FCSTD DOCUMENT  (FreeCAD 0.16R)
Label: brakeDiscVs
License: All rights reserved
LicenseURL: http://en.wikipedia.org/wiki/All_rights_reserved
objects: Sketcher::SketchObject×421, Part::Feature×420, App::DocumentObjectGroup×1
note: 841 computed .brp shape members not serialized (recipe doc carries the construction recipe); baked Part::Feature solids carry a one-line shape summary decoded from their .brp

FEATURE [Sketcher::SketchObject] Sketch420
  sketch-geometry (420):
    g0: ArcOfCircle CenterX=0 CenterY=0 CenterZ=0 NormalX=0 NormalY=0 NormalZ=1 Radius=58.5 StartAngle=4.60412 EndAngle=4.62963
    g1: ArcOfCircle CenterX=-27.6007 CenterY=-44.6934 CenterZ=0 NormalX=0 NormalY=0 NormalZ=1 Radius=1 StartAngle=1.8326 EndAngle=4.19648
    g2: ArcOfCircle CenterX=27.6007 CenterY=44.6934 CenterZ=0 NormalX=0 NormalY=0 NormalZ=1 Radius=1 StartAngle=4.97419 EndAngle=7.33807
    g3: ArcOfCircle CenterX=0 CenterY=0 CenterZ=0 NormalX=0 NormalY=0 NormalZ=1 Radius=58.5 StartAngle=0.415326 EndAngle=0.440839
    g4: ArcOfCircle CenterX=0 CenterY=0 CenterZ=0 NormalX=0 NormalY=0 NormalZ=1 Radius=45.5 StartAngle=0.283024 EndAngle=0.327705
    g5: Circle CenterX=-19.0526 CenterY=11 CenterZ=0 NormalX=0 NormalY=0 NormalZ=1 Radius=2.75
    g6: ArcOfCircle CenterX=-46.4894 CenterY=0.993219 CenterZ=0 NormalX=0 NormalY=0 NormalZ=1 Radius=1 StartAngle=3.75246 EndAngle=6.26182
    g7: ArcOfCircle CenterX=-53.0571 CenterY=-15.0104 CenterZ=0 NormalX=0 NormalY=0 NormalZ=1 Radius=1 StartAngle=1.13446 EndAngle=3.0674
    g8: ArcOfCircle CenterX=-26.413 CenterY=-39.4792 CenterZ=0 NormalX=0 NormalY=0 NormalZ=1 Radius=2 StartAngle=0.981156 EndAngle=1.65806
    g9: ArcOfCircle CenterX=52.1283 CenterY=15.9789 CenterZ=0 NormalX=0 NormalY=0 NormalZ=1 Radius=2 StartAngle=6.20458 EndAngle=7.41765
    g10: ArcOfCircle CenterX=0 CenterY=0 CenterZ=0 NormalX=0 NormalY=0 NormalZ=1 Radius=60 StartAngle=2.45564 EndAngle=2.78035
    g11: ArcOfCircle CenterX=45.6102 CenterY=13.2649 CenterZ=0 NormalX=0 NormalY=0 NormalZ=1 Radius=2 StartAngle=3.42462 EndAngle=4.10152
    g12: LineSegment StartX=3.74917 StartY=-26.4937 StartZ=0 EndX=11.5388 EndY=-39.9857 EndZ=0
    g13: ArcOfCircle CenterX=9.05093 CenterY=45.6106 CenterZ=0 NormalX=0 NormalY=0 NormalZ=1 Radius=1 StartAngle=2.00713 EndAngle=4.51649
    g14: ArcOfCircle CenterX=15.4177 CenterY=-52.1835 CenterZ=0 NormalX=0 NormalY=0 NormalZ=1 Radius=1 StartAngle=2.70526 EndAngle=5.29894
    g15: ArcOfCircle CenterX=0 CenterY=-22 CenterZ=0 NormalX=0 NormalY=0 NormalZ=1 Radius=4.5 StartAngle=5.71572 EndAngle=9.99225
    g16: ArcOfCircle CenterX=0 CenterY=0 CenterZ=0 NormalX=0 NormalY=0 NormalZ=1 Radius=45.5 StartAngle=1.50475 EndAngle=1.54929
    g17: LineSegment StartX=-34.5926 StartY=-41.6858 StartZ=0 EndX=-24.0177 EndY=-40.7606 EndZ=0
    g18: ArcOfCircle CenterX=-6.21354 CenterY=-57.1633 CenterZ=0 NormalX=0 NormalY=0 NormalZ=1 Radius=1 StartAngle=2.35619 EndAngle=4.60412
    g19: ArcOfCircle CenterX=34.7669 CenterY=39.6934 CenterZ=0 NormalX=0 NormalY=0 NormalZ=1 Radius=2 StartAngle=1.09765 EndAngle=1.65806
    g20: LineSegment StartX=-45.7581 StartY=4.28185 StartZ=0 EndX=-52.082 EndY=13.3132 EndZ=0
    g21: LineSegment StartX=-40.398 StartY=-10 StartZ=0 EndX=-24.8188 EndY=-10 EndZ=0
    g22: ArcOfCircle CenterX=0 CenterY=0 CenterZ=0 NormalX=0 NormalY=0 NormalZ=1 Radius=45.5 StartAngle=4.82088 EndAngle=4.86556
    g23: LineSegment StartX=52.9735 StartY=17.7915 StartZ=0 EndX=41.1802 EndY=23.2909 EndZ=0
    g24: ArcOfCircle CenterX=19.0526 CenterY=11 CenterZ=0 NormalX=0 NormalY=0 NormalZ=1 Radius=4.5 StartAngle=1.52693 EndAngle=5.80346
    g25: ArcOfCircle CenterX=-14.1368 CenterY=38.4857 CenterZ=0 NormalX=0 NormalY=0 NormalZ=1 Radius=3 StartAngle=0.523599 EndAngle=1.92282
    g26: ArcOfCircle CenterX=-47.3965 CenterY=3.1347 CenterZ=0 NormalX=0 NormalY=0 NormalZ=1 Radius=2 StartAngle=6.21714 EndAngle=6.89405
    g27: ArcOfCircle CenterX=43.346 CenterY=-16.8336 CenterZ=0 NormalX=0 NormalY=0 NormalZ=1 Radius=1 StartAngle=0.261799 EndAngle=2.77117
    g28: ArcOfCircle CenterX=43.346 CenterY=-16.8336 CenterZ=0 NormalX=0 NormalY=0 NormalZ=1 Radius=1 StartAngle=0.261799 EndAngle=2.77117
    g29: ArcOfCircle CenterX=-19.0526 CenterY=11 CenterZ=0 NormalX=0 NormalY=0 NormalZ=1 Radius=4.5 StartAngle=3.62132 EndAngle=7.89785
    g30: ArcOfCircle CenterX=31.9233 CenterY=-27.2929 CenterZ=0 NormalX=0 NormalY=0 NormalZ=1 Radius=2 StartAngle=3.66519 EndAngle=5.57582
    g31: ArcOfCircle CenterX=127.5 CenterY=220.836 CenterZ=0 NormalX=0 NormalY=0 NormalZ=1 Radius=201.5 StartAngle=4.11019 EndAngle=4.1146
    g32: LineSegment StartX=-26.1327 StartY=37.8051 StartZ=0 EndX=-23.9393 EndY=45.9908 EndZ=0
    g33: ArcOfCircle CenterX=51.5908 CenterY=-25.3898 CenterZ=0 NormalX=0 NormalY=0 NormalZ=1 Radius=1 StartAngle=3.57793 EndAngle=5.82585
    g34: ArcOfCircle CenterX=38.3227 CenterY=28.0645 CenterZ=0 NormalX=0 NormalY=0 NormalZ=1 Radius=2 StartAngle=3.77368 EndAngle=4.45059
    g35: ArcOfCircle CenterX=-127.5 CenterY=-220.836 CenterZ=0 NormalX=0 NormalY=0 NormalZ=1 Radius=200 StartAngle=0.940966 EndAngle=1.15343
    g36: ArcOfCircle CenterX=-46.1321 CenterY=11.3174 CenterZ=0 NormalX=0 NormalY=0 NormalZ=1 Radius=2 StartAngle=6.04261 EndAngle=6.71952
    g37: ArcOfCircle CenterX=20.1364 CenterY=49.1411 CenterZ=0 NormalX=0 NormalY=0 NormalZ=1 Radius=1 StartAngle=5.14872 EndAngle=7.29516
    g38: ArcOfCircle CenterX=-47.7836 CenterY=-31.984 CenterZ=0 NormalX=0 NormalY=0 NormalZ=1 Radius=1 StartAngle=1.48353 EndAngle=3.73145
    g39: ArcOfCircle CenterX=-0.993219 CenterY=-46.4894 CenterZ=0 NormalX=0 NormalY=0 NormalZ=1 Radius=1 StartAngle=5.32325 EndAngle=7.83262
    g40: ArcOfCircle CenterX=33.1036 CenterY=-40.5546 CenterZ=0 NormalX=0 NormalY=0 NormalZ=1 Radius=2 StartAngle=5.19474 EndAngle=6.19592
    g41: LineSegment StartX=11.6266 StartY=-44.4631 StartZ=0 EndX=2.988 EndY=-56.8002 EndZ=0
    g42: ArcOfCircle CenterX=127.5 CenterY=220.836 CenterZ=0 NormalX=0 NormalY=0 NormalZ=1 Radius=200 StartAngle=4.08256 EndAngle=4.29502
    g43: ArcOfCircle CenterX=-255 CenterY=0 CenterZ=0 NormalX=0 NormalY=0 NormalZ=1 Radius=201.5 StartAngle=6.28252 EndAngle=6.29087
    g44: ArcOfCircle CenterX=-39.598 CenterY=-14 CenterZ=0 NormalX=0 NormalY=0 NormalZ=1 Radius=2 StartAngle=1.5708 EndAngle=3.48143
    g45: ArcOfCircle CenterX=-24.8188 CenterY=8 CenterZ=0 NormalX=0 NormalY=0 NormalZ=1 Radius=2 StartAngle=0.479729 EndAngle=1.5708
    g46: ArcOfCircle CenterX=46.4277 CenterY=-32.1982 CenterZ=0 NormalX=0 NormalY=0 NormalZ=1 Radius=2 StartAngle=5.67683 EndAngle=6.54498
    g47: ArcOfCircle CenterX=-127.5 CenterY=-220.836 CenterZ=0 NormalX=0 NormalY=0 NormalZ=1 Radius=201.5 StartAngle=1.09765 EndAngle=1.11015
    g48: ArcOfCircle CenterX=-24.1048 CenterY=-39.7644 CenterZ=0 NormalX=0 NormalY=0 NormalZ=1 Radius=1 StartAngle=4.79966 EndAngle=7.30902
    g49: LineSegment StartX=-53.3972 StartY=9.11519 StartZ=0 EndX=-47.3085 EndY=0.419643 EndZ=0
    g50: ArcOfCircle CenterX=0 CenterY=0 CenterZ=0 NormalX=0 NormalY=0 NormalZ=1 Radius=45.5 StartAngle=0.981156 EndAngle=1.02584
    g51: ArcOfCircle CenterX=32.8672 CenterY=34.2928 CenterZ=0 NormalX=0 NormalY=0 NormalZ=1 Radius=2 StartAngle=3.94822 EndAngle=4.62512
    g52: ArcOfCircle CenterX=0 CenterY=22 CenterZ=0 NormalX=0 NormalY=0 NormalZ=1 Radius=4.5 StartAngle=1.52693 EndAngle=1.61467
    g53: ArcOfCircle CenterX=-26.2612 CenterY=31.4857 CenterZ=0 NormalX=0 NormalY=0 NormalZ=1 Radius=3 StartAngle=2.26597 EndAngle=3.66519
    g54: ArcOfCircle CenterX=-32.8672 CenterY=-34.2928 CenterZ=0 NormalX=0 NormalY=0 NormalZ=1 Radius=2 StartAngle=0.806623 EndAngle=1.48353
    g55: LineSegment StartX=3.72902 StartY=-45.8065 StartZ=0 EndX=-6.92065 EndY=-56.4562 EndZ=0
    g56: ArcOfCircle CenterX=-44.0254 CenterY=-14.967 CenterZ=0 NormalX=0 NormalY=0 NormalZ=1 Radius=1 StartAngle=4.10152 EndAngle=6.61089
    g57: ArcOfCircle CenterX=0 CenterY=0 CenterZ=0 NormalX=0 NormalY=0 NormalZ=1 Radius=44 StartAngle=2.43423 EndAngle=2.80176
    g58: LineSegment StartX=-19.1709 StartY=41.7686 StartZ=0 EndX=-14.5114 EndY=51.7609 EndZ=0
    g59: LineSegment StartX=53.1261 StartY=-22.8017 StartZ=0 EndX=46.517 EndY=-8.62831 EndZ=0
    g60: ArcOfCircle CenterX=-13.2649 CenterY=45.6102 CenterZ=0 NormalX=0 NormalY=0 NormalZ=1 Radius=2 StartAngle=4.99541 EndAngle=5.67232
    g61: ArcOfCircle CenterX=39.9023 CenterY=-37.155 CenterZ=0 NormalX=0 NormalY=0 NormalZ=1 Radius=2 StartAngle=5.15739 EndAngle=6.37045
    g62: ArcOfCircle CenterX=-34.7669 CenterY=-39.6934 CenterZ=0 NormalX=0 NormalY=0 NormalZ=1 Radius=2 StartAngle=4.23924 EndAngle=4.79966
    g63: LineSegment StartX=32.3005 StartY=-32.6929 StartZ=0 EndX=31.493 EndY=-41.922 EndZ=0
    g64: LineSegment StartX=-32.3005 StartY=32.6929 StartZ=0 EndX=-31.493 EndY=41.922 EndZ=0
    g65: ArcOfCircle CenterX=127.5 CenterY=-220.836 CenterZ=0 NormalX=0 NormalY=0 NormalZ=1 Radius=201.5 StartAngle=2.14485 EndAngle=2.15735
    g66: ArcOfCircle CenterX=127.5 CenterY=-220.836 CenterZ=0 NormalX=0 NormalY=0 NormalZ=1 Radius=200 StartAngle=1.98816 EndAngle=2.20063
    g67: LineSegment StartX=-28.8593 StartY=-29.9857 StartZ=0 EndX=-21.0697 EndY=-16.4937 EndZ=0
    g68: ArcOfCircle CenterX=0 CenterY=0 CenterZ=0 NormalX=0 NormalY=0 NormalZ=1 Radius=45.5 StartAngle=4.99541 EndAngle=5.04009
    g69: ArcOfCircle CenterX=0 CenterY=0 CenterZ=0 NormalX=0 NormalY=0 NormalZ=1 Radius=60 StartAngle=3.50284 EndAngle=3.82755
    g70: ArcOfCircle CenterX=127.5 CenterY=220.836 CenterZ=0 NormalX=0 NormalY=0 NormalZ=1 Radius=201.5 StartAngle=4.14754 EndAngle=4.15356
    g71: ArcOfCircle CenterX=0 CenterY=22 CenterZ=0 NormalX=0 NormalY=0 NormalZ=1 Radius=4.5 StartAngle=2.57412 EndAngle=6.85065
    g72: ArcOfCircle CenterX=29.122 CenterY=-36.2514 CenterZ=0 NormalX=0 NormalY=0 NormalZ=1 Radius=1 StartAngle=6.02139 EndAngle=8.53075
    g73: ArcOfCircle CenterX=-51.3135 CenterY=23.6469 CenterZ=0 NormalX=0 NormalY=0 NormalZ=1 Radius=2 StartAngle=2.70977 EndAngle=3.57792
    g74: ArcOfCircle CenterX=36.2514 CenterY=29.122 CenterZ=0 NormalX=0 NormalY=0 NormalZ=1 Radius=1 StartAngle=1.309 EndAngle=3.81836
    g75: ArcOfCircle CenterX=-20.9835 CenterY=42.6139 CenterZ=0 NormalX=0 NormalY=0 NormalZ=1 Radius=2 StartAngle=5.16995 EndAngle=5.84685
    g76: LineSegment StartX=41.5341 StartY=-19.6738 StartZ=0 EndX=45.4322 EndY=-34.2216 EndZ=0
    g77: ArcOfCircle CenterX=0 CenterY=0 CenterZ=0 NormalX=0 NormalY=0 NormalZ=1 Radius=45.5 StartAngle=6.04261 EndAngle=6.08729
    g78: ArcOfCircle CenterX=-24.9053 CenterY=46.2496 CenterZ=0 NormalX=0 NormalY=0 NormalZ=1 Radius=1 StartAngle=6.02139 EndAngle=8.38527
    g79: ArcOfCircle CenterX=6.21354 CenterY=57.1633 CenterZ=0 NormalX=0 NormalY=0 NormalZ=1 Radius=1 StartAngle=5.49779 EndAngle=7.74571
    g80: ArcOfCircle CenterX=-255 CenterY=0 CenterZ=0 NormalX=0 NormalY=0 NormalZ=1 Radius=201.5 StartAngle=0.0504506 EndAngle=0.0629534
    g81: LineSegment StartX=-26.5873 StartY=-37.4868 StartZ=0 EndX=-37.5706 EndY=-38.4477 EndZ=0
    g82: ArcOfCircle CenterX=-34.2928 CenterY=32.8672 CenterZ=0 NormalX=0 NormalY=0 NormalZ=1 Radius=2 StartAngle=5.51901 EndAngle=6.19592
    g83: LineSegment StartX=41.5341 StartY=-19.6738 StartZ=0 EndX=45.4322 EndY=-34.2216 EndZ=0
    g84: ArcOfCircle CenterX=-16.992 CenterY=49.9557 CenterZ=0 NormalX=0 NormalY=0 NormalZ=1 Radius=2 StartAngle=2.14484 EndAngle=2.70526
    g85: ArcOfCircle CenterX=51.0983 CenterY=24.1085 CenterZ=0 NormalX=0 NormalY=0 NormalZ=1 Radius=2 StartAngle=0.440839 EndAngle=1.309
    g86: ArcOfCircle CenterX=-51.0983 CenterY=-24.1085 CenterZ=0 NormalX=0 NormalY=0 NormalZ=1 Radius=2 StartAngle=3.58243 EndAngle=4.45059
    g87: LineSegment StartX=19.6738 StartY=41.5341 StartZ=0 EndX=27.8595 EndY=43.7275 EndZ=0
    g88: ArcOfCircle CenterX=0 CenterY=0 CenterZ=0 NormalX=0 NormalY=0 NormalZ=1 Radius=45.5 StartAngle=0.63209 EndAngle=0.676771
    g89: ArcOfCircle CenterX=0 CenterY=0 CenterZ=0 NormalX=0 NormalY=0 NormalZ=1 Radius=44 StartAngle=5.06442 EndAngle=5.40756
    g90: LineSegment StartX=-3.25637 StartY=-57.7208 StartZ=0 EndX=7.80178 EndY=-46.6627 EndZ=0
    g91: LineSegment StartX=-11.0788 StartY=-54.7722 StartZ=0 EndX=-0.419643 EndY=-47.3085 EndZ=0
    g92: LineSegment StartX=45.7581 StartY=-4.28185 StartZ=0 EndX=52.082 EndY=-13.3132 EndZ=0
    g93: LineSegment StartX=37.4868 StartY=-26.5873 StartZ=0 EndX=38.5317 EndY=-38.5308 EndZ=0
    g94: ArcOfCircle CenterX=-7.67463 CenterY=41.2929 CenterZ=0 NormalX=0 NormalY=0 NormalZ=1 Radius=2 StartAngle=1.75456 EndAngle=3.66519
    g95: ArcOfCircle CenterX=20.9835 CenterY=-42.6139 CenterZ=0 NormalX=0 NormalY=0 NormalZ=1 Radius=2 StartAngle=2.02835 EndAngle=2.70526
    g96: ArcOfCircle CenterX=51.7589 CenterY=-10.2623 CenterZ=0 NormalX=0 NormalY=0 NormalZ=1 Radius=2 StartAngle=0.0504502 EndAngle=0.610865
    g97: ArcOfCircle CenterX=-3.1347 CenterY=-47.3965 CenterZ=0 NormalX=0 NormalY=0 NormalZ=1 Radius=2 StartAngle=1.50475 EndAngle=2.18166
    g98: LineSegment StartX=-2.01711 StartY=-27.4937 StartZ=0 EndX=-9.40668 EndY=-40.2929 EndZ=0
    g99: ArcOfCircle CenterX=-52.9011 CenterY=12.7396 CenterZ=0 NormalX=0 NormalY=0 NormalZ=1 Radius=1 StartAngle=0.610866 EndAngle=3.20455
    g100: LineSegment StartX=-46.3099 StartY=-34.6077 StartZ=0 EndX=-30.7308 EndY=-35.9707 EndZ=0
    g101: ArcOfCircle CenterX=19.0526 CenterY=-11 CenterZ=0 NormalX=0 NormalY=0 NormalZ=1 Radius=4.5 StartAngle=5.71572 EndAngle=5.80346
    g102: LineSegment StartX=26.5873 StartY=37.4868 StartZ=0 EndX=37.5706 EndY=38.4477 EndZ=0
    g103: ArcOfCircle CenterX=-12.226 CenterY=-53.1339 CenterZ=0 NormalX=0 NormalY=0 NormalZ=1 Radius=2 StartAngle=4.11019 EndAngle=5.32325
    g104: ArcOfCircle CenterX=0 CenterY=0 CenterZ=0 NormalX=0 NormalY=0 NormalZ=1 Radius=45.5 StartAngle=4.47181 EndAngle=4.51649
    g105: ArcOfCircle CenterX=12.226 CenterY=53.1339 CenterZ=0 NormalX=0 NormalY=0 NormalZ=1 Radius=2 StartAngle=0.968596 EndAngle=2.18166
    g106: LineSegment StartX=48.3595 StartY=-31.6805 StartZ=0 EndX=44.312 EndY=-16.5748 EndZ=0
    g107: LineSegment StartX=-18.8046 StartY=50.801 StartZ=0 EndX=-23.2909 EndY=41.1802 EndZ=0
    g108: ArcOfCircle CenterX=-19.3376 CenterY=-17.4937 CenterZ=0 NormalX=0 NormalY=0 NormalZ=1 Radius=2 StartAngle=1.52693 EndAngle=2.61799
    g109: ArcOfCircle CenterX=-5.17792 CenterY=56.2622 CenterZ=0 NormalX=0 NormalY=0 NormalZ=1 Radius=2 StartAngle=1.66257 EndAngle=2.53073
    g110: ArcOfCircle CenterX=-127.5 CenterY=220.836 CenterZ=0 NormalX=0 NormalY=0 NormalZ=1 Radius=201.5 StartAngle=5.19474 EndAngle=5.20076
    g111: LineSegment StartX=-32.6929 StartY=-32.3005 StartZ=0 EndX=-47.6965 EndY=-30.9878 EndZ=0
    g112: ArcOfCircle CenterX=-7.09467 CenterY=45.9556 CenterZ=0 NormalX=0 NormalY=0 NormalZ=1 Radius=1 StartAngle=2.35619 EndAngle=4.86556
    g113: ArcOfCircle CenterX=0 CenterY=0 CenterZ=0 NormalX=0 NormalY=0 NormalZ=1 Radius=45.5 StartAngle=5.16995 EndAngle=5.21463
    g114: ArcOfCircle CenterX=51.0983 CenterY=24.1085 CenterZ=0 NormalX=0 NormalY=0 NormalZ=1 Radius=2 StartAngle=0.440839 EndAngle=1.309
    g115: ArcOfCircle CenterX=5.48122 CenterY=25.4937 CenterZ=0 NormalX=0 NormalY=0 NormalZ=1 Radius=2 StartAngle=2.61799 EndAngle=3.70906
    g116: ArcOfCircle CenterX=19.1562 CenterY=43.466 CenterZ=0 NormalX=0 NormalY=0 NormalZ=1 Radius=2 StartAngle=4.29728 EndAngle=4.97419
    g117: LineSegment StartX=-53.1261 StartY=22.8017 StartZ=0 EndX=-46.517 EndY=8.62831 EndZ=0
    g118: ArcOfCircle CenterX=24.8188 CenterY=8 CenterZ=0 NormalX=0 NormalY=0 NormalZ=1 Radius=2 StartAngle=1.5708 EndAngle=2.66186
    g119: ArcOfCircle CenterX=26.2612 CenterY=-31.4857 CenterZ=0 NormalX=0 NormalY=0 NormalZ=1 Radius=3 StartAngle=5.40756 EndAngle=6.80678
    g120: LineSegment StartX=-51.6159 StartY=-26.0403 StartZ=0 EndX=-36.5102 EndY=-30.0879 EndZ=0
    g121: ArcOfCircle CenterX=-39.598 CenterY=14 CenterZ=0 NormalX=0 NormalY=0 NormalZ=1 Radius=2 StartAngle=2.80176 EndAngle=4.71239
    g122: ArcOfCircle CenterX=13.5292 CenterY=53.454 CenterZ=0 NormalX=0 NormalY=0 NormalZ=1 Radius=1 StartAngle=5.32325 EndAngle=7.25619
    g123: ArcOfCircle CenterX=-46.1356 CenterY=-32.6153 CenterZ=0 NormalX=0 NormalY=0 NormalZ=1 Radius=2 StartAngle=3.75696 EndAngle=4.62512
    g124: ArcOfCircle CenterX=-25.6322 CenterY=-44.6683 CenterZ=0 NormalX=0 NormalY=0 NormalZ=1 Radius=2 StartAngle=4.18812 EndAngle=4.97419
    g125: ArcOfCircle CenterX=39.4792 CenterY=-26.413 CenterZ=0 NormalX=0 NormalY=0 NormalZ=1 Radius=2 StartAngle=2.55195 EndAngle=3.22886
    g126: LineSegment StartX=41.7686 StartY=19.1709 StartZ=0 EndX=52.6345 EndY=14.1041 EndZ=0
    g127: ArcOfCircle CenterX=-0.285064 CenterY=28.4937 CenterZ=0 NormalX=0 NormalY=0 NormalZ=1 Radius=2 StartAngle=3.66519 EndAngle=4.75626
    g128: ArcOfCircle CenterX=16.8336 CenterY=43.346 CenterZ=0 NormalX=0 NormalY=0 NormalZ=1 Radius=1 StartAngle=1.8326 EndAngle=4.34196
    g129: ArcOfCircle CenterX=26.413 CenterY=39.4792 CenterZ=0 NormalX=0 NormalY=0 NormalZ=1 Radius=2 StartAngle=4.12275 EndAngle=4.79966
    g130: ArcOfCircle CenterX=51.3135 CenterY=-23.6469 CenterZ=0 NormalX=0 NormalY=0 NormalZ=1 Radius=2 StartAngle=5.85136 EndAngle=6.71952
    g131: ArcOfCircle CenterX=0 CenterY=0 CenterZ=0 NormalX=0 NormalY=0 NormalZ=1 Radius=58.5 StartAngle=0.589859 EndAngle=0.615372
    g132: ArcOfCircle CenterX=-19.0526 CenterY=-11 CenterZ=0 NormalX=0 NormalY=0 NormalZ=1 Radius=4.5 StartAngle=3.62132 EndAngle=3.70906
    g133: ArcOfCircle CenterX=127.5 CenterY=-220.836 CenterZ=0 NormalX=0 NormalY=0 NormalZ=1 Radius=201.5 StartAngle=2.09373 EndAngle=2.10208
    g134: ArcOfCircle CenterX=255 CenterY=0 CenterZ=0 NormalX=0 NormalY=0 NormalZ=1 Radius=201.5 StartAngle=3.06299 EndAngle=3.0674
    g135: ArcOfCircle CenterX=-40.7576 CenterY=-22.3845 CenterZ=0 NormalX=0 NormalY=0 NormalZ=1 Radius=1.00001 StartAngle=4.27606 EndAngle=6.79205
    g136: LineSegment StartX=-30.1913 StartY=-28.2929 StartZ=0 EndX=-22.8017 EndY=-15.4937 EndZ=0
    g137: LineSegment StartX=-48.3595 StartY=31.6805 StartZ=0 EndX=-44.312 EndY=16.5748 EndZ=0
    g138: ArcOfCircle CenterX=-38.3227 CenterY=-28.0645 CenterZ=0 NormalX=0 NormalY=0 NormalZ=1 Radius=2 StartAngle=0.63209 EndAngle=1.309
    g139: ArcOfCircle CenterX=127.5 CenterY=220.836 CenterZ=0 NormalX=0 NormalY=0 NormalZ=1 Radius=201.5 StartAngle=4.23924 EndAngle=4.25174
    g140: ArcOfCircle CenterX=3.80716 CenterY=-57.3738 CenterZ=0 NormalX=0 NormalY=0 NormalZ=1 Radius=1 StartAngle=2.53073 EndAngle=4.77865
    g141: ArcOfCircle CenterX=0 CenterY=0 CenterZ=0 NormalX=0 NormalY=0 NormalZ=1 Radius=45.5 StartAngle=4.12275 EndAngle=4.16743
    g142: LineSegment StartX=-28.8593 StartY=29.9857 StartZ=0 EndX=-21.0697 EndY=16.4937 EndZ=0
    g143: ArcOfCircle CenterX=0 CenterY=0 CenterZ=0 NormalX=0 NormalY=0 NormalZ=1 Radius=45.5 StartAngle=1.85382 EndAngle=1.8985
    g144: ArcOfCircle CenterX=-7.67463 CenterY=-41.2929 CenterZ=0 NormalX=0 NormalY=0 NormalZ=1 Radius=2 StartAngle=2.61799 EndAngle=4.52863
    g145: ArcOfCircle CenterX=0 CenterY=0 CenterZ=0 NormalX=0 NormalY=0 NormalZ=1 Radius=44 StartAngle=4.52863 EndAngle=4.89615
    g146: ArcOfCircle CenterX=-39.5279 CenterY=38.4436 CenterZ=0 NormalX=0 NormalY=0 NormalZ=1 Radius=1 StartAngle=0.0872665 EndAngle=2.0202
    g147: ArcOfCircle CenterX=0 CenterY=0 CenterZ=0 NormalX=0 NormalY=0 NormalZ=1 Radius=45.5 StartAngle=2.72649 EndAngle=2.77117
    g148: ArcOfCircle CenterX=-14.1368 CenterY=-38.4857 CenterZ=0 NormalX=0 NormalY=0 NormalZ=1 Radius=3 StartAngle=4.36036 EndAngle=5.75959
    g149: ArcOfCircle CenterX=0 CenterY=0 CenterZ=0 NormalX=0 NormalY=0 NormalZ=1 Radius=45.5 StartAngle=3.07555 EndAngle=3.12023
    g150: ArcOfCircle CenterX=39.5279 CenterY=-38.4436 CenterZ=0 NormalX=0 NormalY=0 NormalZ=1 Radius=1 StartAngle=3.22886 EndAngle=5.16179
    g151: ArcOfCircle CenterX=53.0571 CenterY=15.0104 CenterZ=0 NormalX=0 NormalY=0 NormalZ=1 Radius=1 StartAngle=4.27606 EndAngle=6.20899
    g152: ArcOfCircle CenterX=0 CenterY=0 CenterZ=0 NormalX=0 NormalY=0 NormalZ=1 Radius=45.5 StartAngle=6.21714 EndAngle=6.26182
    g153: ArcOfCircle CenterX=-43.346 CenterY=16.8336 CenterZ=0 NormalX=0 NormalY=0 NormalZ=1 Radius=1 StartAngle=3.40339 EndAngle=5.91276
    g154: ArcOfCircle CenterX=24.5338 CenterY=14.4937 CenterZ=0 NormalX=0 NormalY=0 NormalZ=1 Radius=2 StartAngle=2.61799 EndAngle=3.70906
    g155: LineSegment StartX=-41.7686 StartY=-19.1709 StartZ=0 EndX=-52.6345 EndY=-14.1041 EndZ=0
    g156: ArcOfCircle CenterX=255 CenterY=0 CenterZ=0 NormalX=0 NormalY=0 NormalZ=1 Radius=200 StartAngle=3.03536 EndAngle=3.24782
    g157: ArcOfCircle CenterX=0 CenterY=0 CenterZ=0 NormalX=0 NormalY=0 NormalZ=1 Radius=58.5 StartAngle=0.415326 EndAngle=0.440839
    g158: ArcOfCircle CenterX=-5.48122 CenterY=25.4937 CenterZ=0 NormalX=0 NormalY=0 NormalZ=1 Radius=2 StartAngle=5.71572 EndAngle=6.80678
    g159: ArcOfCircle CenterX=6.21354 CenterY=57.1633 CenterZ=0 NormalX=0 NormalY=0 NormalZ=1 Radius=1 StartAngle=5.49779 EndAngle=7.74571
    g160: ArcOfCircle CenterX=46.3981 CenterY=-33.9627 CenterZ=0 NormalX=0 NormalY=0 NormalZ=1 Radius=1 StartAngle=3.40339 EndAngle=5.65131
    g161: ArcOfCircle CenterX=0 CenterY=0 CenterZ=0 NormalX=0 NormalY=0 NormalZ=1 Radius=45.5 StartAngle=0.63209 EndAngle=0.676771
    g162: ArcOfCircle CenterX=0 CenterY=0 CenterZ=0 NormalX=0 NormalY=0 NormalZ=1 Radius=45.5 StartAngle=2.02835 EndAngle=2.07303
    g163: ArcOfCircle CenterX=14.967 CenterY=-44.0254 CenterZ=0 NormalX=0 NormalY=0 NormalZ=1 Radius=1 StartAngle=5.67232 EndAngle=8.18169
    g164: LineSegment StartX=-51.6159 StartY=-26.0403 StartZ=0 EndX=-36.5102 EndY=-30.0879 EndZ=0
    g165: LineSegment StartX=37.8051 StartY=26.1327 StartZ=0 EndX=52.3528 EndY=22.2346 EndZ=0
    g166: LineSegment StartX=3.74917 StartY=26.4937 StartZ=0 EndX=11.5388 EndY=39.9857 EndZ=0
    g167: ArcOfCircle CenterX=13.2649 CenterY=-45.6102 CenterZ=0 NormalX=0 NormalY=0 NormalZ=1 Radius=2 StartAngle=1.85382 EndAngle=2.53073
    g168: ArcOfCircle CenterX=-127.5 CenterY=-220.836 CenterZ=0 NormalX=0 NormalY=0 NormalZ=1 Radius=201.5 StartAngle=1.00595 EndAngle=1.01197
    g169: ArcOfCircle CenterX=39.598 CenterY=14 CenterZ=0 NormalX=0 NormalY=0 NormalZ=1 Radius=2 StartAngle=4.71239 EndAngle=6.62302
    g170: ArcOfCircle CenterX=-0.285064 CenterY=-28.4937 CenterZ=0 NormalX=0 NormalY=0 NormalZ=1 Radius=2 StartAngle=1.52693 EndAngle=2.61799
    g171: ArcOfCircle CenterX=-36.2514 CenterY=-29.122 CenterZ=0 NormalX=0 NormalY=0 NormalZ=1 Radius=1 StartAngle=4.45059 EndAngle=6.95996
    g172: ArcOfCircle CenterX=-19.0526 CenterY=11 CenterZ=0 NormalX=0 NormalY=0 NormalZ=1 Radius=4.5 StartAngle=2.57412 EndAngle=2.66186
    g173: ArcOfCircle CenterX=-31.9233 CenterY=-27.2929 CenterZ=0 NormalX=0 NormalY=0 NormalZ=1 Radius=2 StartAngle=3.84895 EndAngle=5.75959
    g174: ArcOfCircle CenterX=-127.5 CenterY=220.836 CenterZ=0 NormalX=0 NormalY=0 NormalZ=1 Radius=201.5 StartAngle=5.23532 EndAngle=5.24367
    g175: Circle CenterX=-19.0526 CenterY=-11 CenterZ=0 NormalX=0 NormalY=0 NormalZ=1 Radius=2.75
    g176: ArcOfCircle CenterX=18.5695 CenterY=48.9458 CenterZ=0 NormalX=0 NormalY=0 NormalZ=1 Radius=2 StartAngle=1.00595 EndAngle=2.00713
    g177: ArcOfCircle CenterX=52.6116 CenterY=23.2006 CenterZ=0 NormalX=0 NormalY=0 NormalZ=1 Radius=1 StartAngle=4.45059 EndAngle=6.69851
    g178: LineSegment StartX=-37.8051 StartY=-26.1327 StartZ=0 EndX=-52.3528 EndY=-22.2346 EndZ=0
    g179: ArcOfCircle CenterX=24.5338 CenterY=-14.4937 CenterZ=0 NormalX=0 NormalY=0 NormalZ=1 Radius=2 StartAngle=2.57412 EndAngle=3.66519
    g180: LineSegment StartX=-39.598 StartY=12 StartZ=0 EndX=-24.8188 EndY=12 EndZ=0
    g181: ArcOfCircle CenterX=0 CenterY=0 CenterZ=0 NormalX=0 NormalY=0 NormalZ=1 Radius=58.5 StartAngle=2.68425 EndAngle=2.70977
    g182: LineSegment StartX=-25.1146 StartY=-46.6002 StartZ=0 EndX=-16.5748 EndY=-44.312 EndZ=0
    g183: ArcOfCircle CenterX=-19.3376 CenterY=17.4937 CenterZ=0 NormalX=0 NormalY=0 NormalZ=1 Radius=2 StartAngle=3.66519 EndAngle=4.75626
    g184: LineSegment StartX=-3.74917 StartY=-26.4937 StartZ=0 EndX=-11.5388 EndY=-39.9857 EndZ=0
    g185: ArcOfCircle CenterX=0 CenterY=0 CenterZ=0 NormalX=0 NormalY=0 NormalZ=1 Radius=45.5 StartAngle=2.37742 EndAngle=2.4221
    g186: ArcOfCircle CenterX=0 CenterY=0 CenterZ=0 NormalX=0 NormalY=0 NormalZ=1 Radius=45.5 StartAngle=1.15569 EndAngle=1.20037
    g187: LineSegment StartX=-11.5388 StartY=39.9857 StartZ=0 EndX=-3.74917 EndY=26.4937 EndZ=0
    g188: ArcOfCircle CenterX=51.5 CenterY=0.135994 CenterZ=0 NormalX=0 NormalY=0 NormalZ=1 Radius=2 StartAngle=6.28252 EndAngle=7.06858
    g189: ArcOfCircle CenterX=-52.6256 CenterY=-7.13188 CenterZ=0 NormalX=0 NormalY=0 NormalZ=1 Radius=1 StartAngle=0.959931 EndAngle=3.10637
    g190: LineSegment StartX=-11.6266 StartY=44.4631 StartZ=0 EndX=-2.988 EndY=56.8002 EndZ=0
    g191: LineSegment StartX=-45.8065 StartY=-3.72902 StartZ=0 EndX=-51.7989 EndY=2.26334 EndZ=0
    g192: ArcOfCircle CenterX=7.09467 CenterY=-45.9556 CenterZ=0 NormalX=0 NormalY=0 NormalZ=1 Radius=1 StartAngle=5.49779 EndAngle=8.00715
    g193: ArcOfCircle CenterX=-127.5 CenterY=220.836 CenterZ=0 NormalX=0 NormalY=0 NormalZ=1 Radius=200 StartAngle=5.12976 EndAngle=5.34222
    g194: ArcOfCircle CenterX=255 CenterY=0 CenterZ=0 NormalX=0 NormalY=0 NormalZ=1 Radius=201.5 StartAngle=3.19204 EndAngle=3.20455
    g195: ArcOfCircle CenterX=-19.1562 CenterY=-43.466 CenterZ=0 NormalX=0 NormalY=0 NormalZ=1 Radius=2 StartAngle=1.15569 EndAngle=1.8326
    g196: ArcOfCircle CenterX=-5.48122 CenterY=-25.4937 CenterZ=0 NormalX=0 NormalY=0 NormalZ=1 Radius=2 StartAngle=5.75959 EndAngle=6.85065
    g197: ArcOfCircle CenterX=24.8188 CenterY=14 CenterZ=0 NormalX=0 NormalY=0 NormalZ=1 Radius=2 StartAngle=3.62132 EndAngle=4.71239
    g198: ArcOfCircle CenterX=-5.14323 CenterY=47.2207 CenterZ=0 NormalX=0 NormalY=0 NormalZ=1 Radius=2 StartAngle=4.82088 EndAngle=5.49779
    g199: LineSegment StartX=28.8593 StartY=29.9857 StartZ=0 EndX=21.0697 EndY=16.4937 EndZ=0
    g200: LineSegment StartX=3.25637 StartY=57.7208 StartZ=0 EndX=-7.80178 EndY=46.6627 EndZ=0
    g201: ArcOfCircle CenterX=0.285064 CenterY=-28.4937 CenterZ=0 NormalX=0 NormalY=0 NormalZ=1 Radius=2 StartAngle=0.523599 EndAngle=1.61467
    g202: LineSegment StartX=24.8188 StartY=12 StartZ=0 EndX=39.598 EndY=12 EndZ=0
    g203: ArcOfCircle CenterX=0 CenterY=0 CenterZ=0 NormalX=0 NormalY=0 NormalZ=1 Radius=45.5 StartAngle=2.20289 EndAngle=2.24757
    g204: ArcOfCircle CenterX=14.1368 CenterY=-38.4857 CenterZ=0 NormalX=0 NormalY=0 NormalZ=1 Radius=3 StartAngle=3.66519 EndAngle=5.06442
    g205: LineSegment StartX=6.81622 StartY=-57.4094 StartZ=0 EndX=15.7861 EndY=-44.599 EndZ=0
    g206: ArcOfCircle CenterX=39.598 CenterY=-14 CenterZ=0 NormalX=0 NormalY=0 NormalZ=1 Radius=2 StartAngle=5.94335 EndAngle=7.85398
    g207: ArcOfCircle CenterX=0.993219 CenterY=46.4894 CenterZ=0 NormalX=0 NormalY=0 NormalZ=1 Radius=1.00001 StartAngle=2.18166 EndAngle=4.69766
    g208: LineSegment StartX=-44.3194 StartY=12.1626 StartZ=0 EndX=-50.6845 EndY=25.8124 EndZ=0
    g209: ArcOfCircle CenterX=47.3965 CenterY=-3.1347 CenterZ=0 NormalX=0 NormalY=0 NormalZ=1 Radius=2 StartAngle=3.07555 EndAngle=3.75246
    g210: ArcOfCircle CenterX=47.2207 CenterY=5.14323 CenterZ=0 NormalX=0 NormalY=0 NormalZ=1 Radius=2 StartAngle=3.25008 EndAngle=3.92699
    g211: ArcOfCircle CenterX=255 CenterY=0 CenterZ=0 NormalX=0 NormalY=0 NormalZ=1 Radius=201.5 StartAngle=3.10035 EndAngle=3.10637
    g212: ArcOfCircle CenterX=0 CenterY=0 CenterZ=0 NormalX=0 NormalY=0 NormalZ=1 Radius=44 StartAngle=4.01722 EndAngle=4.36036
    g213: ArcOfCircle CenterX=24.9053 CenterY=-46.2496 CenterZ=0 NormalX=0 NormalY=0 NormalZ=1 Radius=1 StartAngle=2.87979 EndAngle=5.24367
    g214: ArcOfCircle CenterX=-24.5338 CenterY=-14.4937 CenterZ=0 NormalX=0 NormalY=0 NormalZ=1 Radius=2 StartAngle=5.75959 EndAngle=6.85065
    g215: LineSegment StartX=-27.7996 StartY=45.05 StartZ=0 EndX=-30.0879 EndY=36.5102 EndZ=0
    g216: ArcOfCircle CenterX=-43.466 CenterY=19.1562 CenterZ=0 NormalX=0 NormalY=0 NormalZ=1 Radius=2 StartAngle=5.86808 EndAngle=6.54498
    g217: LineSegment StartX=4.28185 StartY=45.7581 StartZ=0 EndX=14.1028 EndY=52.6348 EndZ=0
    g218: ArcOfCircle CenterX=-37.4834 CenterY=-39.4439 CenterZ=0 NormalX=0 NormalY=0 NormalZ=1 Radius=1 StartAngle=1.65806 EndAngle=4.25174
    g219: ArcOfCircle CenterX=-11.3174 CenterY=-46.1321 CenterZ=0 NormalX=0 NormalY=0 NormalZ=1 Radius=2 StartAngle=1.33022 EndAngle=2.00713
    g220: LineSegment StartX=-52.9735 StartY=-17.7915 StartZ=0 EndX=-41.1802 EndY=-23.2909 EndZ=0
    g221: ArcOfCircle CenterX=0 CenterY=0 CenterZ=0 NormalX=0 NormalY=0 NormalZ=1 Radius=45.5 StartAngle=3.94822 EndAngle=3.9929
    g222: LineSegment StartX=26.1327 StartY=-37.8051 StartZ=0 EndX=23.9393 EndY=-45.9908 EndZ=0
    g223: ArcOfCircle CenterX=0 CenterY=0 CenterZ=0 NormalX=0 NormalY=0 NormalZ=1 Radius=58.5 StartAngle=5.65131 EndAngle=5.67683
    g224: ArcOfCircle CenterX=-47.2207 CenterY=-5.14323 CenterZ=0 NormalX=0 NormalY=0 NormalZ=1 Radius=2 StartAngle=0.108491 EndAngle=0.785398
    g225: ArcOfCircle CenterX=0 CenterY=0 CenterZ=0 NormalX=0 NormalY=0 NormalZ=1 Radius=45.5 StartAngle=4.29728 EndAngle=4.34196
    g226: LineSegment StartX=24.8188 StartY=10 StartZ=0 EndX=40.398 EndY=10 EndZ=0
    g227: LineSegment StartX=21.0697 StartY=-16.4937 StartZ=0 EndX=28.8593 EndY=-29.9857 EndZ=0
    g228: LineSegment StartX=32.6929 StartY=32.3005 StartZ=0 EndX=47.6965 EndY=30.9878 EndZ=0
    g229: ArcOfCircle CenterX=0 CenterY=0 CenterZ=0 NormalX=0 NormalY=0 NormalZ=1 Radius=45.5 StartAngle=2.90102 EndAngle=2.9457
    g230: ArcOfCircle CenterX=-45.6102 CenterY=-13.2649 CenterZ=0 NormalX=0 NormalY=0 NormalZ=1 Radius=2 StartAngle=0.283024 EndAngle=0.959931
    g231: ArcOfCircle CenterX=0 CenterY=0 CenterZ=0 NormalX=0 NormalY=0 NormalZ=1 Radius=45.5 StartAngle=1.67929 EndAngle=1.72397
    g232: ArcOfCircle CenterX=0 CenterY=0 CenterZ=0 NormalX=0 NormalY=0 NormalZ=1 Radius=45.5 StartAngle=5.69354 EndAngle=5.73823
    g233: LineSegment StartX=27.7996 StartY=-45.05 StartZ=0 EndX=30.0879 EndY=-36.5102 EndZ=0
    g234: LineSegment StartX=-35.096 StartY=40.7289 StartZ=0 EndX=-35.9707 EndY=30.7308 EndZ=0
    g235: ArcOfCircle CenterX=7.67463 CenterY=41.2929 CenterZ=0 NormalX=0 NormalY=0 NormalZ=1 Radius=2 StartAngle=5.75959 EndAngle=7.67022
    g236: ArcOfCircle CenterX=0 CenterY=0 CenterZ=0 NormalX=0 NormalY=0 NormalZ=1 Radius=58.5 StartAngle=3.55692 EndAngle=3.58243
    g237: LineSegment StartX=-40.398 StartY=10 StartZ=0 EndX=-24.8188 EndY=10 EndZ=0
    g238: ArcOfCircle CenterX=5.14323 CenterY=-47.2207 CenterZ=0 NormalX=0 NormalY=0 NormalZ=1 Radius=2 StartAngle=1.67929 EndAngle=2.35619
    g239: ArcOfCircle CenterX=4.67058 CenterY=56.3066 CenterZ=0 NormalX=0 NormalY=0 NormalZ=1 Radius=2 StartAngle=1.48804 EndAngle=2.35619
    g240: ArcOfCircle CenterX=16.992 CenterY=-49.9557 CenterZ=0 NormalX=0 NormalY=0 NormalZ=1 Radius=2 StartAngle=5.28644 EndAngle=5.84685
    g241: ArcOfCircle CenterX=-40.398 CenterY=7 CenterZ=0 NormalX=0 NormalY=0 NormalZ=1 Radius=3 StartAngle=1.5708 EndAngle=2.97002
    g242: ArcOfCircle CenterX=32.4892 CenterY=-42.0092 CenterZ=0 NormalX=0 NormalY=0 NormalZ=1 Radius=1 StartAngle=3.05433 EndAngle=5.20076
    g243: ArcOfCircle CenterX=-34.9745 CenterY=30.6437 CenterZ=0 NormalX=0 NormalY=0 NormalZ=1 Radius=1 StartAngle=3.05433 EndAngle=5.56369
    g244: LineSegment StartX=2.01711 StartY=-27.4937 StartZ=0 EndX=9.40668 EndY=-40.2929 EndZ=0
    g245: LineSegment StartX=-4.28185 StartY=-45.7581 StartZ=0 EndX=-14.1028 EndY=-52.6348 EndZ=0
    g246: ArcOfCircle CenterX=0 CenterY=0 CenterZ=0 NormalX=0 NormalY=0 NormalZ=1 Radius=44 StartAngle=0.339837 EndAngle=0.707361
    g247: ArcOfCircle CenterX=19.3376 CenterY=17.4937 CenterZ=0 NormalX=0 NormalY=0 NormalZ=1 Radius=2 StartAngle=4.66852 EndAngle=5.75959
    g248: ArcOfCircle CenterX=-52.6116 CenterY=-23.2006 CenterZ=0 NormalX=0 NormalY=0 NormalZ=1 Radius=1 StartAngle=1.309 EndAngle=3.55692
    g249: ArcOfCircle CenterX=5.17792 CenterY=-56.2622 CenterZ=0 NormalX=0 NormalY=0 NormalZ=1 Radius=2 StartAngle=4.80416 EndAngle=5.67232
    g250: ArcOfCircle CenterX=-40.398 CenterY=-7 CenterZ=0 NormalX=0 NormalY=0 NormalZ=1 Radius=3 StartAngle=3.31316 EndAngle=4.71239
    g251: ArcOfCircle CenterX=-52.1283 CenterY=-15.9789 CenterZ=0 NormalX=0 NormalY=0 NormalZ=1 Radius=2 StartAngle=3.06299 EndAngle=4.27606
    g252: LineSegment StartX=37.8051 StartY=26.1327 StartZ=0 EndX=52.3528 EndY=22.2346 EndZ=0
    g253: ArcOfCircle CenterX=0 CenterY=0 CenterZ=0 NormalX=0 NormalY=0 NormalZ=1 Radius=58.5 StartAngle=1.63706 EndAngle=1.66257
    g254: LineSegment StartX=25.1146 StartY=46.6002 StartZ=0 EndX=16.5748 EndY=44.312 EndZ=0
    g255: ArcOfCircle CenterX=-39.4792 CenterY=26.413 CenterZ=0 NormalX=0 NormalY=0 NormalZ=1 Radius=2 StartAngle=5.69354 EndAngle=6.37045
    g256: ArcOfCircle CenterX=51.6731 CenterY=8.39128 CenterZ=0 NormalX=0 NormalY=0 NormalZ=1 Radius=2 StartAngle=6.24194 EndAngle=7.24312
    g257: ArcOfCircle CenterX=-42.6139 CenterY=-20.9835 CenterZ=0 NormalX=0 NormalY=0 NormalZ=1 Radius=2 StartAngle=0.457557 EndAngle=1.13446
    g258: ArcOfCircle CenterX=37.4834 CenterY=39.4439 CenterZ=0 NormalX=0 NormalY=0 NormalZ=1 Radius=1 StartAngle=4.79966 EndAngle=7.39334
    g259: LineSegment StartX=46.3099 StartY=34.6077 StartZ=0 EndX=30.7308 EndY=35.9707 EndZ=0
    g260: ArcOfCircle CenterX=39.7644 CenterY=-24.1048 CenterZ=0 NormalX=0 NormalY=0 NormalZ=1 Radius=1 StartAngle=0.087267 EndAngle=2.59664
    g261: ArcOfCircle CenterX=0 CenterY=0 CenterZ=0 NormalX=0 NormalY=0 NormalZ=1 Radius=45.5 StartAngle=3.25008 EndAngle=3.29476
    g262: ArcOfCircle CenterX=-127.5 CenterY=220.836 CenterZ=0 NormalX=0 NormalY=0 NormalZ=1 Radius=201.5 StartAngle=5.28644 EndAngle=5.29894
    g263: ArcOfCircle CenterX=19.0526 CenterY=-11 CenterZ=0 NormalX=0 NormalY=0 NormalZ=1 Radius=4.5 StartAngle=0.479729 EndAngle=4.75626
    g264: ArcOfCircle CenterX=-24.8188 CenterY=14 CenterZ=0 NormalX=0 NormalY=0 NormalZ=1 Radius=2 StartAngle=4.71239 EndAngle=5.80346
    g265: LineSegment StartX=30.1913 StartY=28.2929 StartZ=0 EndX=22.8017 EndY=15.4937 EndZ=0
    g266: ArcOfCircle CenterX=11.3174 CenterY=46.1321 CenterZ=0 NormalX=0 NormalY=0 NormalZ=1 Radius=2 StartAngle=4.47181 EndAngle=5.14872
    g267: ArcOfCircle CenterX=0 CenterY=0 CenterZ=0 NormalX=0 NormalY=0 NormalZ=1 Radius=45.5 StartAngle=5.34448 EndAngle=5.38916
    g268: ArcOfCircle CenterX=0 CenterY=0 CenterZ=0 NormalX=0 NormalY=0 NormalZ=1 Radius=60 StartAngle=4.55004 EndAngle=4.87474
    g269: ArcOfCircle CenterX=255 CenterY=0 CenterZ=0 NormalX=0 NormalY=0 NormalZ=1 Radius=201.5 StartAngle=3.14092 EndAngle=3.14928
    g270: ArcOfCircle CenterX=-25.8678 CenterY=44.5324 CenterZ=0 NormalX=0 NormalY=0 NormalZ=1 Radius=2 StartAngle=2.09373 EndAngle=2.87979
    g271: LineSegment StartX=35.096 StartY=-40.7289 StartZ=0 EndX=35.9707 EndY=-30.7308 EndZ=0
    g272: ArcOfCircle CenterX=0 CenterY=0 CenterZ=0 NormalX=0 NormalY=0 NormalZ=1 Radius=45.5 StartAngle=3.42462 EndAngle=3.4693
    g273: ArcOfCircle CenterX=-51.6731 CenterY=-8.39128 CenterZ=0 NormalX=0 NormalY=0 NormalZ=1 Radius=2 StartAngle=3.10035 EndAngle=4.10152
    g274: LineSegment StartX=17.7242 StartY=50.7585 StartZ=0 EndX=8.62831 EndY=46.517 EndZ=0
    g275: LineSegment StartX=11.0789 StartY=54.7722 StartZ=0 EndX=0.419636 EndY=47.3085 EndZ=0
    g276: LineSegment StartX=-37.4868 StartY=26.5873 StartZ=0 EndX=-38.5317 EndY=38.5308 EndZ=0
    g277: ArcOfCircle CenterX=0 CenterY=0 CenterZ=0 NormalX=0 NormalY=0 NormalZ=1 Radius=45.5 StartAngle=0.806623 EndAngle=0.851303
    g278: ArcOfCircle CenterX=3.1347 CenterY=47.3965 CenterZ=0 NormalX=0 NormalY=0 NormalZ=1 Radius=2 StartAngle=4.64635 EndAngle=5.32325
    g279: ArcOfCircle CenterX=0 CenterY=0 CenterZ=0 NormalX=0 NormalY=0 NormalZ=1 Radius=45.5 StartAngle=4.64635 EndAngle=4.69103
    g280: ArcOfCircle CenterX=-127.5 CenterY=-220.836 CenterZ=0 NormalX=0 NormalY=0 NormalZ=1 Radius=201.5 StartAngle=1.04653 EndAngle=1.05488
    g281: ArcOfCircle CenterX=0 CenterY=0 CenterZ=0 NormalX=0 NormalY=0 NormalZ=1 Radius=44 StartAngle=0.875625 EndAngle=1.21877
    g282: LineSegment StartX=-3.72902 StartY=45.8065 StartZ=0 EndX=6.92065 EndY=56.4562 EndZ=0
    g283: ArcOfCircle CenterX=44.0254 CenterY=14.967 CenterZ=0 NormalX=0 NormalY=0 NormalZ=1 Radius=1 StartAngle=0.959931 EndAngle=3.4693
    g284: LineSegment StartX=51.6159 StartY=26.0403 StartZ=0 EndX=36.5102 EndY=30.0879 EndZ=0
    g285: ArcOfCircle CenterX=-39.7644 CenterY=24.1048 CenterZ=0 NormalX=0 NormalY=0 NormalZ=1 Radius=1 StartAngle=3.22886 EndAngle=5.73823
    g286: ArcOfCircle CenterX=-29.122 CenterY=36.2514 CenterZ=0 NormalX=0 NormalY=0 NormalZ=1 Radius=1 StartAngle=2.87979 EndAngle=5.38916
    g287: ArcOfCircle CenterX=0 CenterY=0 CenterZ=0 NormalX=0 NormalY=0 NormalZ=1 Radius=58.5 StartAngle=3.73145 EndAngle=3.75696
    g288: ArcOfCircle CenterX=43.466 CenterY=-19.1562 CenterZ=0 NormalX=0 NormalY=0 NormalZ=1 Radius=2 StartAngle=2.72649 EndAngle=3.40339
    g289: Circle CenterX=19.0526 CenterY=-11 CenterZ=0 NormalX=0 NormalY=0 NormalZ=1 Radius=2.75
    g290: ArcOfCircle CenterX=0 CenterY=0 CenterZ=0 NormalX=0 NormalY=0 NormalZ=1 Radius=45.5 StartAngle=0.457557 EndAngle=0.502238
    g291: ArcOfCircle CenterX=-7.09467 CenterY=45.9556 CenterZ=0 NormalX=0 NormalY=0 NormalZ=1 Radius=1 StartAngle=2.35619 EndAngle=4.86556
    g292: ArcOfCircle CenterX=-52.506 CenterY=1.55623 CenterZ=0 NormalX=0 NormalY=0 NormalZ=1 Radius=1 StartAngle=0.785398 EndAngle=3.14928
    g293: LineSegment StartX=34.5926 StartY=41.6858 StartZ=0 EndX=24.0177 EndY=40.7606 EndZ=0
    g294: ArcOfCircle CenterX=36.2514 CenterY=29.122 CenterZ=0 NormalX=0 NormalY=0 NormalZ=1 Radius=1 StartAngle=1.309 EndAngle=3.81836
    g295: ArcOfCircle CenterX=-255 CenterY=0 CenterZ=0 NormalX=0 NormalY=0 NormalZ=1 Radius=200 StartAngle=6.17695 EndAngle=6.38942
    g296: ArcOfCircle CenterX=127.5 CenterY=-220.836 CenterZ=0 NormalX=0 NormalY=0 NormalZ=1 Radius=201.5 StartAngle=2.05315 EndAngle=2.05917
    g297: LineSegment StartX=-52.9143 StartY=-1.55021 StartZ=0 EndX=-46.6627 EndY=-7.80178 EndZ=0
    g298: ArcOfCircle CenterX=0 CenterY=0 CenterZ=0 NormalX=0 NormalY=0 NormalZ=1 Radius=45.5 StartAngle=3.59915 EndAngle=3.64368
    g299: ArcOfCircle CenterX=0 CenterY=0 CenterZ=0 NormalX=0 NormalY=0 NormalZ=1 Radius=45.5 StartAngle=5.51901 EndAngle=5.56369
    g300: ArcOfCircle CenterX=-22.3845 CenterY=40.7576 CenterZ=0 NormalX=0 NormalY=0 NormalZ=1 Radius=1 StartAngle=2.70526 EndAngle=5.21463
    g301: LineSegment StartX=24.8188 StartY=-10 StartZ=0 EndX=40.398 EndY=-10 EndZ=0
    g302: ArcOfCircle CenterX=31.9233 CenterY=27.2929 CenterZ=0 NormalX=0 NormalY=0 NormalZ=1 Radius=2 StartAngle=0.707361 EndAngle=2.61799
    g303: ArcOfCircle CenterX=0 CenterY=0 CenterZ=0 NormalX=0 NormalY=0 NormalZ=1 Radius=60 StartAngle=1.40844 EndAngle=1.73315
    g304: ArcOfCircle CenterX=-19.0526 CenterY=-11 CenterZ=0 NormalX=0 NormalY=0 NormalZ=1 Radius=4.5 StartAngle=4.66852 EndAngle=8.94505
    g305: LineSegment StartX=-39.598 StartY=-12 StartZ=0 EndX=-24.8188 EndY=-12 EndZ=0
    g306: ArcOfCircle CenterX=-39.9023 CenterY=37.155 CenterZ=0 NormalX=0 NormalY=0 NormalZ=1 Radius=2 StartAngle=2.01579 EndAngle=3.22886
    g307: LineSegment StartX=-12.1626 StartY=-44.3194 StartZ=0 EndX=-20.559 EndY=-48.2348 EndZ=0
    g308: ArcOfCircle CenterX=0.285064 CenterY=28.4937 CenterZ=0 NormalX=0 NormalY=0 NormalZ=1 Radius=2 StartAngle=4.66852 EndAngle=5.75959
    g309: ArcOfCircle CenterX=47.7836 CenterY=31.984 CenterZ=0 NormalX=0 NormalY=0 NormalZ=1 Radius=1 StartAngle=4.62512 EndAngle=6.87304
    g310: LineSegment StartX=-19.6738 StartY=-41.5341 StartZ=0 EndX=-27.8595 EndY=-43.7275 EndZ=0
    g311: ArcOfCircle CenterX=-14.967 CenterY=44.0254 CenterZ=0 NormalX=0 NormalY=0 NormalZ=1 Radius=1 StartAngle=2.53073 EndAngle=5.04009
    g312: LineSegment StartX=-52.8202 StartY=-10.0296 StartZ=0 EndX=-44.599 EndY=-15.7861 EndZ=0
    g313: ArcOfCircle CenterX=28.0645 CenterY=-38.3227 CenterZ=0 NormalX=0 NormalY=0 NormalZ=1 Radius=2 StartAngle=2.20289 EndAngle=2.87979
    g314: ArcOfCircle CenterX=-31.9233 CenterY=27.2929 CenterZ=0 NormalX=0 NormalY=0 NormalZ=1 Radius=2 StartAngle=0.523599 EndAngle=2.43423
    g315: ArcOfCircle CenterX=0 CenterY=0 CenterZ=0 NormalX=0 NormalY=0 NormalZ=1 Radius=58.5 StartAngle=3.55692 EndAngle=3.58243
    g316: ArcOfCircle CenterX=0 CenterY=0 CenterZ=0 NormalX=0 NormalY=0 NormalZ=1 Radius=45.5 StartAngle=1.33022 EndAngle=1.3749
    g317: ArcOfCircle CenterX=-18.5695 CenterY=-48.9458 CenterZ=0 NormalX=0 NormalY=0 NormalZ=1 Radius=2 StartAngle=4.14754 EndAngle=5.14872
    g318: ArcOfCircle CenterX=-4.67058 CenterY=-56.3066 CenterZ=0 NormalX=0 NormalY=0 NormalZ=1 Radius=2 StartAngle=4.62963 EndAngle=5.49779
    g319: ArcOfCircle CenterX=-51.5 CenterY=-0.135994 CenterZ=0 NormalX=0 NormalY=0 NormalZ=1 Radius=2 StartAngle=3.14092 EndAngle=3.92699
    g320: ArcOfCircle CenterX=-127.5 CenterY=-220.836 CenterZ=0 NormalX=0 NormalY=0 NormalZ=1 Radius=201.5 StartAngle=0.968596 EndAngle=0.973004
    g321: ArcOfCircle CenterX=0 CenterY=0 CenterZ=0 NormalX=0 NormalY=0 NormalZ=1 Radius=45.5 StartAngle=2.55195 EndAngle=2.59663
    g322: LineSegment StartX=3.72902 StartY=-45.8065 StartZ=0 EndX=-6.92065 EndY=-56.4562 EndZ=0
    g323: ArcOfCircle CenterX=52.6116 CenterY=23.2006 CenterZ=0 NormalX=0 NormalY=0 NormalZ=1 Radius=1 StartAngle=4.45059 EndAngle=6.69851
    g324: ArcOfCircle CenterX=38.3227 CenterY=28.0645 CenterZ=0 NormalX=0 NormalY=0 NormalZ=1 Radius=2 StartAngle=3.77368 EndAngle=4.45059
    g325: ArcOfCircle CenterX=45.6106 CenterY=-9.05093 CenterZ=0 NormalX=0 NormalY=0 NormalZ=1 Radius=1 StartAngle=0.436332 EndAngle=2.9457
    g326: LineSegment StartX=44.4631 StartY=11.6266 StartZ=0 EndX=52.0521 EndY=6.31272 EndZ=0
    g327: ArcOfCircle CenterX=24.8188 CenterY=-8 CenterZ=0 NormalX=0 NormalY=0 NormalZ=1 Radius=2 StartAngle=3.62132 EndAngle=4.71239
    g328: ArcOfCircle CenterX=0 CenterY=0 CenterZ=0 NormalX=0 NormalY=0 NormalZ=1 Radius=60 StartAngle=0.361245 EndAngle=0.685953
    g329: ArcOfCircle CenterX=7.67463 CenterY=-41.2929 CenterZ=0 NormalX=0 NormalY=0 NormalZ=1 Radius=2 StartAngle=4.89615 EndAngle=6.80678
    g330: ArcOfCircle CenterX=127.5 CenterY=220.836 CenterZ=0 NormalX=0 NormalY=0 NormalZ=1 Radius=201.5 StartAngle=4.18812 EndAngle=4.19648
    g331: LineSegment StartX=-3.25637 StartY=-57.7208 StartZ=0 EndX=7.80178 EndY=-46.6627 EndZ=0
    g332: ArcOfCircle CenterX=22.3845 CenterY=-40.7576 CenterZ=0 NormalX=0 NormalY=0 NormalZ=1 Radius=1 StartAngle=5.84685 EndAngle=8.35622
    g333: ArcOfCircle CenterX=0 CenterY=0 CenterZ=0 NormalX=0 NormalY=0 NormalZ=1 Radius=44 StartAngle=1.38703 EndAngle=1.75456
    g334: LineSegment StartX=24.8188 StartY=-12 StartZ=0 EndX=39.598 EndY=-12 EndZ=0
    g335: ArcOfCircle CenterX=-24.8188 CenterY=-14 CenterZ=0 NormalX=0 NormalY=0 NormalZ=1 Radius=2 StartAngle=0.479729 EndAngle=1.5708
    g336: LineSegment StartX=-41.8947 StartY=36.9807 StartZ=0 EndX=-40.7606 EndY=24.0177 EndZ=0
    g337: ArcOfCircle CenterX=-33.1036 CenterY=40.5546 CenterZ=0 NormalX=0 NormalY=0 NormalZ=1 Radius=2 StartAngle=2.05315 EndAngle=3.05433
    g338: ArcOfCircle CenterX=25.6322 CenterY=44.6683 CenterZ=0 NormalX=0 NormalY=0 NormalZ=1 Radius=2 StartAngle=1.04653 EndAngle=1.8326
    g339: ArcOfCircle CenterX=52.6256 CenterY=7.13188 CenterZ=0 NormalX=0 NormalY=0 NormalZ=1 Radius=1 StartAngle=4.10152 EndAngle=6.24796
    g340: ArcOfCircle CenterX=-9.05093 CenterY=-45.6106 CenterZ=0 NormalX=0 NormalY=0 NormalZ=1 Radius=1 StartAngle=5.14872 EndAngle=7.65809
    g341: LineSegment StartX=19.1709 StartY=-41.7686 StartZ=0 EndX=14.5114 EndY=-51.7609 EndZ=0
    g342: LineSegment StartX=-41.5341 StartY=19.6738 StartZ=0 EndX=-45.4322 EndY=34.2216 EndZ=0
    g343: Circle CenterX=0 CenterY=22 CenterZ=0 NormalX=0 NormalY=0 NormalZ=1 Radius=2.75
    g344: ArcOfCircle CenterX=40.398 CenterY=7 CenterZ=0 NormalX=0 NormalY=0 NormalZ=1 Radius=3 StartAngle=0.171572 EndAngle=1.5708
    g345: ArcOfCircle CenterX=25.8678 CenterY=-44.5324 CenterZ=0 NormalX=0 NormalY=0 NormalZ=1 Radius=2 StartAngle=5.23532 EndAngle=6.02139
    g346: LineSegment StartX=48.3595 StartY=-31.6805 StartZ=0 EndX=44.312 EndY=-16.5748 EndZ=0
    g347: ArcOfCircle CenterX=-28.0645 CenterY=38.3227 CenterZ=0 NormalX=0 NormalY=0 NormalZ=1 Radius=2 StartAngle=5.34448 EndAngle=6.02139
    g348: ArcOfCircle CenterX=-24.8188 CenterY=-8 CenterZ=0 NormalX=0 NormalY=0 NormalZ=1 Radius=2 StartAngle=4.71239 EndAngle=5.80346
    g349: ArcOfCircle CenterX=0 CenterY=0 CenterZ=0 NormalX=0 NormalY=0 NormalZ=1 Radius=60 StartAngle=5.59723 EndAngle=5.92194
    g350: ArcOfCircle CenterX=-51.5908 CenterY=25.3898 CenterZ=0 NormalX=0 NormalY=0 NormalZ=1 Radius=1 StartAngle=0.436333 EndAngle=2.68425
    g351: LineSegment StartX=2.01711 StartY=27.4937 StartZ=0 EndX=9.40668 EndY=40.2929 EndZ=0
    g352: LineSegment StartX=51.6159 StartY=26.0403 StartZ=0 EndX=36.5102 EndY=30.0879 EndZ=0
    g353: LineSegment StartX=18.8046 StartY=-50.801 StartZ=0 EndX=23.2909 EndY=-41.1802 EndZ=0
    g354: ArcOfCircle CenterX=-51.7589 CenterY=10.2623 CenterZ=0 NormalX=0 NormalY=0 NormalZ=1 Radius=2 StartAngle=3.19204 EndAngle=3.75246
    g355: LineSegment StartX=53.3972 StartY=-9.11519 StartZ=0 EndX=47.3085 EndY=-0.419643 EndZ=0
    g356: LineSegment StartX=12.1626 StartY=44.3194 StartZ=0 EndX=20.559 EndY=48.2348 EndZ=0
    g357: ArcOfCircle CenterX=-32.4892 CenterY=42.0092 CenterZ=0 NormalX=0 NormalY=0 NormalZ=1 Radius=1 StartAngle=6.19592 EndAngle=8.34235
    g358: ArcOfCircle CenterX=-127.5 CenterY=220.836 CenterZ=0 NormalX=0 NormalY=0 NormalZ=1 Radius=201.5 StartAngle=5.15739 EndAngle=5.16179
    g359: ArcOfCircle CenterX=0 CenterY=0 CenterZ=0 NormalX=0 NormalY=0 NormalZ=1 Radius=58.5 StartAngle=4.77865 EndAngle=4.80416
    g360: ArcOfCircle CenterX=34.9745 CenterY=-30.6437 CenterZ=0 NormalX=0 NormalY=0 NormalZ=1 Radius=1 StartAngle=6.19592 EndAngle=8.70528
    g361: LineSegment StartX=41.8947 StartY=-36.9807 StartZ=0 EndX=40.7606 EndY=-24.0177 EndZ=0
    g362: ArcOfCircle CenterX=46.4894 CenterY=-0.993219 CenterZ=0 NormalX=0 NormalY=0 NormalZ=1 Radius=1 StartAngle=0.610865 EndAngle=3.12023
    g363: ArcOfCircle CenterX=-15.4177 CenterY=52.1835 CenterZ=0 NormalX=0 NormalY=0 NormalZ=1 Radius=1 StartAngle=5.84685 EndAngle=8.44053
    g364: LineSegment StartX=45.8065 StartY=3.72902 StartZ=0 EndX=51.7989 EndY=-2.26334 EndZ=0
    g365: LineSegment StartX=22.8017 StartY=-15.4937 StartZ=0 EndX=30.1913 EndY=-28.2929 EndZ=0
    g366: ArcOfCircle CenterX=52.506 CenterY=-1.55623 CenterZ=0 NormalX=0 NormalY=0 NormalZ=1 Radius=0.999999 StartAngle=3.92699 EndAngle=6.29087
    g367: ArcOfCircle CenterX=-46.4277 CenterY=32.1982 CenterZ=0 NormalX=0 NormalY=0 NormalZ=1 Radius=2 StartAngle=2.53523 EndAngle=3.40339
    g368: ArcOfCircle CenterX=0 CenterY=0 CenterZ=0 NormalX=0 NormalY=0 NormalZ=1 Radius=44 StartAngle=2.97002 EndAngle=3.31316
    g369: ArcOfCircle CenterX=-45.6106 CenterY=9.05093 CenterZ=0 NormalX=0 NormalY=0 NormalZ=1 Radius=1 StartAngle=3.57792 EndAngle=6.08729
    g370: ArcOfCircle CenterX=0 CenterY=0 CenterZ=0 NormalX=0 NormalY=0 NormalZ=1 Radius=58.5 StartAngle=1.46252 EndAngle=1.48804
    g371: ArcOfCircle CenterX=0 CenterY=-22 CenterZ=0 NormalX=0 NormalY=0 NormalZ=1 Radius=4.5 StartAngle=4.66852 EndAngle=4.75626
    g372: ArcOfCircle CenterX=40.398 CenterY=-7 CenterZ=0 NormalX=0 NormalY=0 NormalZ=1 Radius=3 StartAngle=4.71239 EndAngle=6.11161
    g373: ArcOfCircle CenterX=52.9011 CenterY=-12.7396 CenterZ=0 NormalX=0 NormalY=0 NormalZ=1 Radius=1 StartAngle=3.75246 EndAngle=6.34614
    g374: ArcOfCircle CenterX=-26.2612 CenterY=-31.4857 CenterZ=0 NormalX=0 NormalY=0 NormalZ=1 Radius=3 StartAngle=2.61799 EndAngle=4.01722
    g375: ArcOfCircle CenterX=42.6139 CenterY=20.9835 CenterZ=0 NormalX=0 NormalY=0 NormalZ=1 Radius=2 StartAngle=3.59915 EndAngle=4.27606
    g376: ArcOfCircle CenterX=-255 CenterY=0 CenterZ=0 NormalX=0 NormalY=0 NormalZ=1 Radius=201.5 StartAngle=6.20458 EndAngle=6.20899
    g377: ArcOfCircle CenterX=-24.5338 CenterY=14.4937 CenterZ=0 NormalX=0 NormalY=0 NormalZ=1 Radius=2 StartAngle=5.71572 EndAngle=6.80678
    g378: ArcOfCircle CenterX=40.7576 CenterY=22.3845 CenterZ=0 NormalX=0 NormalY=0 NormalZ=1 Radius=1 StartAngle=1.13446 EndAngle=3.64383
    g379: ArcOfCircle CenterX=-43.346 CenterY=16.8336 CenterZ=0 NormalX=0 NormalY=0 NormalZ=1 Radius=0.999999 StartAngle=3.40339 EndAngle=5.91276
    g380: ArcOfCircle CenterX=0 CenterY=0 CenterZ=0 NormalX=0 NormalY=0 NormalZ=1 Radius=45.5 StartAngle=5.86808 EndAngle=5.91276
    g381: ArcOfCircle CenterX=24.1048 CenterY=39.7644 CenterZ=0 NormalX=0 NormalY=0 NormalZ=1 Radius=1 StartAngle=1.65806 EndAngle=4.16743
    g382: LineSegment StartX=44.3194 StartY=-12.1626 StartZ=0 EndX=50.6845 EndY=-25.8124 EndZ=0
    g383: ArcOfCircle CenterX=0 CenterY=0 CenterZ=0 NormalX=0 NormalY=0 NormalZ=1 Radius=44 StartAngle=5.57582 EndAngle=5.94335
    g384: ArcOfCircle CenterX=-45.9556 CenterY=-7.09467 CenterZ=0 NormalX=0 NormalY=0 NormalZ=1 Radius=1 StartAngle=3.92699 EndAngle=6.43636
    g385: ArcOfCircle CenterX=0 CenterY=0 CenterZ=0 NormalX=0 NormalY=0 NormalZ=1 Radius=45.5 StartAngle=0.108491 EndAngle=0.153172
    g386: ArcOfCircle CenterX=-255 CenterY=0 CenterZ=0 NormalX=0 NormalY=0 NormalZ=1 Radius=201.5 StartAngle=6.24194 EndAngle=6.24796
    g387: ArcOfCircle CenterX=0 CenterY=0 CenterZ=0 NormalX=0 NormalY=0 NormalZ=1 Radius=58.5 StartAngle=2.50972 EndAngle=2.53523
    g388: ArcOfCircle CenterX=-30.6437 CenterY=-34.9745 CenterZ=0 NormalX=0 NormalY=0 NormalZ=1 Radius=1 StartAngle=4.62512 EndAngle=7.13449
    g389: ArcOfCircle CenterX=0 CenterY=0 CenterZ=0 NormalX=0 NormalY=0 NormalZ=1 Radius=44 StartAngle=3.48143 EndAngle=3.84895
    g390: LineSegment StartX=-6.81622 StartY=57.4094 StartZ=0 EndX=-15.7861 EndY=44.599 EndZ=0
    g391: Circle CenterX=0 CenterY=-22 CenterZ=0 NormalX=0 NormalY=0 NormalZ=1 Radius=2.75
    g392: ArcOfCircle CenterX=30.6437 CenterY=34.9745 CenterZ=0 NormalX=0 NormalY=0 NormalZ=1 Radius=1 StartAngle=1.48353 EndAngle=3.9929
    g393: ArcOfCircle CenterX=-3.80716 CenterY=57.3738 CenterZ=0 NormalX=0 NormalY=0 NormalZ=1 Radius=1 StartAngle=5.67232 EndAngle=7.92024
    g394: ArcOfCircle CenterX=0 CenterY=0 CenterZ=0 NormalX=0 NormalY=0 NormalZ=1 Radius=44 StartAngle=6.11161 EndAngle=6.45476
    g395: ArcOfCircle CenterX=0 CenterY=0 CenterZ=0 NormalX=0 NormalY=0 NormalZ=1 Radius=44 StartAngle=1.92282 EndAngle=2.26597
    g396: ArcOfCircle CenterX=24.8188 CenterY=-14 CenterZ=0 NormalX=0 NormalY=0 NormalZ=1 Radius=2 StartAngle=1.5708 EndAngle=2.66186
    g397: ArcOfCircle CenterX=-13.5292 CenterY=-53.454 CenterZ=0 NormalX=0 NormalY=0 NormalZ=1 Radius=1 StartAngle=2.18166 EndAngle=4.1146
    g398: LineSegment StartX=52.9143 StartY=1.55021 StartZ=0 EndX=46.6627 EndY=7.80178 EndZ=0
    g399: ArcOfCircle CenterX=34.2928 CenterY=-32.8672 CenterZ=0 NormalX=0 NormalY=0 NormalZ=1 Radius=2 StartAngle=2.37742 EndAngle=3.05433
    ... +20 more geometry lines
FEATURE [Part::Feature] Arc188
  shape: bbox 1.066 x 1.574 x 2e-07 mm, 0 faces, 0 solids (baked)
FEATURE [Part::Feature] Arc276
  shape: bbox 1.887 x 0.8054 x 2e-07 mm, 0 faces, 0 solids (baked)
FEATURE [Part::Feature] Arc170
  shape: bbox 0.08881 x 2.031 x 2e-07 mm, 0 faces, 0 solids (baked)
FEATURE [Part::Feature] Arc189
  shape: bbox 1.553 x 1.423 x 2e-07 mm, 0 faces, 0 solids (baked)
FEATURE [Part::Feature] Arc183
  shape: bbox 1.626 x 1.259 x 2e-07 mm, 0 faces, 0 solids (baked)
FEATURE [Part::Feature] Arc161
  shape: bbox 0.7733 x 1.08 x 2e-07 mm, 0 faces, 0 solids (baked)
FEATURE [Sketcher::SketchObject] Sketch148
  sketch-geometry (1):
    g0: ArcOfCircle CenterX=0 CenterY=0 CenterZ=0 NormalX=0 NormalY=0 NormalZ=1 Radius=58.5 StartAngle=4.60412 EndAngle=4.62963
FEATURE [Sketcher::SketchObject] Sketch017
  sketch-geometry (1):
    g0: ArcOfCircle CenterX=-27.6007 CenterY=-44.6934 CenterZ=0 NormalX=0 NormalY=0 NormalZ=1 Radius=1 StartAngle=1.8326 EndAngle=4.19648
FEATURE [Sketcher::SketchObject] Sketch335
  sketch-geometry (1):
    g0: ArcOfCircle CenterX=27.6007 CenterY=44.6934 CenterZ=0 NormalX=0 NormalY=0 NormalZ=1 Radius=1 StartAngle=4.97419 EndAngle=7.33807
FEATURE [Sketcher::SketchObject] Sketch264
  sketch-geometry (1):
    g0: ArcOfCircle CenterX=0 CenterY=0 CenterZ=0 NormalX=0 NormalY=0 NormalZ=1 Radius=58.5 StartAngle=0.415326 EndAngle=0.440839
FEATURE [Part::Feature] Arc090
  shape: bbox 8.492 x 9 x 2e-07 mm, 0 faces, 0 solids (baked)
FEATURE [Sketcher::SketchObject] Sketch226
  sketch-geometry (1):
    g0: ArcOfCircle CenterX=0 CenterY=0 CenterZ=0 NormalX=0 NormalY=0 NormalZ=1 Radius=45.5 StartAngle=0.283024 EndAngle=0.327705
FEATURE [Sketcher::SketchObject] Sketch215
  sketch-geometry (1):
    g0: Circle CenterX=-19.0526 CenterY=11 CenterZ=0 NormalX=0 NormalY=0 NormalZ=1 Radius=2.75
FEATURE [Part::Feature] Line096
  shape: bbox 0.8747 x 9.998 x 2e-07 mm, 0 faces, 0 solids (baked)
FEATURE [Sketcher::SketchObject] Sketch360
  sketch-geometry (1):
    g0: ArcOfCircle CenterX=-46.4894 CenterY=0.993219 CenterZ=0 NormalX=0 NormalY=0 NormalZ=1 Radius=1 StartAngle=3.75246 EndAngle=6.26182
FEATURE [Sketcher::SketchObject] Sketch146
  sketch-geometry (1):
    g0: ArcOfCircle CenterX=-53.0571 CenterY=-15.0104 CenterZ=0 NormalX=0 NormalY=0 NormalZ=1 Radius=1 StartAngle=1.13446 EndAngle=3.0674
FEATURE [Sketcher::SketchObject] Sketch037
  sketch-geometry (1):
    g0: ArcOfCircle CenterX=-26.413 CenterY=-39.4792 CenterZ=0 NormalX=0 NormalY=0 NormalZ=1 Radius=2 StartAngle=0.981156 EndAngle=1.65806
FEATURE [Sketcher::SketchObject] Sketch217
  sketch-geometry (1):
    g0: ArcOfCircle CenterX=52.1283 CenterY=15.9789 CenterZ=0 NormalX=0 NormalY=0 NormalZ=1 Radius=2 StartAngle=6.20458 EndAngle=7.41765
FEATURE [Sketcher::SketchObject] Sketch182
  sketch-geometry (1):
    g0: ArcOfCircle CenterX=0 CenterY=0 CenterZ=0 NormalX=0 NormalY=0 NormalZ=1 Radius=60 StartAngle=2.45564 EndAngle=2.78035
FEATURE [Sketcher::SketchObject] Sketch006
  sketch-geometry (1):
    g0: ArcOfCircle CenterX=45.6102 CenterY=13.2649 CenterZ=0 NormalX=0 NormalY=0 NormalZ=1 Radius=2 StartAngle=3.42462 EndAngle=4.10152
FEATURE [Sketcher::SketchObject] Sketch145
  sketch-geometry (1):
    g0: LineSegment StartX=3.74917 StartY=-26.4937 StartZ=0 EndX=11.5388 EndY=-39.9857 EndZ=0
FEATURE [Sketcher::SketchObject] Sketch156
  sketch-geometry (1):
    g0: ArcOfCircle CenterX=9.05093 CenterY=45.6106 CenterZ=0 NormalX=0 NormalY=0 NormalZ=1 Radius=1 StartAngle=2.00713 EndAngle=4.51649
FEATURE [Sketcher::SketchObject] Sketch004
  sketch-geometry (1):
    g0: ArcOfCircle CenterX=15.4177 CenterY=-52.1835 CenterZ=0 NormalX=0 NormalY=0 NormalZ=1 Radius=1 StartAngle=2.70526 EndAngle=5.29894
FEATURE [Sketcher::SketchObject] Sketch177
  sketch-geometry (1):
    g0: ArcOfCircle CenterX=0 CenterY=-22 CenterZ=0 NormalX=0 NormalY=0 NormalZ=1 Radius=4.5 StartAngle=5.71572 EndAngle=9.99225
FEATURE [Sketcher::SketchObject] Sketch185
  sketch-geometry (1):
    g0: ArcOfCircle CenterX=0 CenterY=0 CenterZ=0 NormalX=0 NormalY=0 NormalZ=1 Radius=45.5 StartAngle=1.50475 EndAngle=1.54929
FEATURE [Sketcher::SketchObject] Sketch173
  sketch-geometry (1):
    g0: LineSegment StartX=-34.5926 StartY=-41.6858 StartZ=0 EndX=-24.0177 EndY=-40.7606 EndZ=0
FEATURE [Sketcher::SketchObject] Sketch065
  sketch-geometry (1):
    g0: ArcOfCircle CenterX=-6.21354 CenterY=-57.1633 CenterZ=0 NormalX=0 NormalY=0 NormalZ=1 Radius=1 StartAngle=2.35619 EndAngle=4.60412
FEATURE [Sketcher::SketchObject] Sketch363
  sketch-geometry (1):
    g0: ArcOfCircle CenterX=34.7669 CenterY=39.6934 CenterZ=0 NormalX=0 NormalY=0 NormalZ=1 Radius=2 StartAngle=1.09765 EndAngle=1.65806
FEATURE [Sketcher::SketchObject] Sketch142
  sketch-geometry (1):
    g0: LineSegment StartX=-45.7581 StartY=4.28185 StartZ=0 EndX=-52.082 EndY=13.3132 EndZ=0
FEATURE [Part::Feature] Arc252
  shape: bbox 1.279 x 0.3617 x 2e-07 mm, 0 faces, 0 solids (baked)
FEATURE [Part::Feature] Arc076
  shape: bbox 0.646 x 15.02 x 2e-07 mm, 0 faces, 0 solids (baked)
FEATURE [Part::Feature] Arc060
  shape: bbox 1.82 x 1 x 2e-07 mm, 0 faces, 0 solids (baked)
FEATURE [Part::Feature] Arc317
  shape: bbox 1.752 x 1.087 x 2e-07 mm, 0 faces, 0 solids (baked)
FEATURE [Part::Feature] Arc206
  shape: bbox 0.5485 x 1.21 x 2e-07 mm, 0 faces, 0 solids (baked)
FEATURE [Part::Feature] Line095
  shape: bbox 1.045 x 11.94 x 2e-07 mm, 0 faces, 0 solids (baked)
FEATURE [Part::Feature] Arc039
  shape: bbox 3.252 x 1 x 2e-07 mm, 0 faces, 0 solids (baked)
FEATURE [Part::Feature] Arc177
  shape: bbox 1.423 x 1.481 x 2e-07 mm, 0 faces, 0 solids (baked)
FEATURE [Part::Feature] Arc235
  shape: bbox 0.7412 x 1.836 x 2e-07 mm, 0 faces, 0 solids (baked)
FEATURE [Part::Feature] Arc087
  shape: bbox 0.1974 x 0.3418 x 2e-07 mm, 0 faces, 0 solids (baked)
FEATURE [Part::Feature] Arc275
  shape: bbox 1.898 x 0.7412 x 2e-07 mm, 0 faces, 0 solids (baked)
FEATURE [Sketcher::SketchObject] Sketch181
  sketch-geometry (1):
    g0: LineSegment StartX=-40.398 StartY=-10 StartZ=0 EndX=-24.8188 EndY=-10 EndZ=0
FEATURE [Sketcher::SketchObject] Sketch214
  sketch-geometry (1):
    g0: ArcOfCircle CenterX=0 CenterY=0 CenterZ=0 NormalX=0 NormalY=0 NormalZ=1 Radius=45.5 StartAngle=4.82088 EndAngle=4.86556
FEATURE [Part::Feature] Arc221
  shape: bbox 1.488 x 0.1178 x 2e-07 mm, 0 faces, 0 solids (baked)
FEATURE [Part::Feature] Arc122
  shape: bbox 1.985 x 0.4401 x 2e-07 mm, 0 faces, 0 solids (baked)
FEATURE [Part::Feature] Line075
  shape: bbox 15 x 1.313 x 2e-07 mm, 0 faces, 0 solids (baked)
FEATURE [Part::Feature] Arc145
  shape: bbox 1.707 x 1.008 x 2e-07 mm, 0 faces, 0 solids (baked)
FEATURE [Part::Feature] Line049
  shape: bbox 4.048 x 15.11 x 2e-07 mm, 0 faces, 0 solids (baked)
FEATURE [Part::Feature] Arc057
  shape: bbox 1.774 x 1.077 x 2e-07 mm, 0 faces, 0 solids (baked)
FEATURE [Part::Feature] Arc146
  shape: bbox 1.573 x 0.9648 x 2e-07 mm, 0 faces, 0 solids (baked)
FEATURE [Part::Feature] Arc140
  shape: bbox 1.898 x 0.7412 x 2e-07 mm, 0 faces, 0 solids (baked)
FEATURE [Part::Feature] Arc115
  shape: bbox 1.324 x 0.1699 x 2e-07 mm, 0 faces, 0 solids (baked)
FEATURE [Part::Feature] Arc169
  shape: bbox 0.005951 x 1.683 x 2e-07 mm, 0 faces, 0 solids (baked)
FEATURE [Part::Feature] Arc316
  shape: bbox 1.898 x 0.7412 x 2e-07 mm, 0 faces, 0 solids (baked)
FEATURE [Part::Feature] Arc305
  shape: bbox 0.08881 x 2.031 x 2e-07 mm, 0 faces, 0 solids (baked)
FEATURE [Part::Feature] Arc095
  shape: bbox 1.259 x 1.626 x 2e-07 mm, 0 faces, 0 solids (baked)
FEATURE [Part::Feature] Line102
  shape: bbox 8.97 x 12.81 x 2e-07 mm, 0 faces, 0 solids (baked)
FEATURE [Sketcher::SketchObject] Sketch279
  sketch-geometry (1):
    g0: LineSegment StartX=52.9735 StartY=17.7915 StartZ=0 EndX=41.1802 EndY=23.2909 EndZ=0
FEATURE [Part::Feature] Arc103
  shape: bbox 0.8919 x 1.701 x 2e-07 mm, 0 faces, 0 solids (baked)
FEATURE [Part::Feature] Arc168
  shape: bbox 0.04637 x 1.212 x 2e-07 mm, 0 faces, 0 solids (baked)
FEATURE [Sketcher::SketchObject] Sketch067
  sketch-geometry (1):
    g0: ArcOfCircle CenterX=19.0526 CenterY=11 CenterZ=0 NormalX=0 NormalY=0 NormalZ=1 Radius=4.5 StartAngle=1.52693 EndAngle=5.80346
FEATURE [Part::Feature] Arc231
  shape: bbox 1.087 x 1.752 x 2e-07 mm, 0 faces, 0 solids (baked)
FEATURE [Part::Feature] Arc249
  shape: bbox 1.286 x 0.3377 x 2e-07 mm, 0 faces, 0 solids (baked)
FEATURE [Part::Feature] Arc214
  shape: bbox 1.455 x 0.8467 x 2e-07 mm, 0 faces, 0 solids (baked)
FEATURE [Part::Feature] Arc077
  shape: bbox 8.04 x 13.93 x 2e-07 mm, 0 faces, 0 solids (baked)
FEATURE [Part::Feature] Arc141
  shape: bbox 1.887 x 0.8054 x 2e-07 mm, 0 faces, 0 solids (baked)
FEATURE [Part::Feature] Arc296
  shape: bbox 0.7733 x 1.08 x 2e-07 mm, 0 faces, 0 solids (baked)
FEATURE [Sketcher::SketchObject] Sketch243
  sketch-geometry (1):
    g0: ArcOfCircle CenterX=-14.1368 CenterY=38.4857 CenterZ=0 NormalX=0 NormalY=0 NormalZ=1 Radius=3 StartAngle=0.523599 EndAngle=1.92282
FEATURE [Part::Feature] Arc290
  shape: bbox 0.1874 x 1.682 x 2e-07 mm, 0 faces, 0 solids (baked)
FEATURE [Part::Feature] Arc356
  shape: bbox 1.488 x 0.1178 x 2e-07 mm, 0 faces, 0 solids (baked)
FEATURE [Part::Feature] Line078
  shape: bbox 10.65 x 10.65 x 2e-07 mm, 0 faces, 0 solids (baked)
FEATURE [Sketcher::SketchObject] Sketch368
  sketch-geometry (1):
    g0: ArcOfCircle CenterX=-47.3965 CenterY=3.1347 CenterZ=0 NormalX=0 NormalY=0 NormalZ=1 Radius=2 StartAngle=6.21714 EndAngle=6.89405
FEATURE [Sketcher::SketchObject] Sketch384
  sketch-geometry (1):
    g0: ArcOfCircle CenterX=43.346 CenterY=-16.8336 CenterZ=0 NormalX=0 NormalY=0 NormalZ=1 Radius=1 StartAngle=0.261799 EndAngle=2.77117
FEATURE [Part::Feature] Arc006
  shape: bbox 9.698 x 16.8 x 2e-07 mm, 0 faces, 0 solids (baked)
FEATURE [Part::Feature] Arc053
  shape: bbox 0.3135 x 2.075 x 2e-07 mm, 0 faces, 0 solids (baked)
FEATURE [Part::Feature] Arc005
  shape: bbox 9.698 x 16.8 x 2e-07 mm, 0 faces, 0 solids (baked)
FEATURE [Part::Feature] Line107
  shape: bbox 1.134 x 12.96 x 2e-07 mm, 0 faces, 0 solids (baked)
FEATURE [Part::Feature] Arc205
  shape: bbox 0.7502 x 1.096 x 2e-07 mm, 0 faces, 0 solids (baked)
FEATURE [Part::Feature] Line006
  shape: bbox 15.58 x 2e-07 x 2e-07 mm, 0 faces, 0 solids (baked)
FEATURE [Part::Feature] Line005
  shape: bbox 15.58 x 2e-07 x 2e-07 mm, 0 faces, 0 solids (baked)
FEATURE [Part::Feature] Arc295
  shape: bbox 0.574 x 1.198 x 2e-07 mm, 0 faces, 0 solids (baked)
FEATURE [Part::Feature] Arc132
  shape: bbox 0.9786 x 1.819 x 2e-07 mm, 0 faces, 0 solids (baked)
FEATURE [Part::Feature] Line004
  shape: bbox 14.78 x 2e-07 x 2e-07 mm, 0 faces, 0 solids (baked)
FEATURE [Part::Feature] Line103
  shape: bbox 8.639 x 12.34 x 2e-07 mm, 0 faces, 0 solids (baked)
FEATURE [Part::Feature] Line050
  shape: bbox 14.55 x 3.898 x 2e-07 mm, 0 faces, 0 solids (baked)
FEATURE [Part::Feature] Line091
  shape: bbox 4.048 x 15.11 x 2e-07 mm, 0 faces, 0 solids (baked)
FEATURE [Part::Feature] Line074
  shape: bbox 15.58 x 1.363 x 2e-07 mm, 0 faces, 0 solids (baked)
FEATURE [Part::Feature] Line064
  shape: bbox 3.898 x 14.55 x 2e-07 mm, 0 faces, 0 solids (baked)
FEATURE [Sketcher::SketchObject] Sketch027
  sketch-geometry (1):
    g0: ArcOfCircle CenterX=43.346 CenterY=-16.8336 CenterZ=0 NormalX=0 NormalY=0 NormalZ=1 Radius=1 StartAngle=0.261799 EndAngle=2.77117
FEATURE [Part::Feature] Arc004
  shape: bbox 36.73 x 21.21 x 2e-07 mm, 0 faces, 0 solids (baked)
FEATURE [Sketcher::SketchObject] Sketch007
  sketch-geometry (1):
    g0: ArcOfCircle CenterX=-19.0526 CenterY=11 CenterZ=0 NormalX=0 NormalY=0 NormalZ=1 Radius=4.5 StartAngle=3.62132 EndAngle=7.89785
FEATURE [Sketcher::SketchObject] Sketch285
  sketch-geometry (1):
    g0: ArcOfCircle CenterX=31.9233 CenterY=-27.2929 CenterZ=0 NormalX=0 NormalY=0 NormalZ=1 Radius=2 StartAngle=3.66519 EndAngle=5.57582
FEATURE [Sketcher::SketchObject] Sketch103
  sketch-geometry (1):
    g0: ArcOfCircle CenterX=127.5 CenterY=220.836 CenterZ=0 NormalX=0 NormalY=0 NormalZ=1 Radius=201.5 StartAngle=4.11019 EndAngle=4.1146
FEATURE [Part::Feature] Arc244
  shape: bbox 1.086 x 0.2197 x 2e-07 mm, 0 faces, 0 solids (baked)
FEATURE [Part::Feature] Line101
  shape: bbox 4.659 x 9.992 x 2e-07 mm, 0 faces, 0 solids (baked)
FEATURE [Part::Feature] Arc079
  shape: bbox 0.3947 x 0.00433 x 2e-07 mm, 0 faces, 0 solids (baked)
FEATURE [Sketcher::SketchObject] Sketch306
  sketch-geometry (1):
    g0: LineSegment StartX=-26.1327 StartY=37.8051 StartZ=0 EndX=-23.9393 EndY=45.9908 EndZ=0
FEATURE [Part::Feature] Arc003
  shape: bbox 36.73 x 21.21 x 2e-07 mm, 0 faces, 0 solids (baked)
FEATURE [Part::Feature] Arc238
  shape: bbox 0.8919 x 1.701 x 2e-07 mm, 0 faces, 0 solids (baked)
FEATURE [Part::Feature] Arc322
  shape: bbox 0.8919 x 1.701 x 2e-07 mm, 0 faces, 0 solids (baked)
FEATURE [Part::Feature] Arc082
  shape: bbox 8.492 x 9 x 2e-07 mm, 0 faces, 0 solids (baked)
FEATURE [Sketcher::SketchObject] Sketch400
  sketch-geometry (1):
    g0: ArcOfCircle CenterX=51.5908 CenterY=-25.3898 CenterZ=0 NormalX=0 NormalY=0 NormalZ=1 Radius=1 StartAngle=3.57792 EndAngle=5.82585
FEATURE [Part::Feature] Arc357
  shape: bbox 1.851 x 0.9128 x 2e-07 mm, 0 faces, 0 solids (baked)
FEATURE [Part::Feature] Line048
  shape: bbox 3.898 x 14.55 x 2e-07 mm, 0 faces, 0 solids (baked)
FEATURE [Part::Feature] Arc345
  shape: bbox 0.8009 x 0.3841 x 2e-07 mm, 0 faces, 0 solids (baked)
FEATURE [Part::Feature] Arc332
  shape: bbox 1.065 x 1.598 x 2e-07 mm, 0 faces, 0 solids (baked)
FEATURE [Part::Feature] Arc051
  shape: bbox 1.774 x 1.077 x 2e-07 mm, 0 faces, 0 solids (baked)
FEATURE [Part::Feature] Arc097
  shape: bbox 1.259 x 1.403 x 2e-07 mm, 0 faces, 0 solids (baked)
FEATURE [Part::Feature] Line085
  shape: bbox 6.252 x 6.252 x 2e-07 mm, 0 faces, 0 solids (baked)
FEATURE [Part::Feature] Arc002
  shape: bbox 1.127 x 42.41 x 2e-07 mm, 0 faces, 0 solids (baked)
FEATURE [Part::Feature] Line003
  shape: bbox 7.39 x 12.8 x 2e-07 mm, 0 faces, 0 solids (baked)
FEATURE [Part::Feature] Arc222
  shape: bbox 1.851 x 0.9128 x 2e-07 mm, 0 faces, 0 solids (baked)
FEATURE [Part::Feature] Arc055
  shape: bbox 1.82 x 1 x 2e-07 mm, 0 faces, 0 solids (baked)
FEATURE [Sketcher::SketchObject] Sketch251
  sketch-geometry (1):
    g0: ArcOfCircle CenterX=38.3227 CenterY=28.0645 CenterZ=0 NormalX=0 NormalY=0 NormalZ=1 Radius=2 StartAngle=3.77368 EndAngle=4.45059
FEATURE [Part::Feature] Arc069
  shape: bbox 8.04 x 13.93 x 2e-07 mm, 0 faces, 0 solids (baked)
FEATURE [Part::Feature] Line057
  shape: bbox 2.288 x 8.54 x 2e-07 mm, 0 faces, 0 solids (baked)
FEATURE [Part::Feature] Line002
  shape: bbox 7.79 x 13.49 x 2e-07 mm, 0 faces, 0 solids (baked)
FEATURE [Part::Feature] Arc045
  shape: bbox 1.774 x 1.077 x 2e-07 mm, 0 faces, 0 solids (baked)
FEATURE [Part::Feature] Arc001
  shape: bbox 36.73 x 21.21 x 2e-07 mm, 0 faces, 0 solids (baked)
FEATURE [Part::Feature] Arc153
  shape: bbox 0.5858 x 1.416 x 2e-07 mm, 0 faces, 0 solids (baked)
FEATURE [Part::Feature] Arc054
  shape: bbox 1.82 x 1 x 2e-07 mm, 0 faces, 0 solids (baked)
FEATURE [Part::Feature] Line001
  shape: bbox 7.79 x 13.49 x 2e-07 mm, 0 faces, 0 solids (baked)
FEATURE [Part::Feature] Line080
  shape: bbox 15.11 x 4.048 x 2e-07 mm, 0 faces, 0 solids (baked)
FEATURE [Part::Feature] Arc186
  shape: bbox 1.322 x 1.574 x 2e-07 mm, 0 faces, 0 solids (baked)
FEATURE [Part::Feature] Arc065
  shape: bbox 0.3135 x 2.075 x 2e-07 mm, 0 faces, 0 solids (baked)
FEATURE [Part::Feature] Line081
  shape: bbox 10.87 x 5.067 x 2e-07 mm, 0 faces, 0 solids (baked)
FEATURE [Part::Feature] Arc312
  shape: bbox 1.423 x 1.481 x 2e-07 mm, 0 faces, 0 solids (baked)
FEATURE [Part::Feature] Line088
  shape: bbox 6.609 x 14.17 x 2e-07 mm, 0 faces, 0 solids (baked)
FEATURE [Part::Feature] Arc106
  shape: bbox 2.28 x 0.3617 x 2e-07 mm, 0 faces, 0 solids (baked)
FEATURE [Part::Feature] Arc241
  shape: bbox 2.28 x 0.3617 x 2e-07 mm, 0 faces, 0 solids (baked)
FEATURE [Part::Feature] Arc083
  shape: bbox 0.1974 x 0.3418 x 2e-07 mm, 0 faces, 0 solids (baked)
FEATURE [Sketcher::SketchObject] Sketch064
  sketch-geometry (1):
    g0: ArcOfCircle CenterX=-127.5 CenterY=-220.836 CenterZ=0 NormalX=0 NormalY=0 NormalZ=1 Radius=200 StartAngle=0.940966 EndAngle=1.15343
FEATURE [Part::Feature] Arc279
  shape: bbox 1.819 x 1.063 x 2e-07 mm, 0 faces, 0 solids (baked)
FEATURE [Part::Feature] Line
  shape: bbox 7.39 x 12.8 x 2e-07 mm, 0 faces, 0 solids (baked)
FEATURE [Part::Feature] Arc339
  shape: bbox 0.9291 x 0.949 x 2e-07 mm, 0 faces, 0 solids (baked)
FEATURE [Part::Feature] Arc272
  shape: bbox 1.574 x 1.322 x 2e-07 mm, 0 faces, 0 solids (baked)
FEATURE [Part::Feature] Arc125
  shape: bbox 1.714 x 1.092 x 2e-07 mm, 0 faces, 0 solids (baked)
FEATURE [Part::Feature] Arc157
  shape: bbox 0.3565 x 1.657 x 2e-07 mm, 0 faces, 0 solids (baked)
FEATURE [Part::Feature] Arc
  shape: bbox 36.73 x 21.21 x 2e-07 mm, 0 faces, 0 solids (baked)
FEATURE [Part::Feature] Line068
  shape: bbox 9.096 x 4.242 x 2e-07 mm, 0 faces, 0 solids (baked)
FEATURE [Part::Feature] Arc120
  shape: bbox 0.7331 x 0.5015 x 2e-07 mm, 0 faces, 0 solids (baked)
FEATURE [Part::Feature] Arc264
  shape: bbox 1.878 x 0.778 x 2e-07 mm, 0 faces, 0 solids (baked)
FEATURE [Part::Feature] Arc350
  shape: bbox 1.803 x 0.9385 x 2e-07 mm, 0 faces, 0 solids (baked)
FEATURE [Part::Feature] Arc309
  shape: bbox 0.2652 x 2.015 x 2e-07 mm, 0 faces, 0 solids (baked)
FEATURE [Part::Feature] Arc047
  shape: bbox 0.3135 x 2.075 x 2e-07 mm, 0 faces, 0 solids (baked)
FEATURE [Part::Feature] Arc200
  shape: bbox 1.455 x 0.8444 x 2e-07 mm, 0 faces, 0 solids (baked)
FEATURE [Part::Feature] Arc216
  shape: bbox 1.939 x 0.6111 x 2e-07 mm, 0 faces, 0 solids (baked)
FEATURE [Part::Feature] Line052
  shape: bbox 4.048 x 15.11 x 2e-07 mm, 0 faces, 0 solids (baked)
FEATURE [Part::Feature] Arc107
  shape: bbox 1.916 x 0.3107 x 2e-07 mm, 0 faces, 0 solids (baked)
FEATURE [Part::Feature] Arc302
  shape: bbox 0.6111 x 1.939 x 2e-07 mm, 0 faces, 0 solids (baked)
FEATURE [Part::Feature] Arc136
  shape: bbox 1.259 x 1.626 x 2e-07 mm, 0 faces, 0 solids (baked)
FEATURE [Part::Feature] Arc349
  shape: bbox 1.455 x 0.8467 x 2e-07 mm, 0 faces, 0 solids (baked)
FEATURE [Part::Feature] Arc046
  shape: bbox 1.774 x 1.077 x 2e-07 mm, 0 faces, 0 solids (baked)
FEATURE [Part::Feature] Arc273
  shape: bbox 1.707 x 1.153 x 2e-07 mm, 0 faces, 0 solids (baked)
FEATURE [Part::Feature] Arc287
  shape: bbox 0.8528 x 1.721 x 2e-07 mm, 0 faces, 0 solids (baked)
FEATURE [Part::Feature] Arc204
  shape: bbox 0.9291 x 0.949 x 2e-07 mm, 0 faces, 0 solids (baked)
FEATURE [Part::Feature] Line007
  shape: bbox 14.78 x 2e-07 x 2e-07 mm, 0 faces, 0 solids (baked)
FEATURE [Part::Feature] Arc131
  shape: bbox 0.8459 x 1.23 x 2e-07 mm, 0 faces, 0 solids (baked)
FEATURE [Part::Feature] Arc126
  shape: bbox 1.499 x 1.373 x 2e-07 mm, 0 faces, 0 solids (baked)
FEATURE [Part::Feature] Arc199
  shape: bbox 0.7265 x 0.8342 x 2e-07 mm, 0 faces, 0 solids (baked)
FEATURE [Part::Feature] Arc085
  shape: bbox 0.3947 x 0.00433 x 2e-07 mm, 0 faces, 0 solids (baked)
FEATURE [Part::Feature] Arc062
  shape: bbox 0.3135 x 2.075 x 2e-07 mm, 0 faces, 0 solids (baked)
FEATURE [Part::Feature] Line083
  shape: bbox 7.589 x 5.314 x 2e-07 mm, 0 faces, 0 solids (baked)
FEATURE [Part::Feature] Arc098
  shape: bbox 1.087 x 1.556 x 2e-07 mm, 0 faces, 0 solids (baked)
FEATURE [Part::Feature] Arc215
  shape: bbox 1.803 x 0.9385 x 2e-07 mm, 0 faces, 0 solids (baked)
FEATURE [Part::Feature] Arc320
  shape: bbox 1.153 x 1.707 x 2e-07 mm, 0 faces, 0 solids (baked)
FEATURE [Part::Feature] Line014
  shape: bbox 7.79 x 13.49 x 2e-07 mm, 0 faces, 0 solids (baked)
FEATURE [Part::Feature] Arc043
  shape: bbox 1.82 x 1 x 2e-07 mm, 0 faces, 0 solids (baked)
FEATURE [Part::Feature] Arc331
  shape: bbox 1.139 x 1.98 x 2e-07 mm, 0 faces, 0 solids (baked)
FEATURE [Part::Feature] Arc280
  shape: bbox 1.707 x 1.008 x 2e-07 mm, 0 faces, 0 solids (baked)
FEATURE [Part::Feature] Arc105
  shape: bbox 1.198 x 0.574 x 2e-07 mm, 0 faces, 0 solids (baked)
FEATURE [Part::Feature] Arc323
  shape: bbox 1.066 x 1.574 x 2e-07 mm, 0 faces, 0 solids (baked)
FEATURE [Part::Feature] Line013
  shape: bbox 7.79 x 13.49 x 2e-07 mm, 0 faces, 0 solids (baked)
FEATURE [Part::Feature] Arc155
  shape: bbox 0.1874 x 1.682 x 2e-07 mm, 0 faces, 0 solids (baked)
FEATURE [Part::Feature] Line012
  shape: bbox 7.39 x 12.8 x 2e-07 mm, 0 faces, 0 solids (baked)
FEATURE [Part::Feature] Arc154
  shape: bbox 0.3592 x 1.046 x 2e-07 mm, 0 faces, 0 solids (baked)
FEATURE [Part::Feature] Arc040
  shape: bbox 1.635 x 2.966 x 2e-07 mm, 0 faces, 0 solids (baked)
FEATURE [Part::Feature] Line011
  shape: bbox 7.39 x 12.8 x 2e-07 mm, 0 faces, 0 solids (baked)
FEATURE [Part::Feature] Circle004
  shape: bbox 5.5 x 5.5 x 2e-07 mm, 0 faces, 0 solids (baked)
FEATURE [Part::Feature] Line087
  shape: bbox 6.324 x 9.031 x 2e-07 mm, 0 faces, 0 solids (baked)
FEATURE [Part::Feature] Circle
  shape: bbox 5.5 x 5.5 x 2e-07 mm, 0 faces, 0 solids (baked)
FEATURE [Part::Feature] Arc166
  shape: bbox 0.9353 x 1.797 x 2e-07 mm, 0 faces, 0 solids (baked)
FEATURE [Part::Feature] Line010
  shape: bbox 7.79 x 13.49 x 2e-07 mm, 0 faces, 0 solids (baked)
FEATURE [Part::Feature] Arc282
  shape: bbox 1.42 x 0.9259 x 2e-07 mm, 0 faces, 0 solids (baked)
FEATURE [Part::Feature] Line071
  shape: bbox 8.54 x 2.288 x 2e-07 mm, 0 faces, 0 solids (baked)
FEATURE [Part::Feature] Arc218
  shape: bbox 1.486 x 0.1423 x 2e-07 mm, 0 faces, 0 solids (baked)
FEATURE [Part::Feature] Arc066
  shape: bbox 1.82 x 1 x 2e-07 mm, 0 faces, 0 solids (baked)
FEATURE [Part::Feature] Arc007
  shape: bbox 19.4 x 0.789 x 2e-07 mm, 0 faces, 0 solids (baked)
FEATURE [Part::Feature] Arc308
  shape: bbox 0.8661 x 1.215 x 2e-07 mm, 0 faces, 0 solids (baked)
FEATURE [Part::Feature] Line062
  shape: bbox 10.65 x 10.65 x 2e-07 mm, 0 faces, 0 solids (baked)
FEATURE [Part::Feature] Arc056
  shape: bbox 0.3135 x 2.075 x 2e-07 mm, 0 faces, 0 solids (baked)
FEATURE [Part::Feature] Arc190
  shape: bbox 1.507 x 1.259 x 2e-07 mm, 0 faces, 0 solids (baked)
FEATURE [Part::Feature] Arc297
  shape: bbox 0.949 x 0.9291 x 2e-07 mm, 0 faces, 0 solids (baked)
FEATURE [Part::Feature] Arc092
  shape: bbox 0.8054 x 1.887 x 2e-07 mm, 0 faces, 0 solids (baked)
FEATURE [Part::Feature] Arc319
  shape: bbox 1.481 x 1.423 x 2e-07 mm, 0 faces, 0 solids (baked)
FEATURE [Sketcher::SketchObject] Sketch220
  sketch-geometry (1):
    g0: ArcOfCircle CenterX=-46.1321 CenterY=11.3174 CenterZ=0 NormalX=0 NormalY=0 NormalZ=1 Radius=2 StartAngle=6.04261 EndAngle=6.71952
FEATURE [Part::Feature] Line093
  shape: bbox 11.79 x 5.499 x 2e-07 mm, 0 faces, 0 solids (baked)
FEATURE [Part::Feature] Line009
  shape: bbox 7.79 x 13.49 x 2e-07 mm, 0 faces, 0 solids (baked)
FEATURE [Sketcher::SketchObject] Sketch353
  sketch-geometry (1):
    g0: ArcOfCircle CenterX=20.1364 CenterY=49.1411 CenterZ=0 NormalX=0 NormalY=0 NormalZ=1 Radius=1 StartAngle=5.14872 EndAngle=7.29516
FEATURE [Part::Feature] Arc251
  shape: bbox 1.322 x 0.1874 x 2e-07 mm, 0 faces, 0 solids (baked)
FEATURE [Part::Feature] Line008
  shape: bbox 7.39 x 12.8 x 2e-07 mm, 0 faces, 0 solids (baked)
FEATURE [Part::Feature] Arc061
  shape: bbox 1.82 x 1 x 2e-07 mm, 0 faces, 0 solids (baked)
FEATURE [Sketcher::SketchObject] Sketch203
  sketch-geometry (1):
    g0: ArcOfCircle CenterX=-47.7836 CenterY=-31.984 CenterZ=0 NormalX=0 NormalY=0 NormalZ=1 Radius=1 StartAngle=1.48353 EndAngle=3.73145
FEATURE [Part::Feature] Line067
  shape: bbox 9.821 x 6.877 x 2e-07 mm, 0 faces, 0 solids (baked)
FEATURE [Part::Feature] Arc228
  shape: bbox 0.7412 x 1.898 x 2e-07 mm, 0 faces, 0 solids (baked)
FEATURE [Sketcher::SketchObject] Sketch213
  sketch-geometry (1):
    g0: ArcOfCircle CenterX=-0.993219 CenterY=-46.4894 CenterZ=0 NormalX=0 NormalY=0 NormalZ=1 Radius=1 StartAngle=5.32325 EndAngle=7.83262
FEATURE [Part::Feature] Arc011
  shape: bbox 1.127 x 42.41 x 2e-07 mm, 0 faces, 0 solids (baked)
FEATURE [Part::Feature] Arc010
  shape: bbox 19.4 x 0.789 x 2e-07 mm, 0 faces, 0 solids (baked)
FEATURE [Sketcher::SketchObject] Sketch374
  sketch-geometry (1):
    g0: ArcOfCircle CenterX=33.1036 CenterY=-40.5546 CenterZ=0 NormalX=0 NormalY=0 NormalZ=1 Radius=2 StartAngle=5.19474 EndAngle=6.19592
FEATURE [Sketcher::SketchObject] Sketch236
  sketch-geometry (1):
    g0: LineSegment StartX=11.6266 StartY=-44.4631 StartZ=0 EndX=2.988 EndY=-56.8002 EndZ=0
FEATURE [Sketcher::SketchObject] Sketch101
  sketch-geometry (1):
    g0: ArcOfCircle CenterX=127.5 CenterY=220.836 CenterZ=0 NormalX=0 NormalY=0 NormalZ=1 Radius=200 StartAngle=4.08256 EndAngle=4.29502
FEATURE [Part::Feature] Line086
  shape: bbox 6.089 x 8.696 x 2e-07 mm, 0 faces, 0 solids (baked)
FEATURE [Sketcher::SketchObject] Sketch326
  sketch-geometry (1):
    g0: ArcOfCircle CenterX=-255 CenterY=0 CenterZ=0 NormalX=0 NormalY=0 NormalZ=1 Radius=201.5 StartAngle=6.28252 EndAngle=6.29087
FEATURE [Sketcher::SketchObject] Sketch192
  sketch-geometry (1):
    g0: ArcOfCircle CenterX=-39.598 CenterY=-14 CenterZ=0 NormalX=0 NormalY=0 NormalZ=1 Radius=2 StartAngle=1.5708 EndAngle=3.48143
FEATURE [Sketcher::SketchObject] Sketch272
  sketch-geometry (1):
    g0: ArcOfCircle CenterX=-24.8188 CenterY=8 CenterZ=0 NormalX=0 NormalY=0 NormalZ=1 Radius=2 StartAngle=0.479729 EndAngle=1.5708
FEATURE [Sketcher::SketchObject] Sketch100
  sketch-geometry (1):
    g0: ArcOfCircle CenterX=46.4277 CenterY=-32.1982 CenterZ=0 NormalX=0 NormalY=0 NormalZ=1 Radius=2 StartAngle=5.67683 EndAngle=6.54498
FEATURE [Part::Feature] Line015
  shape: bbox 7.39 x 12.8 x 2e-07 mm, 0 faces, 0 solids (baked)
FEATURE [Sketcher::SketchObject] Sketch315
  sketch-geometry (1):
    g0: ArcOfCircle CenterX=-127.5 CenterY=-220.836 CenterZ=0 NormalX=0 NormalY=0 NormalZ=1 Radius=201.5 StartAngle=1.09765 EndAngle=1.11015
FEATURE [Part::Feature] Arc059
  shape: bbox 0.3135 x 2.075 x 2e-07 mm, 0 faces, 0 solids (baked)
FEATURE [Part::Feature] Arc327
  shape: bbox 1.431 x 0.9128 x 2e-07 mm, 0 faces, 0 solids (baked)
FEATURE [Part::Feature] Arc165
  shape: bbox 0.06779 x 0.8856 x 2e-07 mm, 0 faces, 0 solids (baked)
FEATURE [Part::Feature] Line022
  shape: bbox 7.79 x 13.49 x 2e-07 mm, 0 faces, 0 solids (baked)
FEATURE [Sketcher::SketchObject] Sketch284
  sketch-geometry (1):
    g0: ArcOfCircle CenterX=-24.1048 CenterY=-39.7644 CenterZ=0 NormalX=0 NormalY=0 NormalZ=1 Radius=1 StartAngle=4.79966 EndAngle=7.30902
FEATURE [Part::Feature] Line072
  shape: bbox 10.57 x 0.9252 x 2e-07 mm, 0 faces, 0 solids (baked)
FEATURE [Part::Feature] Line021
  shape: bbox 7.79 x 13.49 x 2e-07 mm, 0 faces, 0 solids (baked)
FEATURE [Part::Feature] Line020
  shape: bbox 7.39 x 12.8 x 2e-07 mm, 0 faces, 0 solids (baked)
FEATURE [Part::Feature] Arc300
  shape: bbox 0.06779 x 0.8856 x 2e-07 mm, 0 faces, 0 solids (baked)
FEATURE [Part::Feature] Arc086
  shape: bbox 9 x 6.919 x 2e-07 mm, 0 faces, 0 solids (baked)
FEATURE [Part::Feature] Line019
  shape: bbox 14.78 x 2e-07 x 2e-07 mm, 0 faces, 0 solids (baked)
FEATURE [Part::Feature] Arc009
  shape: bbox 9.698 x 16.8 x 2e-07 mm, 0 faces, 0 solids (baked)
FEATURE [Part::Feature] Line018
  shape: bbox 15.58 x 2e-07 x 2e-07 mm, 0 faces, 0 solids (baked)
FEATURE [Part::Feature] Line017
  shape: bbox 15.58 x 2e-07 x 2e-07 mm, 0 faces, 0 solids (baked)
FEATURE [Part::Feature] Arc008
  shape: bbox 9.698 x 16.8 x 2e-07 mm, 0 faces, 0 solids (baked)
FEATURE [Part::Feature] Line016
  shape: bbox 14.78 x 2e-07 x 2e-07 mm, 0 faces, 0 solids (baked)
FEATURE [Part::Feature] Line023
  shape: bbox 7.39 x 12.8 x 2e-07 mm, 0 faces, 0 solids (baked)
FEATURE [Part::Feature] Arc121
  shape: bbox 2.024 x 0.08867 x 2e-07 mm, 0 faces, 0 solids (baked)
FEATURE [Part::Feature] Line030
  shape: bbox 10.57 x 0.9252 x 2e-07 mm, 0 faces, 0 solids (baked)
FEATURE [Part::Feature] Arc260
  shape: bbox 1.714 x 1.092 x 2e-07 mm, 0 faces, 0 solids (baked)
FEATURE [Part::Feature] Arc250
  shape: bbox 1.324 x 0.1699 x 2e-07 mm, 0 faces, 0 solids (baked)
FEATURE [Part::Feature] Line029
  shape: bbox 8.54 x 2.288 x 2e-07 mm, 0 faces, 0 solids (baked)
FEATURE [Part::Feature] Line028
  shape: bbox 8.186 x 2.193 x 2e-07 mm, 0 faces, 0 solids (baked)
FEATURE [Part::Feature] Arc022
  shape: bbox 1.078 x 3.804 x 2e-07 mm, 0 faces, 0 solids (baked)
FEATURE [Part::Feature] Arc035
  shape: bbox 2 x 2.667 x 2e-07 mm, 0 faces, 0 solids (baked)
FEATURE [Part::Feature] Arc255
  shape: bbox 0.7331 x 0.5015 x 2e-07 mm, 0 faces, 0 solids (baked)
FEATURE [Part::Feature] Arc021
  shape: bbox 3.632 x 1.5 x 2e-07 mm, 0 faces, 0 solids (baked)
FEATURE [Part::Feature] Line027
  shape: bbox 8.396 x 3.915 x 2e-07 mm, 0 faces, 0 solids (baked)
FEATURE [Part::Feature] Arc307
  shape: bbox 0.778 x 1.878 x 2e-07 mm, 0 faces, 0 solids (baked)
FEATURE [Part::Feature] Arc104
  shape: bbox 1.58 x 0.5858 x 2e-07 mm, 0 faces, 0 solids (baked)
FEATURE [Part::Feature] Arc160
  shape: bbox 0.574 x 1.198 x 2e-07 mm, 0 faces, 0 solids (baked)
FEATURE [Part::Feature] Arc020
  shape: bbox 3.252 x 1 x 2e-07 mm, 0 faces, 0 solids (baked)
FEATURE [Part::Feature] Arc124
  shape: bbox 1.461 x 0.8365 x 2e-07 mm, 0 faces, 0 solids (baked)
FEATURE [Sketcher::SketchObject] Sketch167
  sketch-geometry (1):
    g0: LineSegment StartX=-53.3972 StartY=9.11519 StartZ=0 EndX=-47.3085 EndY=0.419642 EndZ=0
FEATURE [Part::Feature] Line026
  shape: bbox 9.096 x 4.242 x 2e-07 mm, 0 faces, 0 solids (baked)
FEATURE [Part::Feature] Arc071
  shape: bbox 8.04 x 13.93 x 2e-07 mm, 0 faces, 0 solids (baked)
FEATURE [Part::Feature] Arc233
  shape: bbox 1.087 x 1.556 x 2e-07 mm, 0 faces, 0 solids (baked)
FEATURE [Part::Feature] Line025
  shape: bbox 9.821 x 6.877 x 2e-07 mm, 0 faces, 0 solids (baked)
FEATURE [Sketcher::SketchObject] Sketch099
  sketch-geometry (1):
    g0: ArcOfCircle CenterX=0 CenterY=0 CenterZ=0 NormalX=0 NormalY=0 NormalZ=1 Radius=45.5 StartAngle=0.981156 EndAngle=1.02584
FEATURE [Sketcher::SketchObject] Sketch278
  sketch-geometry (1):
    g0: ArcOfCircle CenterX=32.8672 CenterY=34.2928 CenterZ=0 NormalX=0 NormalY=0 NormalZ=1 Radius=2 StartAngle=3.94822 EndAngle=4.62512
FEATURE [Sketcher::SketchObject] Sketch063
  sketch-geometry (1):
    g0: ArcOfCircle CenterX=0 CenterY=22 CenterZ=0 NormalX=0 NormalY=0 NormalZ=1 Radius=4.5 StartAngle=1.52693 EndAngle=1.61467
FEATURE [Part::Feature] Arc211
  shape: bbox 1.089 x 1.709 x 2e-07 mm, 0 faces, 0 solids (baked)
FEATURE [Part::Feature] Arc212
  shape: bbox 1.373 x 1.499 x 2e-07 mm, 0 faces, 0 solids (baked)
FEATURE [Part::Feature] Arc050
  shape: bbox 0.3135 x 2.075 x 2e-07 mm, 0 faces, 0 solids (baked)
FEATURE [Part::Feature] Arc073
  shape: bbox 16.08 x 0.7408 x 2e-07 mm, 0 faces, 0 solids (baked)
FEATURE [Sketcher::SketchObject] Sketch348
  sketch-geometry (1):
    g0: ArcOfCircle CenterX=-26.2612 CenterY=31.4857 CenterZ=0 NormalX=0 NormalY=0 NormalZ=1 Radius=3 StartAngle=2.26597 EndAngle=3.66519
FEATURE [Sketcher::SketchObject] Sketch381
  sketch-geometry (1):
    g0: ArcOfCircle CenterX=-32.8672 CenterY=-34.2928 CenterZ=0 NormalX=0 NormalY=0 NormalZ=1 Radius=2 StartAngle=0.806623 EndAngle=1.48353
FEATURE [Sketcher::SketchObject] Sketch044
  sketch-geometry (1):
    g0: LineSegment StartX=3.72902 StartY=-45.8065 StartZ=0 EndX=-6.92065 EndY=-56.4562 EndZ=0
FEATURE [Part::Feature] Arc048
  shape: bbox 1.82 x 1 x 2e-07 mm, 0 faces, 0 solids (baked)
FEATURE [Sketcher::SketchObject] Sketch098
  sketch-geometry (1):
    g0: ArcOfCircle CenterX=-44.0254 CenterY=-14.967 CenterZ=0 NormalX=0 NormalY=0 NormalZ=1 Radius=1 StartAngle=4.10152 EndAngle=6.61089
FEATURE [Sketcher::SketchObject] Sketch039
  sketch-geometry (1):
    g0: ArcOfCircle CenterX=0 CenterY=0 CenterZ=0 NormalX=0 NormalY=0 NormalZ=1 Radius=44 StartAngle=2.43423 EndAngle=2.80176
FEATURE [Sketcher::SketchObject] Sketch062
  sketch-geometry (1):
    g0: LineSegment StartX=-19.1709 StartY=41.7686 StartZ=0 EndX=-14.5114 EndY=51.7609 EndZ=0
FEATURE [Sketcher::SketchObject] Sketch302
  sketch-geometry (1):
    g0: LineSegment StartX=53.1261 StartY=-22.8017 StartZ=0 EndX=46.517 EndY=-8.62831 EndZ=0
FEATURE [Sketcher::SketchObject] Sketch408
  sketch-geometry (1):
    g0: ArcOfCircle CenterX=-13.2649 CenterY=45.6102 CenterZ=0 NormalX=0 NormalY=0 NormalZ=1 Radius=2 StartAngle=4.99541 EndAngle=5.67232
FEATURE [Sketcher::SketchObject] Sketch414
  sketch-geometry (1):
    g0: ArcOfCircle CenterX=39.9023 CenterY=-37.155 CenterZ=0 NormalX=0 NormalY=0 NormalZ=1 Radius=2 StartAngle=5.15739 EndAngle=6.37045
FEATURE [Sketcher::SketchObject] Sketch061
  sketch-geometry (1):
    g0: ArcOfCircle CenterX=-34.7669 CenterY=-39.6934 CenterZ=0 NormalX=0 NormalY=0 NormalZ=1 Radius=2 StartAngle=4.23924 EndAngle=4.79966
FEATURE [Sketcher::SketchObject] Sketch300
  sketch-geometry (1):
    g0: LineSegment StartX=32.3005 StartY=-32.6929 StartZ=0 EndX=31.493 EndY=-41.922 EndZ=0
FEATURE [Part::Feature] Arc346
  shape: bbox 1.089 x 1.709 x 2e-07 mm, 0 faces, 0 solids (baked)
FEATURE [Part::Feature] Arc261
  shape: bbox 1.499 x 1.373 x 2e-07 mm, 0 faces, 0 solids (baked)
FEATURE [Part::Feature] Arc049
  shape: bbox 1.82 x 1 x 2e-07 mm, 0 faces, 0 solids (baked)
FEATURE [Part::Feature] Arc267
  shape: bbox 0.9786 x 1.819 x 2e-07 mm, 0 faces, 0 solids (baked)
FEATURE [Sketcher::SketchObject] Sketch275
  sketch-geometry (1):
    g0: LineSegment StartX=-32.3005 StartY=32.6929 StartZ=0 EndX=-31.493 EndY=41.922 EndZ=0
FEATURE [Sketcher::SketchObject] Sketch286
  sketch-geometry (1):
    g0: ArcOfCircle CenterX=127.5 CenterY=-220.836 CenterZ=0 NormalX=0 NormalY=0 NormalZ=1 Radius=201.5 StartAngle=2.14485 EndAngle=2.15735
FEATURE [Sketcher::SketchObject] Sketch060
  sketch-geometry (1):
    g0: ArcOfCircle CenterX=127.5 CenterY=-220.836 CenterZ=0 NormalX=0 NormalY=0 NormalZ=1 Radius=200 StartAngle=1.98816 EndAngle=2.20063
FEATURE [Sketcher::SketchObject] Sketch129
  sketch-geometry (1):
    g0: LineSegment StartX=-28.8593 StartY=-29.9857 StartZ=0 EndX=-21.0697 EndY=-16.4937 EndZ=0
FEATURE [Sketcher::SketchObject] Sketch109
  sketch-geometry (1):
    g0: ArcOfCircle CenterX=0 CenterY=0 CenterZ=0 NormalX=0 NormalY=0 NormalZ=1 Radius=45.5 StartAngle=4.99541 EndAngle=5.04009
FEATURE [Sketcher::SketchObject] Sketch179
  sketch-geometry (1):
    g0: ArcOfCircle CenterX=0 CenterY=0 CenterZ=0 NormalX=0 NormalY=0 NormalZ=1 Radius=60 StartAngle=3.50284 EndAngle=3.82755
FEATURE [Sketcher::SketchObject] Sketch413
  sketch-geometry (1):
    g0: ArcOfCircle CenterX=127.5 CenterY=220.836 CenterZ=0 NormalX=0 NormalY=0 NormalZ=1 Radius=201.5 StartAngle=4.14754 EndAngle=4.15356
FEATURE [Sketcher::SketchObject] Sketch234
  sketch-geometry (1):
    g0: ArcOfCircle CenterX=0 CenterY=22 CenterZ=0 NormalX=0 NormalY=0 NormalZ=1 Radius=4.5 StartAngle=2.57412 EndAngle=6.85065
FEATURE [Sketcher::SketchObject] Sketch005
  sketch-geometry (1):
    g0: ArcOfCircle CenterX=29.122 CenterY=-36.2514 CenterZ=0 NormalX=0 NormalY=0 NormalZ=1 Radius=1 StartAngle=6.02139 EndAngle=8.53075
FEATURE [Sketcher::SketchObject] Sketch042
  sketch-geometry (1):
    g0: ArcOfCircle CenterX=-51.3135 CenterY=23.6469 CenterZ=0 NormalX=0 NormalY=0 NormalZ=1 Radius=2 StartAngle=2.70977 EndAngle=3.57792
FEATURE [Sketcher::SketchObject] Sketch032
  sketch-geometry (1):
    g0: ArcOfCircle CenterX=36.2514 CenterY=29.122 CenterZ=0 NormalX=0 NormalY=0 NormalZ=1 Radius=1 StartAngle=1.309 EndAngle=3.81836
FEATURE [Sketcher::SketchObject] Sketch097
  sketch-geometry (1):
    g0: ArcOfCircle CenterX=-20.9835 CenterY=42.6139 CenterZ=0 NormalX=0 NormalY=0 NormalZ=1 Radius=2 StartAngle=5.16995 EndAngle=5.84685
FEATURE [Sketcher::SketchObject] Sketch059
  sketch-geometry (1):
    g0: LineSegment StartX=41.5341 StartY=-19.6738 StartZ=0 EndX=45.4322 EndY=-34.2216 EndZ=0
FEATURE [Part::Feature] Arc217
  shape: bbox 2.015 x 0.2652 x 2e-07 mm, 0 faces, 0 solids (baked)
FEATURE [Sketcher::SketchObject] Sketch382
  sketch-geometry (1):
    g0: ArcOfCircle CenterX=0 CenterY=0 CenterZ=0 NormalX=0 NormalY=0 NormalZ=1 Radius=45.5 StartAngle=6.04261 EndAngle=6.08729
FEATURE [Sketcher::SketchObject] Sketch403
  sketch-geometry (1):
    g0: ArcOfCircle CenterX=-24.9053 CenterY=46.2496 CenterZ=0 NormalX=0 NormalY=0 NormalZ=1 Radius=1 StartAngle=6.02139 EndAngle=8.38527
FEATURE [Sketcher::SketchObject] Sketch034
  sketch-geometry (1):
    g0: ArcOfCircle CenterX=6.21354 CenterY=57.1633 CenterZ=0 NormalX=0 NormalY=0 NormalZ=1 Radius=1 StartAngle=5.49779 EndAngle=7.74571
FEATURE [Sketcher::SketchObject] Sketch218
  sketch-geometry (1):
    g0: ArcOfCircle CenterX=-255 CenterY=0 CenterZ=0 NormalX=0 NormalY=0 NormalZ=1 Radius=201.5 StartAngle=0.0504506 EndAngle=0.0629534
FEATURE [Sketcher::SketchObject] Sketch270
  sketch-geometry (1):
    g0: LineSegment StartX=-26.5873 StartY=-37.4868 StartZ=0 EndX=-37.5706 EndY=-38.4477 EndZ=0
FEATURE [Sketcher::SketchObject] Sketch373
  sketch-geometry (1):
    g0: ArcOfCircle CenterX=-34.2928 CenterY=32.8672 CenterZ=0 NormalX=0 NormalY=0 NormalZ=1 Radius=2 StartAngle=5.51901 EndAngle=6.19592
FEATURE [Sketcher::SketchObject] Sketch069
  sketch-geometry (1):
    g0: LineSegment StartX=41.5341 StartY=-19.6738 StartZ=0 EndX=45.4322 EndY=-34.2216 EndZ=0
FEATURE [Sketcher::SketchObject] Sketch227
  sketch-geometry (1):
    g0: ArcOfCircle CenterX=-16.992 CenterY=49.9557 CenterZ=0 NormalX=0 NormalY=0 NormalZ=1 Radius=2 StartAngle=2.14485 EndAngle=2.70526
FEATURE [Sketcher::SketchObject] Sketch274
  sketch-geometry (1):
    g0: ArcOfCircle CenterX=51.0983 CenterY=24.1085 CenterZ=0 NormalX=0 NormalY=0 NormalZ=1 Radius=2 StartAngle=0.440839 EndAngle=1.309
FEATURE [Part::Feature] Circle002
  shape: bbox 5.5 x 5.5 x 2e-07 mm, 0 faces, 0 solids (baked)
FEATURE [Sketcher::SketchObject] Sketch240
  sketch-geometry (1):
    g0: ArcOfCircle CenterX=-51.0983 CenterY=-24.1085 CenterZ=0 NormalX=0 NormalY=0 NormalZ=1 Radius=2 StartAngle=3.58243 EndAngle=4.45059
FEATURE [Sketcher::SketchObject] Sketch190
  sketch-geometry (1):
    g0: LineSegment StartX=19.6738 StartY=41.5341 StartZ=0 EndX=27.8595 EndY=43.7275 EndZ=0
FEATURE [Part::Feature] Arc127
  shape: bbox 1.237 x 1.613 x 2e-07 mm, 0 faces, 0 solids (baked)
FEATURE [Sketcher::SketchObject] Sketch242
  sketch-geometry (1):
    g0: ArcOfCircle CenterX=0 CenterY=0 CenterZ=0 NormalX=0 NormalY=0 NormalZ=1 Radius=45.5 StartAngle=0.63209 EndAngle=0.676771
FEATURE [Sketcher::SketchObject] Sketch248
  sketch-geometry (1):
    g0: ArcOfCircle CenterX=0 CenterY=0 CenterZ=0 NormalX=0 NormalY=0 NormalZ=1 Radius=44 StartAngle=5.06442 EndAngle=5.40756
FEATURE [Sketcher::SketchObject] Sketch337
  sketch-geometry (1):
    g0: LineSegment StartX=-3.25637 StartY=-57.7208 StartZ=0 EndX=7.80178 EndY=-46.6627 EndZ=0
FEATURE [Sketcher::SketchObject] Sketch237
  sketch-geometry (1):
    g0: LineSegment StartX=-11.0788 StartY=-54.7722 StartZ=0 EndX=-0.419642 EndY=-47.3085 EndZ=0
FEATURE [Sketcher::SketchObject] Sketch305
  sketch-geometry (1):
    g0: LineSegment StartX=45.7581 StartY=-4.28185 StartZ=0 EndX=52.082 EndY=-13.3132 EndZ=0
FEATURE [Sketcher::SketchObject] Sketch362
  sketch-geometry (1):
    g0: LineSegment StartX=37.4868 StartY=-26.5873 StartZ=0 EndX=38.5317 EndY=-38.5308 EndZ=0
FEATURE [Sketcher::SketchObject] Sketch139
  sketch-geometry (1):
    g0: ArcOfCircle CenterX=-7.67463 CenterY=41.2929 CenterZ=0 NormalX=0 NormalY=0 NormalZ=1 Radius=2 StartAngle=1.75456 EndAngle=3.66519
FEATURE [Sketcher::SketchObject] Sketch118
  sketch-geometry (1):
    g0: ArcOfCircle CenterX=20.9835 CenterY=-42.6139 CenterZ=0 NormalX=0 NormalY=0 NormalZ=1 Radius=2 StartAngle=2.02835 EndAngle=2.70526
FEATURE [Sketcher::SketchObject] Sketch138
  sketch-geometry (1):
    g0: ArcOfCircle CenterX=51.7589 CenterY=-10.2623 CenterZ=0 NormalX=0 NormalY=0 NormalZ=1 Radius=2 StartAngle=0.0504506 EndAngle=0.610865
FEATURE [Sketcher::SketchObject] Sketch009
  sketch-geometry (1):
    g0: ArcOfCircle CenterX=-3.1347 CenterY=-47.3965 CenterZ=0 NormalX=0 NormalY=0 NormalZ=1 Radius=2 StartAngle=1.50475 EndAngle=2.18166
FEATURE [Sketcher::SketchObject] Sketch137
  sketch-geometry (1):
    g0: LineSegment StartX=-2.01711 StartY=-27.4937 StartZ=0 EndX=-9.40668 EndY=-40.2929 EndZ=0
FEATURE [Part::Feature] Arc151
  shape: bbox 1.155 x 1.97 x 2e-07 mm, 0 faces, 0 solids (baked)
FEATURE [Sketcher::SketchObject] Sketch096
  sketch-geometry (1):
    g0: ArcOfCircle CenterX=-52.9011 CenterY=12.7396 CenterZ=0 NormalX=0 NormalY=0 NormalZ=1 Radius=1 StartAngle=0.610865 EndAngle=3.20455
FEATURE [Sketcher::SketchObject] Sketch058
  sketch-geometry (1):
    g0: LineSegment StartX=-46.3099 StartY=-34.6077 StartZ=0 EndX=-30.7308 EndY=-35.9707 EndZ=0
FEATURE [Sketcher::SketchObject] Sketch095
  sketch-geometry (1):
    g0: ArcOfCircle CenterX=19.0526 CenterY=-11 CenterZ=0 NormalX=0 NormalY=0 NormalZ=1 Radius=4.5 StartAngle=5.71572 EndAngle=5.80346
FEATURE [Sketcher::SketchObject] Sketch245
  sketch-geometry (1):
    g0: LineSegment StartX=26.5873 StartY=37.4868 StartZ=0 EndX=37.5706 EndY=38.4477 EndZ=0
FEATURE [Sketcher::SketchObject] Sketch094
  sketch-geometry (1):
    g0: ArcOfCircle CenterX=-12.226 CenterY=-53.1339 CenterZ=0 NormalX=0 NormalY=0 NormalZ=1 Radius=2 StartAngle=4.11019 EndAngle=5.32325
FEATURE [Part::Feature] Arc310
  shape: bbox 0.1428 x 2.515 x 2e-07 mm, 0 faces, 0 solids (baked)
FEATURE [Sketcher::SketchObject] Sketch219
  sketch-geometry (1):
    g0: ArcOfCircle CenterX=0 CenterY=0 CenterZ=0 NormalX=0 NormalY=0 NormalZ=1 Radius=45.5 StartAngle=4.47181 EndAngle=4.51649
FEATURE [Sketcher::SketchObject] Sketch093
  sketch-geometry (1):
    g0: ArcOfCircle CenterX=12.226 CenterY=53.1339 CenterZ=0 NormalX=0 NormalY=0 NormalZ=1 Radius=2 StartAngle=0.968596 EndAngle=2.18166
FEATURE [Sketcher::SketchObject] Sketch110
  sketch-geometry (1):
    g0: LineSegment StartX=48.3595 StartY=-31.6805 StartZ=0 EndX=44.312 EndY=-16.5748 EndZ=0
FEATURE [Part::Feature] Arc257
  shape: bbox 1.985 x 0.4401 x 2e-07 mm, 0 faces, 0 solids (baked)
FEATURE [Sketcher::SketchObject] Sketch298
  sketch-geometry (1):
    g0: LineSegment StartX=-18.8046 StartY=50.801 StartZ=0 EndX=-23.2909 EndY=41.1802 EndZ=0
FEATURE [Part::Feature] Arc293
  shape: bbox 0.1874 x 1.322 x 2e-07 mm, 0 faces, 0 solids (baked)
FEATURE [Sketcher::SketchObject] Sketch162
  sketch-geometry (1):
    g0: ArcOfCircle CenterX=-19.3376 CenterY=-17.4937 CenterZ=0 NormalX=0 NormalY=0 NormalZ=1 Radius=2 StartAngle=1.52693 EndAngle=2.61799
FEATURE [Sketcher::SketchObject] Sketch222
  sketch-geometry (1):
    g0: ArcOfCircle CenterX=-5.17792 CenterY=56.2622 CenterZ=0 NormalX=0 NormalY=0 NormalZ=1 Radius=2 StartAngle=1.66257 EndAngle=2.53073
FEATURE [Part::Feature] Arc114
  shape: bbox 1.286 x 0.3377 x 2e-07 mm, 0 faces, 0 solids (baked)
FEATURE [Sketcher::SketchObject] Sketch244
  sketch-geometry (1):
    g0: ArcOfCircle CenterX=-127.5 CenterY=220.836 CenterZ=0 NormalX=0 NormalY=0 NormalZ=1 Radius=201.5 StartAngle=5.19474 EndAngle=5.20076
FEATURE [Part::Feature] Arc335
  shape: bbox 1.455 x 0.8444 x 2e-07 mm, 0 faces, 0 solids (baked)
FEATURE [Part::Feature] Arc036
  shape: bbox 2 x 2.667 x 2e-07 mm, 0 faces, 0 solids (baked)
FEATURE [Part::Feature] Line090
  shape: bbox 3.898 x 14.55 x 2e-07 mm, 0 faces, 0 solids (baked)
FEATURE [Part::Feature] Arc246
  shape: bbox 1.096 x 0.7502 x 2e-07 mm, 0 faces, 0 solids (baked)
FEATURE [Sketcher::SketchObject] Sketch022
  sketch-geometry (1):
    g0: LineSegment StartX=-32.6929 StartY=-32.3005 StartZ=0 EndX=-47.6965 EndY=-30.9878 EndZ=0
FEATURE [Sketcher::SketchObject] Sketch128
  sketch-geometry (1):
    g0: ArcOfCircle CenterX=-7.09467 CenterY=45.9556 CenterZ=0 NormalX=0 NormalY=0 NormalZ=1 Radius=1 StartAngle=2.35619 EndAngle=4.86556
FEATURE [Sketcher::SketchObject] Sketch127
  sketch-geometry (1):
    g0: ArcOfCircle CenterX=0 CenterY=0 CenterZ=0 NormalX=0 NormalY=0 NormalZ=1 Radius=45.5 StartAngle=5.16995 EndAngle=5.21463
FEATURE [Part::Feature] Arc167
  shape: bbox 0.6111 x 1.939 x 2e-07 mm, 0 faces, 0 solids (baked)
FEATURE [Sketcher::SketchObject] Sketch371
  sketch-geometry (1):
    g0: ArcOfCircle CenterX=51.0983 CenterY=24.1085 CenterZ=0 NormalX=0 NormalY=0 NormalZ=1 Radius=2 StartAngle=0.440839 EndAngle=1.309
FEATURE [Sketcher::SketchObject] Sketch304
  sketch-geometry (1):
    g0: ArcOfCircle CenterX=5.48122 CenterY=25.4937 CenterZ=0 NormalX=0 NormalY=0 NormalZ=1 Radius=2 StartAngle=2.61799 EndAngle=3.70906
FEATURE [Sketcher::SketchObject] Sketch028
  sketch-geometry (1):
    g0: ArcOfCircle CenterX=19.1562 CenterY=43.466 CenterZ=0 NormalX=0 NormalY=0 NormalZ=1 Radius=2 StartAngle=4.29728 EndAngle=4.97419
FEATURE [Part::Feature] Arc334
  shape: bbox 0.7265 x 0.8342 x 2e-07 mm, 0 faces, 0 solids (baked)
FEATURE [Sketcher::SketchObject] Sketch092
  sketch-geometry (1):
    g0: LineSegment StartX=-53.1261 StartY=22.8017 StartZ=0 EndX=-46.517 EndY=8.62831 EndZ=0
FEATURE [Sketcher::SketchObject] Sketch115
  sketch-geometry (1):
    g0: ArcOfCircle CenterX=24.8188 CenterY=8 CenterZ=0 NormalX=0 NormalY=0 NormalZ=1 Radius=2 StartAngle=1.5708 EndAngle=2.66186
FEATURE [Sketcher::SketchObject] Sketch281
  sketch-geometry (1):
    g0: ArcOfCircle CenterX=26.2612 CenterY=-31.4857 CenterZ=0 NormalX=0 NormalY=0 NormalZ=1 Radius=3 StartAngle=5.40756 EndAngle=6.80678
FEATURE [Sketcher::SketchObject] Sketch318
  sketch-geometry (1):
    g0: LineSegment StartX=-51.6159 StartY=-26.0403 StartZ=0 EndX=-36.5102 EndY=-30.0879 EndZ=0
FEATURE [Sketcher::SketchObject] Sketch223
  sketch-geometry (1):
    g0: ArcOfCircle CenterX=-39.598 CenterY=14 CenterZ=0 NormalX=0 NormalY=0 NormalZ=1 Radius=2 StartAngle=2.80176 EndAngle=4.71239
FEATURE [Sketcher::SketchObject] Sketch273
  sketch-geometry (1):
    g0: ArcOfCircle CenterX=13.5292 CenterY=53.454 CenterZ=0 NormalX=0 NormalY=0 NormalZ=1 Radius=1 StartAngle=5.32325 EndAngle=7.25619
FEATURE [Sketcher::SketchObject] Sketch257
  sketch-geometry (1):
    g0: ArcOfCircle CenterX=-46.1356 CenterY=-32.6153 CenterZ=0 NormalX=0 NormalY=0 NormalZ=1 Radius=2 StartAngle=3.75696 EndAngle=4.62512
FEATURE [Sketcher::SketchObject] Sketch328
  sketch-geometry (1):
    g0: ArcOfCircle CenterX=-25.6322 CenterY=-44.6683 CenterZ=0 NormalX=0 NormalY=0 NormalZ=1 Radius=2 StartAngle=4.18812 EndAngle=4.97419
FEATURE [Part::Feature] Arc067
  shape: bbox 16.08 x 0.7408 x 2e-07 mm, 0 faces, 0 solids (baked)
FEATURE [Sketcher::SketchObject] Sketch393
  sketch-geometry (1):
    g0: ArcOfCircle CenterX=39.4792 CenterY=-26.413 CenterZ=0 NormalX=0 NormalY=0 NormalZ=1 Radius=2 StartAngle=2.55195 EndAngle=3.22886
FEATURE [Sketcher::SketchObject] Sketch301
  sketch-geometry (1):
    g0: LineSegment StartX=41.7686 StartY=19.1709 StartZ=0 EndX=52.6345 EndY=14.1041 EndZ=0
FEATURE [Part::Feature] Arc064
  shape: bbox 1.774 x 1.077 x 2e-07 mm, 0 faces, 0 solids (baked)
FEATURE [Part::Feature] Arc182
  shape: bbox 1.752 x 1.087 x 2e-07 mm, 0 faces, 0 solids (baked)
FEATURE [Part::Feature] Arc227
  shape: bbox 0.8054 x 1.887 x 2e-07 mm, 0 faces, 0 solids (baked)
FEATURE [Sketcher::SketchObject] Sketch149
  sketch-geometry (1):
    g0: ArcOfCircle CenterX=-0.285064 CenterY=28.4937 CenterZ=0 NormalX=0 NormalY=0 NormalZ=1 Radius=2 StartAngle=3.66519 EndAngle=4.75626
FEATURE [Part::Feature] Arc184
  shape: bbox 1.481 x 1.423 x 2e-07 mm, 0 faces, 0 solids (baked)
FEATURE [Part::Feature] Line024
  shape: bbox 11.06 x 11.06 x 2e-07 mm, 0 faces, 0 solids (baked)
FEATURE [Part::Feature] Arc080
  shape: bbox 9 x 6.919 x 2e-07 mm, 0 faces, 0 solids (baked)
FEATURE [Part::Feature] Arc084
  shape: bbox 8.492 x 9 x 2e-07 mm, 0 faces, 0 solids (baked)
FEATURE [Part::Feature] Line061
  shape: bbox 8.639 x 12.34 x 2e-07 mm, 0 faces, 0 solids (baked)
FEATURE [Sketcher::SketchObject] Sketch252
  sketch-geometry (1):
    g0: ArcOfCircle CenterX=16.8336 CenterY=43.346 CenterZ=0 NormalX=0 NormalY=0 NormalZ=1 Radius=1 StartAngle=1.8326 EndAngle=4.34196
FEATURE [Sketcher::SketchObject] Sketch221
  sketch-geometry (1):
    g0: ArcOfCircle CenterX=26.413 CenterY=39.4792 CenterZ=0 NormalX=0 NormalY=0 NormalZ=1 Radius=2 StartAngle=4.12275 EndAngle=4.79966
FEATURE [Part::Feature] Line079
  shape: bbox 10.66 x 7.464 x 2e-07 mm, 0 faces, 0 solids (baked)
FEATURE [Part::Feature] Arc096
  shape: bbox 1.087 x 1.752 x 2e-07 mm, 0 faces, 0 solids (baked)
FEATURE [Part::Feature] Arc019
  shape: bbox 1.635 x 2.966 x 2e-07 mm, 0 faces, 0 solids (baked)
FEATURE [Part::Feature] Arc247
  shape: bbox 1.291 x 1.078 x 2e-07 mm, 0 faces, 0 solids (baked)
FEATURE [Part::Feature] Arc129
  shape: bbox 1.878 x 0.778 x 2e-07 mm, 0 faces, 0 solids (baked)
FEATURE [Part::Feature] Arc164
  shape: bbox 1.237 x 1.613 x 2e-07 mm, 0 faces, 0 solids (baked)
FEATURE [Part::Feature] Arc042
  shape: bbox 3.632 x 1.5 x 2e-07 mm, 0 faces, 0 solids (baked)
FEATURE [Sketcher::SketchObject] Sketch136
  sketch-geometry (1):
    g0: ArcOfCircle CenterX=51.3135 CenterY=-23.6469 CenterZ=0 NormalX=0 NormalY=0 NormalZ=1 Radius=2 StartAngle=5.85136 EndAngle=6.71952
FEATURE [Part::Feature] Arc348
  shape: bbox 1.073 x 0.5659 x 2e-07 mm, 0 faces, 0 solids (baked)
FEATURE [Sketcher::SketchObject] Sketch120
  sketch-geometry (1):
    g0: ArcOfCircle CenterX=0 CenterY=0 CenterZ=0 NormalX=0 NormalY=0 NormalZ=1 Radius=58.5 StartAngle=0.589859 EndAngle=0.615372
FEATURE [Sketcher::SketchObject] Sketch018
  sketch-geometry (1):
    g0: ArcOfCircle CenterX=-19.0526 CenterY=-11 CenterZ=0 NormalX=0 NormalY=0 NormalZ=1 Radius=4.5 StartAngle=3.62132 EndAngle=3.70906
FEATURE [Part::Feature] Line031
  shape: bbox 10.98 x 0.9609 x 2e-07 mm, 0 faces, 0 solids (baked)
FEATURE [Sketcher::SketchObject] Sketch038
  sketch-geometry (1):
    g0: ArcOfCircle CenterX=127.5 CenterY=-220.836 CenterZ=0 NormalX=0 NormalY=0 NormalZ=1 Radius=201.5 StartAngle=2.09373 EndAngle=2.10208
FEATURE [Sketcher::SketchObject] Sketch171
  sketch-geometry (1):
    g0: ArcOfCircle CenterX=255 CenterY=0 CenterZ=0 NormalX=0 NormalY=0 NormalZ=1 Radius=201.5 StartAngle=3.06299 EndAngle=3.0674
FEATURE [Part::Feature] Line038
  shape: bbox 15.11 x 4.048 x 2e-07 mm, 0 faces, 0 solids (baked)
FEATURE [Part::Feature] Line059
  shape: bbox 4.659 x 9.992 x 2e-07 mm, 0 faces, 0 solids (baked)
FEATURE [Part::Feature] Arc072
  shape: bbox 13.01 x 7.512 x 2e-07 mm, 0 faces, 0 solids (baked)
FEATURE [Part::Feature] Arc078
  shape: bbox 13.01 x 7.512 x 2e-07 mm, 0 faces, 0 solids (baked)
FEATURE [Part::Feature] Arc094
  shape: bbox 0.9128 x 1.851 x 2e-07 mm, 0 faces, 0 solids (baked)
FEATURE [Part::Feature] Arc111
  shape: bbox 1.096 x 0.7502 x 2e-07 mm, 0 faces, 0 solids (baked)
FEATURE [Part::Feature] Arc093
  shape: bbox 0.7412 x 1.898 x 2e-07 mm, 0 faces, 0 solids (baked)
FEATURE [Part::Feature] Arc074
  shape: bbox 13.01 x 7.512 x 2e-07 mm, 0 faces, 0 solids (baked)
FEATURE [Sketcher::SketchObject] Sketch091
  sketch-geometry (1):
    g0: ArcOfCircle CenterX=-40.7576 CenterY=-22.3845 CenterZ=0 NormalX=0 NormalY=0 NormalZ=1 Radius=1 StartAngle=4.27606 EndAngle=6.78542
FEATURE [Part::Feature] Arc110
  shape: bbox 1.459 x 0.8379 x 2e-07 mm, 0 faces, 0 solids (baked)
FEATURE [Part::Feature] Arc033
  shape: bbox 3.632 x 1.5 x 2e-07 mm, 0 faces, 0 solids (baked)
FEATURE [Part::Feature] Line037
  shape: bbox 10.66 x 7.464 x 2e-07 mm, 0 faces, 0 solids (baked)
FEATURE [Sketcher::SketchObject] Sketch168
  sketch-geometry (1):
    g0: LineSegment StartX=-30.1913 StartY=-28.2929 StartZ=0 EndX=-22.8017 EndY=-15.4937 EndZ=0
FEATURE [Part::Feature] Arc245
  shape: bbox 1.459 x 0.8379 x 2e-07 mm, 0 faces, 0 solids (baked)
FEATURE [Sketcher::SketchObject] Sketch057
  sketch-geometry (1):
    g0: LineSegment StartX=-48.3595 StartY=31.6805 StartZ=0 EndX=-44.312 EndY=16.5748 EndZ=0
FEATURE [Part::Feature] Arc023
  shape: bbox 2 x 2.667 x 2e-07 mm, 0 faces, 0 solids (baked)
FEATURE [Part::Feature] Arc030
  shape: bbox 3.632 x 1.5 x 2e-07 mm, 0 faces, 0 solids (baked)
FEATURE [Part::Feature] Arc070
  shape: bbox 0.646 x 15.02 x 2e-07 mm, 0 faces, 0 solids (baked)
FEATURE [Part::Feature] Arc234
  shape: bbox 0.9128 x 1.892 x 2e-07 mm, 0 faces, 0 solids (baked)
FEATURE [Part::Feature] Arc058
  shape: bbox 1.774 x 1.077 x 2e-07 mm, 0 faces, 0 solids (baked)
FEATURE [Sketcher::SketchObject] Sketch225
  sketch-geometry (1):
    g0: ArcOfCircle CenterX=-38.3227 CenterY=-28.0645 CenterZ=0 NormalX=0 NormalY=0 NormalZ=1 Radius=2 StartAngle=0.63209 EndAngle=1.309
FEATURE [Part::Feature] Arc118
  shape: bbox 1.486 x 0.1423 x 2e-07 mm, 0 faces, 0 solids (baked)
FEATURE [Part::Feature] Arc163
  shape: bbox 0.6196 x 1.358 x 2e-07 mm, 0 faces, 0 solids (baked)
FEATURE [Part::Feature] Line065
  shape: bbox 1.134 x 12.96 x 2e-07 mm, 0 faces, 0 solids (baked)
FEATURE [Sketcher::SketchObject] Sketch296
  sketch-geometry (1):
    g0: ArcOfCircle CenterX=127.5 CenterY=220.836 CenterZ=0 NormalX=0 NormalY=0 NormalZ=1 Radius=201.5 StartAngle=4.23924 EndAngle=4.25174
FEATURE [Sketcher::SketchObject] Sketch001
  sketch-geometry (1):
    g0: ArcOfCircle CenterX=3.80715 CenterY=-57.3738 CenterZ=0 NormalX=0 NormalY=0 NormalZ=1 Radius=1 StartAngle=2.53073 EndAngle=4.77865
FEATURE [Part::Feature] Line036
  shape: bbox 10.65 x 10.65 x 2e-07 mm, 0 faces, 0 solids (baked)
FEATURE [Sketcher::SketchObject] Sketch187
  sketch-geometry (1):
    g0: ArcOfCircle CenterX=0 CenterY=0 CenterZ=0 NormalX=0 NormalY=0 NormalZ=1 Radius=45.5 StartAngle=4.12275 EndAngle=4.16743
FEATURE [Sketcher::SketchObject] Sketch174
  sketch-geometry (1):
    g0: LineSegment StartX=-28.8593 StartY=29.9857 StartZ=0 EndX=-21.0697 EndY=16.4937 EndZ=0
FEATURE [Sketcher::SketchObject] Sketch379
  sketch-geometry (1):
    g0: ArcOfCircle CenterX=0 CenterY=0 CenterZ=0 NormalX=0 NormalY=0 NormalZ=1 Radius=45.5 StartAngle=1.85382 EndAngle=1.8985
FEATURE [Part::Feature] Arc091
  shape: bbox 1.153 x 1.707 x 2e-07 mm, 0 faces, 0 solids (baked)
FEATURE [Part::Feature] Arc099
  shape: bbox 0.9128 x 1.892 x 2e-07 mm, 0 faces, 0 solids (baked)
FEATURE [Sketcher::SketchObject] Sketch331
  sketch-geometry (1):
    g0: ArcOfCircle CenterX=-7.67463 CenterY=-41.2929 CenterZ=0 NormalX=0 NormalY=0 NormalZ=1 Radius=2 StartAngle=2.61799 EndAngle=4.52863
FEATURE [Part::Feature] Circle001
  shape: bbox 5.5 x 5.5 x 2e-07 mm, 0 faces, 0 solids (baked)
FEATURE [Part::Feature] Line073
  shape: bbox 10.98 x 0.9609 x 2e-07 mm, 0 faces, 0 solids (baked)
FEATURE [Part::Feature] Line035
  shape: bbox 15.11 x 4.048 x 2e-07 mm, 0 faces, 0 solids (baked)
FEATURE [Part::Feature] Arc063
  shape: bbox 1.774 x 1.077 x 2e-07 mm, 0 faces, 0 solids (baked)
FEATURE [Sketcher::SketchObject] Sketch208
  sketch-geometry (1):
    g0: ArcOfCircle CenterX=0 CenterY=0 CenterZ=0 NormalX=0 NormalY=0 NormalZ=1 Radius=44 StartAngle=4.52863 EndAngle=4.89615
FEATURE [Part::Feature] Arc102
  shape: bbox 0.4372 x 1.646 x 2e-07 mm, 0 faces, 0 solids (baked)
FEATURE [Part::Feature] Arc112
  shape: bbox 1.291 x 1.078 x 2e-07 mm, 0 faces, 0 solids (baked)
FEATURE [Part::Feature] Line097
  shape: bbox 0.8074 x 9.229 x 2e-07 mm, 0 faces, 0 solids (baked)
FEATURE [Sketcher::SketchObject] Sketch170
  sketch-geometry (1):
    g0: ArcOfCircle CenterX=-39.5279 CenterY=38.4436 CenterZ=0 NormalX=0 NormalY=0 NormalZ=1 Radius=1 StartAngle=0.0872665 EndAngle=2.0202
FEATURE [Part::Feature] Line034
  shape: bbox 14.55 x 3.898 x 2e-07 mm, 0 faces, 0 solids (baked)
FEATURE [Sketcher::SketchObject] Sketch196
  sketch-geometry (1):
    g0: ArcOfCircle CenterX=0 CenterY=0 CenterZ=0 NormalX=0 NormalY=0 NormalZ=1 Radius=45.5 StartAngle=2.72649 EndAngle=2.77117
FEATURE [Part::Feature] Arc324
  shape: bbox 1.553 x 1.423 x 2e-07 mm, 0 faces, 0 solids (baked)
FEATURE [Part::Feature] Arc113
  shape: bbox 1.21 x 0.5485 x 2e-07 mm, 0 faces, 0 solids (baked)
FEATURE [Part::Feature] Line051
  shape: bbox 11.79 x 5.499 x 2e-07 mm, 0 faces, 0 solids (baked)
FEATURE [Sketcher::SketchObject] Sketch255
  sketch-geometry (1):
    g0: ArcOfCircle CenterX=-14.1368 CenterY=-38.4857 CenterZ=0 NormalX=0 NormalY=0 NormalZ=1 Radius=3 StartAngle=4.36036 EndAngle=5.75959
FEATURE [Part::Feature] Arc108
  shape: bbox 1.519 x 0.2686 x 2e-07 mm, 0 faces, 0 solids (baked)
FEATURE [Sketcher::SketchObject] Sketch031
  sketch-geometry (1):
    g0: ArcOfCircle CenterX=0 CenterY=0 CenterZ=0 NormalX=0 NormalY=0 NormalZ=1 Radius=45.5 StartAngle=3.07555 EndAngle=3.12023
FEATURE [Sketcher::SketchObject] Sketch313
  sketch-geometry (1):
    g0: ArcOfCircle CenterX=39.5279 CenterY=-38.4436 CenterZ=0 NormalX=0 NormalY=0 NormalZ=1 Radius=1 StartAngle=3.22886 EndAngle=5.16179
FEATURE [Sketcher::SketchObject] Sketch288
  sketch-geometry (1):
    g0: ArcOfCircle CenterX=53.0571 CenterY=15.0104 CenterZ=0 NormalX=0 NormalY=0 NormalZ=1 Radius=1 StartAngle=4.27606 EndAngle=6.20899
FEATURE [Part::Feature] Arc029
  shape: bbox 1.078 x 3.804 x 2e-07 mm, 0 faces, 0 solids (baked)
FEATURE [Sketcher::SketchObject] Sketch003
  sketch-geometry (1):
    g0: ArcOfCircle CenterX=0 CenterY=0 CenterZ=0 NormalX=0 NormalY=0 NormalZ=1 Radius=45.5 StartAngle=6.21714 EndAngle=6.26182
FEATURE [Part::Feature] Arc340
  shape: bbox 0.7502 x 1.096 x 2e-07 mm, 0 faces, 0 solids (baked)
FEATURE [Part::Feature] Arc028
  shape: bbox 1.635 x 2.966 x 2e-07 mm, 0 faces, 0 solids (baked)
FEATURE [Part::Feature] Arc229
  shape: bbox 0.9128 x 1.851 x 2e-07 mm, 0 faces, 0 solids (baked)
FEATURE [Part::Feature] Arc027
  shape: bbox 3.252 x 1 x 2e-07 mm, 0 faces, 0 solids (baked)
FEATURE [Part::Feature] Arc220
  shape: bbox 2.107 x 1.381 x 2e-07 mm, 0 faces, 0 solids (baked)
FEATURE [Part::Feature] Arc026
  shape: bbox 2.956 x 2.488 x 2e-07 mm, 0 faces, 0 solids (baked)
FEATURE [Part::Feature] Arc147
  shape: bbox 1.42 x 0.9259 x 2e-07 mm, 0 faces, 0 solids (baked)
FEATURE [Sketcher::SketchObject] Sketch030
  sketch-geometry (1):
    g0: ArcOfCircle CenterX=-43.346 CenterY=16.8336 CenterZ=0 NormalX=0 NormalY=0 NormalZ=1 Radius=1 StartAngle=3.40339 EndAngle=5.91276
FEATURE [Sketcher::SketchObject] Sketch153
  sketch-geometry (1):
    g0: ArcOfCircle CenterX=24.5338 CenterY=14.4937 CenterZ=0 NormalX=0 NormalY=0 NormalZ=1 Radius=2 StartAngle=2.61799 EndAngle=3.70906
FEATURE [Sketcher::SketchObject] Sketch090
  sketch-geometry (1):
    g0: LineSegment StartX=-41.7686 StartY=-19.1709 StartZ=0 EndX=-52.6345 EndY=-14.1041 EndZ=0
FEATURE [Sketcher::SketchObject] Sketch165
  sketch-geometry (1):
    g0: ArcOfCircle CenterX=255 CenterY=0 CenterZ=0 NormalX=0 NormalY=0 NormalZ=1 Radius=200 StartAngle=3.03536 EndAngle=3.24782
FEATURE [Sketcher::SketchObject] Sketch309
  sketch-geometry (1):
    g0: ArcOfCircle CenterX=0 CenterY=0 CenterZ=0 NormalX=0 NormalY=0 NormalZ=1 Radius=58.5 StartAngle=0.415326 EndAngle=0.440839
FEATURE [Sketcher::SketchObject] Sketch089
  sketch-geometry (1):
    g0: ArcOfCircle CenterX=-5.48122 CenterY=25.4937 CenterZ=0 NormalX=0 NormalY=0 NormalZ=1 Radius=2 StartAngle=5.71572 EndAngle=6.80678
FEATURE [Sketcher::SketchObject] Sketch066
  sketch-geometry (1):
    g0: ArcOfCircle CenterX=6.21354 CenterY=57.1633 CenterZ=0 NormalX=0 NormalY=0 NormalZ=1 Radius=1 StartAngle=5.49779 EndAngle=7.74571
FEATURE [Sketcher::SketchObject] Sketch398
  sketch-geometry (1):
    g0: ArcOfCircle CenterX=46.3981 CenterY=-33.9627 CenterZ=0 NormalX=0 NormalY=0 NormalZ=1 Radius=1 StartAngle=3.40339 EndAngle=5.65131
FEATURE [Part::Feature] Arc075
  shape: bbox 8.04 x 13.93 x 2e-07 mm, 0 faces, 0 solids (baked)
FEATURE [Sketcher::SketchObject] Sketch216
  sketch-geometry (1):
    g0: ArcOfCircle CenterX=0 CenterY=0 CenterZ=0 NormalX=0 NormalY=0 NormalZ=1 Radius=45.5 StartAngle=0.63209 EndAngle=0.676771
FEATURE [Sketcher::SketchObject] Sketch105
  sketch-geometry (1):
    g0: ArcOfCircle CenterX=0 CenterY=0 CenterZ=0 NormalX=0 NormalY=0 NormalZ=1 Radius=45.5 StartAngle=2.02835 EndAngle=2.07303
FEATURE [Part::Feature] Arc116
  shape: bbox 1.322 x 0.1874 x 2e-07 mm, 0 faces, 0 solids (baked)
FEATURE [Part::Feature] Arc301
  shape: bbox 0.9353 x 1.797 x 2e-07 mm, 0 faces, 0 solids (baked)
FEATURE [Sketcher::SketchObject] Sketch088
  sketch-geometry (1):
    g0: ArcOfCircle CenterX=14.967 CenterY=-44.0254 CenterZ=0 NormalX=0 NormalY=0 NormalZ=1 Radius=1 StartAngle=5.67232 EndAngle=8.18169
FEATURE [Part::Feature] Line033
  shape: bbox 15 x 1.313 x 2e-07 mm, 0 faces, 0 solids (baked)
FEATURE [Part::Feature] Arc150
  shape: bbox 1.096 x 0.7502 x 2e-07 mm, 0 faces, 0 solids (baked)
FEATURE [Part::Feature] Arc311
  shape: bbox 0.6419 x 1.347 x 2e-07 mm, 0 faces, 0 solids (baked)
FEATURE [Part::Feature] Line032
  shape: bbox 15.58 x 1.363 x 2e-07 mm, 0 faces, 0 solids (baked)
FEATURE [Part::Feature] Arc130
  shape: bbox 2.25 x 1.134 x 2e-07 mm, 0 faces, 0 solids (baked)
FEATURE [Part::Feature] Arc034
  shape: bbox 1.078 x 3.804 x 2e-07 mm, 0 faces, 0 solids (baked)
FEATURE [Sketcher::SketchObject] Sketch087
  sketch-geometry (1):
    g0: LineSegment StartX=-51.6159 StartY=-26.0403 StartZ=0 EndX=-36.5102 EndY=-30.0879 EndZ=0
FEATURE [Part::Feature] Line100
  shape: bbox 4.486 x 9.621 x 2e-07 mm, 0 faces, 0 solids (baked)
FEATURE [Part::Feature] Arc032
  shape: bbox 3.252 x 1 x 2e-07 mm, 0 faces, 0 solids (baked)
FEATURE [Part::Feature] Line055
  shape: bbox 0.8074 x 9.229 x 2e-07 mm, 0 faces, 0 solids (baked)
FEATURE [Part::Feature] Line039
  shape: bbox 10.87 x 5.067 x 2e-07 mm, 0 faces, 0 solids (baked)
FEATURE [Part::Feature] Line046
  shape: bbox 6.609 x 14.17 x 2e-07 mm, 0 faces, 0 solids (baked)
FEATURE [Part::Feature] Line089
  shape: bbox 6.365 x 13.65 x 2e-07 mm, 0 faces, 0 solids (baked)
FEATURE [Sketcher::SketchObject] Sketch056
  sketch-geometry (1):
    g0: LineSegment StartX=37.8051 StartY=26.1327 StartZ=0 EndX=52.3528 EndY=22.2346 EndZ=0
FEATURE [Sketcher::SketchObject] Sketch086
  sketch-geometry (1):
    g0: LineSegment StartX=3.74917 StartY=26.4937 StartZ=0 EndX=11.5388 EndY=39.9857 EndZ=0
FEATURE [Sketcher::SketchObject] Sketch333
  sketch-geometry (1):
    g0: ArcOfCircle CenterX=13.2649 CenterY=-45.6102 CenterZ=0 NormalX=0 NormalY=0 NormalZ=1 Radius=2 StartAngle=1.85382 EndAngle=2.53073
FEATURE [Part::Feature] Arc044
  shape: bbox 0.3135 x 2.075 x 2e-07 mm, 0 faces, 0 solids (baked)
FEATURE [Part::Feature] Line045
  shape: bbox 6.324 x 9.031 x 2e-07 mm, 0 faces, 0 solids (baked)
FEATURE [Part::Feature] Line098
  shape: bbox 2.193 x 8.186 x 2e-07 mm, 0 faces, 0 solids (baked)
FEATURE [Sketcher::SketchObject] Sketch401
  sketch-geometry (1):
    g0: ArcOfCircle CenterX=-127.5 CenterY=-220.836 CenterZ=0 NormalX=0 NormalY=0 NormalZ=1 Radius=201.5 StartAngle=1.00595 EndAngle=1.01197
FEATURE [Part::Feature] Arc139
  shape: bbox 1.819 x 0.9786 x 2e-07 mm, 0 faces, 0 solids (baked)
FEATURE [Part::Feature] Arc156
  shape: bbox 0.1699 x 1.324 x 2e-07 mm, 0 faces, 0 solids (baked)
FEATURE [Sketcher::SketchObject] Sketch258
  sketch-geometry (1):
    g0: ArcOfCircle CenterX=39.598 CenterY=14 CenterZ=0 NormalX=0 NormalY=0 NormalZ=1 Radius=2 StartAngle=4.71239 EndAngle=6.62302
FEATURE [Part::Feature] Arc128
  shape: bbox 0.6196 x 1.358 x 2e-07 mm, 0 faces, 0 solids (baked)
FEATURE [Part::Feature] Line044
  shape: bbox 6.089 x 8.696 x 2e-07 mm, 0 faces, 0 solids (baked)
FEATURE [Part::Feature] Line060
  shape: bbox 8.97 x 12.81 x 2e-07 mm, 0 faces, 0 solids (baked)
FEATURE [Part::Feature] Arc025
  shape: bbox 2.956 x 2.488 x 2e-07 mm, 0 faces, 0 solids (baked)
FEATURE [Part::Feature] Arc192
  shape: bbox 1.431 x 0.9128 x 2e-07 mm, 0 faces, 0 solids (baked)
FEATURE [Sketcher::SketchObject] Sketch212
  sketch-geometry (1):
    g0: ArcOfCircle CenterX=-0.285064 CenterY=-28.4937 CenterZ=0 NormalX=0 NormalY=0 NormalZ=1 Radius=2 StartAngle=1.52693 EndAngle=2.61799
FEATURE [Part::Feature] Line099
  shape: bbox 2.288 x 8.54 x 2e-07 mm, 0 faces, 0 solids (baked)
FEATURE [Part::Feature] Arc265
  shape: bbox 2.25 x 1.134 x 2e-07 mm, 0 faces, 0 solids (baked)
FEATURE [Part::Feature] Line070
  shape: bbox 8.186 x 2.193 x 2e-07 mm, 0 faces, 0 solids (baked)
FEATURE [Part::Feature] Arc052
  shape: bbox 1.774 x 1.077 x 2e-07 mm, 0 faces, 0 solids (baked)
FEATURE [Part::Feature] Line077
  shape: bbox 15.11 x 4.048 x 2e-07 mm, 0 faces, 0 solids (baked)
FEATURE [Sketcher::SketchObject] Sketch376
  sketch-geometry (1):
    g0: ArcOfCircle CenterX=-36.2514 CenterY=-29.122 CenterZ=0 NormalX=0 NormalY=0 NormalZ=1 Radius=1 StartAngle=4.45059 EndAngle=6.95996
FEATURE [Sketcher::SketchObject] Sketch324
  sketch-geometry (1):
    g0: ArcOfCircle CenterX=-19.0526 CenterY=11 CenterZ=0 NormalX=0 NormalY=0 NormalZ=1 Radius=4.5 StartAngle=2.57412 EndAngle=2.66186
FEATURE [Part::Feature] Arc292
  shape: bbox 0.3565 x 1.657 x 2e-07 mm, 0 faces, 0 solids (baked)
FEATURE [Sketcher::SketchObject] Sketch299
  sketch-geometry (1):
    g0: ArcOfCircle CenterX=-31.9233 CenterY=-27.2929 CenterZ=0 NormalX=0 NormalY=0 NormalZ=1 Radius=2 StartAngle=3.84895 EndAngle=5.75959
FEATURE [Sketcher::SketchObject] Sketch114
  sketch-geometry (1):
    g0: ArcOfCircle CenterX=-127.5 CenterY=220.836 CenterZ=0 NormalX=0 NormalY=0 NormalZ=1 Radius=201.5 StartAngle=5.23532 EndAngle=5.24367
FEATURE [Part::Feature] Line058
  shape: bbox 4.486 x 9.621 x 2e-07 mm, 0 faces, 0 solids (baked)
FEATURE [Part::Feature] Line066
  shape: bbox 11.06 x 11.06 x 2e-07 mm, 0 faces, 0 solids (baked)
FEATURE [Sketcher::SketchObject] Sketch386
  sketch-geometry (1):
    g0: Circle CenterX=-19.0526 CenterY=-11 CenterZ=0 NormalX=0 NormalY=0 NormalZ=1 Radius=2.75
FEATURE [Part::Feature] Arc159
  shape: bbox 0.3617 x 1.279 x 2e-07 mm, 0 faces, 0 solids (baked)
FEATURE [Sketcher::SketchObject] Sketch111
  sketch-geometry (1):
    g0: ArcOfCircle CenterX=18.5695 CenterY=48.9458 CenterZ=0 NormalX=0 NormalY=0 NormalZ=1 Radius=2 StartAngle=1.00595 EndAngle=2.00713
FEATURE [Part::Feature] Line043
  shape: bbox 6.252 x 6.252 x 2e-07 mm, 0 faces, 0 solids (baked)
FEATURE [Part::Feature] Arc089
  shape: bbox 0.1974 x 0.3418 x 2e-07 mm, 0 faces, 0 solids (baked)
FEATURE [Sketcher::SketchObject] Sketch387
  sketch-geometry (1):
    g0: ArcOfCircle CenterX=52.6116 CenterY=23.2006 CenterZ=0 NormalX=0 NormalY=0 NormalZ=1 Radius=1 StartAngle=4.45059 EndAngle=6.69851
FEATURE [Part::Feature] Line069
  shape: bbox 8.396 x 3.915 x 2e-07 mm, 0 faces, 0 solids (baked)
FEATURE [Sketcher::SketchObject] Sketch342
  sketch-geometry (1):
    g0: LineSegment StartX=-37.8051 StartY=-26.1327 StartZ=0 EndX=-52.3528 EndY=-22.2346 EndZ=0
FEATURE [Part::Feature] Arc304
  shape: bbox 0.005951 x 1.683 x 2e-07 mm, 0 faces, 0 solids (baked)
FEATURE [Part::Feature] Arc024
  shape: bbox 2 x 2.667 x 2e-07 mm, 0 faces, 0 solids (baked)
FEATURE [Part::Feature] Arc243
  shape: bbox 1.519 x 0.2686 x 2e-07 mm, 0 faces, 0 solids (baked)
FEATURE [Sketcher::SketchObject] Sketch107
  sketch-geometry (1):
    g0: ArcOfCircle CenterX=24.5338 CenterY=-14.4937 CenterZ=0 NormalX=0 NormalY=0 NormalZ=1 Radius=2 StartAngle=2.57412 EndAngle=3.66519
FEATURE [Sketcher::SketchObject] Sketch178
  sketch-geometry (1):
    g0: LineSegment StartX=-39.598 StartY=12 StartZ=0 EndX=-24.8188 EndY=12 EndZ=0
FEATURE [Part::Feature] Circle005
  shape: bbox 5.5 x 5.5 x 2e-07 mm, 0 faces, 0 solids (baked)
FEATURE [Part::Feature] Line042
  shape: bbox 5.992 x 5.992 x 2e-07 mm, 0 faces, 0 solids (baked)
FEATURE [Part::Feature] Arc031
  shape: bbox 1.635 x 2.966 x 2e-07 mm, 0 faces, 0 solids (baked)
FEATURE [Part::Feature] Line084
  shape: bbox 5.992 x 5.992 x 2e-07 mm, 0 faces, 0 solids (baked)
FEATURE [Part::Feature] Arc203
  shape: bbox 1.08 x 0.7733 x 2e-07 mm, 0 faces, 0 solids (baked)
FEATURE [Part::Feature] Line041
  shape: bbox 7.589 x 5.314 x 2e-07 mm, 0 faces, 0 solids (baked)
FEATURE [Part::Feature] Arc100
  shape: bbox 0.7412 x 1.836 x 2e-07 mm, 0 faces, 0 solids (baked)
FEATURE [Part::Feature] Line040
  shape: bbox 8.221 x 5.757 x 2e-07 mm, 0 faces, 0 solids (baked)
FEATURE [Sketcher::SketchObject] Sketch294
  sketch-geometry (1):
    g0: ArcOfCircle CenterX=0 CenterY=0 CenterZ=0 NormalX=0 NormalY=0 NormalZ=1 Radius=58.5 StartAngle=2.68425 EndAngle=2.70977
FEATURE [Part::Feature] Line063
  shape: bbox 11.06 x 11.06 x 2e-07 mm, 0 faces, 0 solids (baked)
FEATURE [Sketcher::SketchObject] Sketch147
  sketch-geometry (1):
    g0: LineSegment StartX=-25.1146 StartY=-46.6002 StartZ=0 EndX=-16.5748 EndY=-44.312 EndZ=0
FEATURE [Sketcher::SketchObject] Sketch085
  sketch-geometry (1):
    g0: ArcOfCircle CenterX=-19.3376 CenterY=17.4937 CenterZ=0 NormalX=0 NormalY=0 NormalZ=1 Radius=2 StartAngle=3.66519 EndAngle=4.75626
FEATURE [Sketcher::SketchObject] Sketch135
  sketch-geometry (1):
    g0: LineSegment StartX=-3.74917 StartY=-26.4937 StartZ=0 EndX=-11.5388 EndY=-39.9857 EndZ=0
FEATURE [Part::Feature] Arc081
  shape: bbox 0.1974 x 0.3418 x 2e-07 mm, 0 faces, 0 solids (baked)
FEATURE [Part::Feature] Arc176
  shape: bbox 0.6419 x 1.347 x 2e-07 mm, 0 faces, 0 solids (baked)
FEATURE [Part::Feature] Line056
  shape: bbox 2.193 x 8.186 x 2e-07 mm, 0 faces, 0 solids (baked)
FEATURE [Part::Feature] Arc347
  shape: bbox 1.373 x 1.499 x 2e-07 mm, 0 faces, 0 solids (baked)
FEATURE [Part::Feature] Line076
  shape: bbox 14.55 x 3.898 x 2e-07 mm, 0 faces, 0 solids (baked)
FEATURE [Sketcher::SketchObject] Sketch341
  sketch-geometry (1):
    g0: ArcOfCircle CenterX=0 CenterY=0 CenterZ=0 NormalX=0 NormalY=0 NormalZ=1 Radius=45.5 StartAngle=2.37742 EndAngle=2.4221
FEATURE [Sketcher::SketchObject] Sketch241
  sketch-geometry (1):
    g0: ArcOfCircle CenterX=0 CenterY=0 CenterZ=0 NormalX=0 NormalY=0 NormalZ=1 Radius=45.5 StartAngle=1.15569 EndAngle=1.20037
FEATURE [Part::Feature] Line047
  shape: bbox 6.365 x 13.65 x 2e-07 mm, 0 faces, 0 solids (baked)
FEATURE [Part::Feature] Line082
  shape: bbox 8.221 x 5.757 x 2e-07 mm, 0 faces, 0 solids (baked)
FEATURE [Part::Feature] Line054
  shape: bbox 0.8747 x 9.998 x 2e-07 mm, 0 faces, 0 solids (baked)
FEATURE [Part::Feature] Arc256
  shape: bbox 2.024 x 0.08867 x 2e-07 mm, 0 faces, 0 solids (baked)
FEATURE [Part::Feature] Arc286
  shape: bbox 1.155 x 1.97 x 2e-07 mm, 0 faces, 0 solids (baked)
FEATURE [Part::Feature] Arc041
  shape: bbox 1.078 x 3.804 x 2e-07 mm, 0 faces, 0 solids (baked)
FEATURE [Sketcher::SketchObject] Sketch172
  sketch-geometry (1):
    g0: LineSegment StartX=-11.5388 StartY=39.9857 StartZ=0 EndX=-3.74917 EndY=26.4937 EndZ=0
FEATURE [Part::Feature] Arc158
  shape: bbox 0.1874 x 1.322 x 2e-07 mm, 0 faces, 0 solids (baked)
FEATURE [Part::Feature] Arc117
  shape: bbox 1.279 x 0.3617 x 2e-07 mm, 0 faces, 0 solids (baked)
FEATURE [Part::Feature] Arc342
  shape: bbox 0.3377 x 1.286 x 2e-07 mm, 0 faces, 0 solids (baked)
FEATURE [Part::Feature] Arc172
  shape: bbox 0.778 x 1.878 x 2e-07 mm, 0 faces, 0 solids (baked)
FEATURE [Part::Feature] Arc101
  shape: bbox 0.5774 x 1.754 x 2e-07 mm, 0 faces, 0 solids (baked)
FEATURE [Sketcher::SketchObject] Sketch084
  sketch-geometry (1):
    g0: ArcOfCircle CenterX=51.5 CenterY=0.135994 CenterZ=0 NormalX=0 NormalY=0 NormalZ=1 Radius=2 StartAngle=6.28252 EndAngle=7.06858
FEATURE [Sketcher::SketchObject] Sketch377
  sketch-geometry (1):
    g0: ArcOfCircle CenterX=-52.6256 CenterY=-7.13188 CenterZ=0 NormalX=0 NormalY=0 NormalZ=1 Radius=1 StartAngle=0.959931 EndAngle=3.10637
FEATURE [Part::Feature] Arc232
  shape: bbox 1.259 x 1.403 x 2e-07 mm, 0 faces, 0 solids (baked)
FEATURE [Part::Feature] Arc354
  shape: bbox 1.613 x 1.237 x 2e-07 mm, 0 faces, 0 solids (baked)
FEATURE [Sketcher::SketchObject] Sketch055
  sketch-geometry (1):
    g0: LineSegment StartX=-11.6266 StartY=44.4631 StartZ=0 EndX=-2.988 EndY=56.8002 EndZ=0
FEATURE [Part::Feature] Arc237
  shape: bbox 0.4372 x 1.646 x 2e-07 mm, 0 faces, 0 solids (baked)
FEATURE [Part::Feature] Arc088
  shape: bbox 8.492 x 9 x 2e-07 mm, 0 faces, 0 solids (baked)
FEATURE [Part::Feature] Arc038
  shape: bbox 2.956 x 2.488 x 2e-07 mm, 0 faces, 0 solids (baked)
FEATURE [Part::Feature] Arc068
  shape: bbox 13.01 x 7.512 x 2e-07 mm, 0 faces, 0 solids (baked)
FEATURE [Part::Feature] Arc274
  shape: bbox 1.819 x 0.9786 x 2e-07 mm, 0 faces, 0 solids (baked)
FEATURE [Part::Feature] Arc037
  shape: bbox 2.956 x 2.488 x 2e-07 mm, 0 faces, 0 solids (baked)
FEATURE [Part::Feature] Line053
  shape: bbox 1.045 x 11.94 x 2e-07 mm, 0 faces, 0 solids (baked)
FEATURE [Part::Feature] Arc109
  shape: bbox 1.086 x 0.2197 x 2e-07 mm, 0 faces, 0 solids (baked)
FEATURE [Sketcher::SketchObject] Sketch332
  sketch-geometry (1):
    g0: LineSegment StartX=-45.8065 StartY=-3.72902 StartZ=0 EndX=-51.7989 EndY=2.26334 EndZ=0
FEATURE [Sketcher::SketchObject] Sketch402
  sketch-geometry (1):
    g0: ArcOfCircle CenterX=7.09467 CenterY=-45.9556 CenterZ=0 NormalX=0 NormalY=0 NormalZ=1 Radius=1 StartAngle=5.49779 EndAngle=8.00715
FEATURE [Sketcher::SketchObject] Sketch083
  sketch-geometry (1):
    g0: ArcOfCircle CenterX=-127.5 CenterY=220.836 CenterZ=0 NormalX=0 NormalY=0 NormalZ=1 Radius=200 StartAngle=5.12976 EndAngle=5.34222
FEATURE [Sketcher::SketchObject] Sketch397
  sketch-geometry (1):
    g0: ArcOfCircle CenterX=255 CenterY=0 CenterZ=0 NormalX=0 NormalY=0 NormalZ=1 Radius=201.5 StartAngle=3.19204 EndAngle=3.20455
FEATURE [Sketcher::SketchObject] Sketch188
  sketch-geometry (1):
    g0: ArcOfCircle CenterX=-19.1562 CenterY=-43.466 CenterZ=0 NormalX=0 NormalY=0 NormalZ=1 Radius=2 StartAngle=1.15569 EndAngle=1.8326
FEATURE [Part::Feature] Arc242
  shape: bbox 1.916 x 0.3107 x 2e-07 mm, 0 faces, 0 solids (baked)
FEATURE [Sketcher::SketchObject] Sketch207
  sketch-geometry (1):
    g0: ArcOfCircle CenterX=-5.48122 CenterY=-25.4937 CenterZ=0 NormalX=0 NormalY=0 NormalZ=1 Radius=2 StartAngle=5.75959 EndAngle=6.85065
FEATURE [Sketcher::SketchObject] Sketch082
  sketch-geometry (1):
    g0: ArcOfCircle CenterX=24.8188 CenterY=14 CenterZ=0 NormalX=0 NormalY=0 NormalZ=1 Radius=2 StartAngle=3.62132 EndAngle=4.71239
FEATURE [Sketcher::SketchObject] Sketch133
  sketch-geometry (1):
    g0: ArcOfCircle CenterX=-5.14323 CenterY=47.2207 CenterZ=0 NormalX=0 NormalY=0 NormalZ=1 Radius=2 StartAngle=4.82088 EndAngle=5.49779
FEATURE [Sketcher::SketchObject] Sketch081
  sketch-geometry (1):
    g0: LineSegment StartX=28.8593 StartY=29.9857 StartZ=0 EndX=21.0697 EndY=16.4937 EndZ=0
FEATURE [Part::Feature] Arc355
  shape: bbox 2.107 x 1.381 x 2e-07 mm, 0 faces, 0 solids (baked)
FEATURE [Sketcher::SketchObject] Sketch233
  sketch-geometry (1):
    g0: LineSegment StartX=3.25637 StartY=57.7208 StartZ=0 EndX=-7.80178 EndY=46.6627 EndZ=0
FEATURE [Part::Feature] Arc191
  shape: bbox 1.469 x 1.087 x 2e-07 mm, 0 faces, 0 solids (baked)
FEATURE [Sketcher::SketchObject] Sketch011
  sketch-geometry (1):
    g0: ArcOfCircle CenterX=0.285064 CenterY=-28.4937 CenterZ=0 NormalX=0 NormalY=0 NormalZ=1 Radius=2 StartAngle=0.523599 EndAngle=1.61467
FEATURE [Sketcher::SketchObject] Sketch054
  sketch-geometry (1):
    g0: LineSegment StartX=24.8188 StartY=12 StartZ=0 EndX=39.598 EndY=12 EndZ=0
FEATURE [Sketcher::SketchObject] Sketch355
  sketch-geometry (1):
    g0: ArcOfCircle CenterX=0 CenterY=0 CenterZ=0 NormalX=0 NormalY=0 NormalZ=1 Radius=45.5 StartAngle=2.20289 EndAngle=2.24757
FEATURE [Sketcher::SketchObject] Sketch259
  sketch-geometry (1):
    g0: ArcOfCircle CenterX=14.1368 CenterY=-38.4857 CenterZ=0 NormalX=0 NormalY=0 NormalZ=1 Radius=3 StartAngle=3.66519 EndAngle=5.06442
FEATURE [Sketcher::SketchObject] Sketch311
  sketch-geometry (1):
    g0: LineSegment StartX=6.81622 StartY=-57.4094 StartZ=0 EndX=15.7861 EndY=-44.599 EndZ=0
FEATURE [Sketcher::SketchObject] Sketch327
  sketch-geometry (1):
    g0: ArcOfCircle CenterX=39.598 CenterY=-14 CenterZ=0 NormalX=0 NormalY=0 NormalZ=1 Radius=2 StartAngle=5.94335 EndAngle=7.85398
FEATURE [Part::Feature] Arc202
  shape: bbox 1.58 x 0.5858 x 2e-07 mm, 0 faces, 0 solids (baked)
FEATURE [Sketcher::SketchObject] Sketch053
  sketch-geometry (1):
    g0: ArcOfCircle CenterX=0.993219 CenterY=46.4894 CenterZ=0 NormalX=0 NormalY=0 NormalZ=1 Radius=1 StartAngle=2.18166 EndAngle=4.69103
FEATURE [Part::Feature] Arc294
  shape: bbox 0.3617 x 1.279 x 2e-07 mm, 0 faces, 0 solids (baked)
FEATURE [Sketcher::SketchObject] Sketch303
  sketch-geometry (1):
    g0: LineSegment StartX=-44.3194 StartY=12.1626 StartZ=0 EndX=-50.6845 EndY=25.8124 EndZ=0
FEATURE [Sketcher::SketchObject] Sketch322
  sketch-geometry (1):
    g0: ArcOfCircle CenterX=47.3965 CenterY=-3.1347 CenterZ=0 NormalX=0 NormalY=0 NormalZ=1 Radius=2 StartAngle=3.07555 EndAngle=3.75246
FEATURE [Sketcher::SketchObject] Sketch198
  sketch-geometry (1):
    g0: ArcOfCircle CenterX=47.2207 CenterY=5.14323 CenterZ=0 NormalX=0 NormalY=0 NormalZ=1 Radius=2 StartAngle=3.25008 EndAngle=3.92699
FEATURE [Part::Feature] Arc326
  shape: bbox 1.469 x 1.087 x 2e-07 mm, 0 faces, 0 solids (baked)
FEATURE [Sketcher::SketchObject] Sketch035
  sketch-geometry (1):
    g0: ArcOfCircle CenterX=255 CenterY=0 CenterZ=0 NormalX=0 NormalY=0 NormalZ=1 Radius=201.5 StartAngle=3.10035 EndAngle=3.10637
FEATURE [Sketcher::SketchObject] Sketch253
  sketch-geometry (1):
    g0: ArcOfCircle CenterX=0 CenterY=0 CenterZ=0 NormalX=0 NormalY=0 NormalZ=1 Radius=44 StartAngle=4.01722 EndAngle=4.36036
FEATURE [Sketcher::SketchObject] Sketch154
  sketch-geometry (1):
    g0: ArcOfCircle CenterX=24.9053 CenterY=-46.2496 CenterZ=0 NormalX=0 NormalY=0 NormalZ=1 Radius=1 StartAngle=2.87979 EndAngle=5.24367
FEATURE [Sketcher::SketchObject] Sketch124
  sketch-geometry (1):
    g0: ArcOfCircle CenterX=-24.5338 CenterY=-14.4937 CenterZ=0 NormalX=0 NormalY=0 NormalZ=1 Radius=2 StartAngle=5.75959 EndAngle=6.85065
FEATURE [Sketcher::SketchObject] Sketch314
  sketch-geometry (1):
    g0: LineSegment StartX=-27.7996 StartY=45.05 StartZ=0 EndX=-30.0879 EndY=36.5102 EndZ=0
FEATURE [Sketcher::SketchObject] Sketch392
  sketch-geometry (1):
    g0: ArcOfCircle CenterX=-43.466 CenterY=19.1562 CenterZ=0 NormalX=0 NormalY=0 NormalZ=1 Radius=2 StartAngle=5.86808 EndAngle=6.54498
FEATURE [Part::Feature] Arc262
  shape: bbox 1.237 x 1.613 x 2e-07 mm, 0 faces, 0 solids (baked)
FEATURE [Part::Feature] Arc149
  shape: bbox 1.291 x 1.078 x 2e-07 mm, 0 faces, 0 solids (baked)
FEATURE [Sketcher::SketchObject] Sketch204
  sketch-geometry (1):
    g0: LineSegment StartX=4.28185 StartY=45.7581 StartZ=0 EndX=14.1028 EndY=52.6348 EndZ=0
FEATURE [Part::Feature] Arc198
  shape: bbox 0.933 x 1.215 x 2e-07 mm, 0 faces, 0 solids (baked)
FEATURE [Sketcher::SketchObject] Sketch261
  sketch-geometry (1):
    g0: ArcOfCircle CenterX=-37.4834 CenterY=-39.4439 CenterZ=0 NormalX=0 NormalY=0 NormalZ=1 Radius=1 StartAngle=1.65806 EndAngle=4.25174
FEATURE [Sketcher::SketchObject] Sketch160
  sketch-geometry (1):
    g0: ArcOfCircle CenterX=-11.3174 CenterY=-46.1321 CenterZ=0 NormalX=0 NormalY=0 NormalZ=1 Radius=2 StartAngle=1.33022 EndAngle=2.00713
FEATURE [Sketcher::SketchObject] Sketch158
  sketch-geometry (1):
    g0: LineSegment StartX=-52.9735 StartY=-17.7915 StartZ=0 EndX=-41.1802 EndY=-23.2909 EndZ=0
FEATURE [Part::Feature] Arc341
  shape: bbox 0.5485 x 1.21 x 2e-07 mm, 0 faces, 0 solids (baked)
FEATURE [Part::Feature] Arc197
  shape: bbox 1.065 x 1.598 x 2e-07 mm, 0 faces, 0 solids (baked)
FEATURE [Sketcher::SketchObject] Sketch211
  sketch-geometry (1):
    g0: ArcOfCircle CenterX=0 CenterY=0 CenterZ=0 NormalX=0 NormalY=0 NormalZ=1 Radius=45.5 StartAngle=3.94822 EndAngle=3.9929
FEATURE [Part::Feature] Arc333
  shape: bbox 0.933 x 1.215 x 2e-07 mm, 0 faces, 0 solids (baked)
FEATURE [Sketcher::SketchObject] Sketch340
  sketch-geometry (1):
    g0: LineSegment StartX=26.1327 StartY=-37.8051 StartZ=0 EndX=23.9393 EndY=-45.9908 EndZ=0
FEATURE [Sketcher::SketchObject] Sketch396
  sketch-geometry (1):
    g0: ArcOfCircle CenterX=0 CenterY=0 CenterZ=0 NormalX=0 NormalY=0 NormalZ=1 Radius=58.5 StartAngle=5.65131 EndAngle=5.67683
FEATURE [Sketcher::SketchObject] Sketch052
  sketch-geometry (1):
    g0: ArcOfCircle CenterX=-47.2207 CenterY=-5.14323 CenterZ=0 NormalX=0 NormalY=0 NormalZ=1 Radius=2 StartAngle=0.108491 EndAngle=0.785398
FEATURE [Part::Feature] Arc230
  shape: bbox 1.259 x 1.626 x 2e-07 mm, 0 faces, 0 solids (baked)
FEATURE [Sketcher::SketchObject] Sketch104
  sketch-geometry (1):
    g0: ArcOfCircle CenterX=0 CenterY=0 CenterZ=0 NormalX=0 NormalY=0 NormalZ=1 Radius=45.5 StartAngle=4.29728 EndAngle=4.34196
FEATURE [Part::Feature] Arc281
  shape: bbox 1.573 x 0.9648 x 2e-07 mm, 0 faces, 0 solids (baked)
FEATURE [Sketcher::SketchObject] Sketch051
  sketch-geometry (1):
    g0: LineSegment StartX=24.8188 StartY=10 StartZ=0 EndX=40.398 EndY=10 EndZ=0
FEATURE [Sketcher::SketchObject] Sketch159
  sketch-geometry (1):
    g0: LineSegment StartX=21.0697 StartY=-16.4937 StartZ=0 EndX=28.8593 EndY=-29.9857 EndZ=0
FEATURE [Sketcher::SketchObject] Sketch292
  sketch-geometry (1):
    g0: LineSegment StartX=32.6929 StartY=32.3005 StartZ=0 EndX=47.6965 EndY=30.9878 EndZ=0
FEATURE [Sketcher::SketchObject] Sketch415
  sketch-geometry (1):
    g0: ArcOfCircle CenterX=0 CenterY=0 CenterZ=0 NormalX=0 NormalY=0 NormalZ=1 Radius=45.5 StartAngle=2.90102 EndAngle=2.9457
FEATURE [Sketcher::SketchObject] Sketch041
  sketch-geometry (1):
    g0: ArcOfCircle CenterX=-45.6102 CenterY=-13.2649 CenterZ=0 NormalX=0 NormalY=0 NormalZ=1 Radius=2 StartAngle=0.283024 EndAngle=0.959931
FEATURE [Sketcher::SketchObject] Sketch395
  sketch-geometry (1):
    g0: ArcOfCircle CenterX=0 CenterY=0 CenterZ=0 NormalX=0 NormalY=0 NormalZ=1 Radius=45.5 StartAngle=1.67929 EndAngle=1.72397
FEATURE [Sketcher::SketchObject] Sketch205
  sketch-geometry (1):
    g0: ArcOfCircle CenterX=0 CenterY=0 CenterZ=0 NormalX=0 NormalY=0 NormalZ=1 Radius=45.5 StartAngle=5.69354 EndAngle=5.73808
FEATURE [Sketcher::SketchObject] Sketch080
  sketch-geometry (1):
    g0: LineSegment StartX=27.7996 StartY=-45.05 StartZ=0 EndX=30.0879 EndY=-36.5102 EndZ=0
FEATURE [Sketcher::SketchObject] Sketch008
  sketch-geometry (1):
    g0: LineSegment StartX=-35.096 StartY=40.7289 StartZ=0 EndX=-35.9707 EndY=30.7308 EndZ=0
FEATURE [Sketcher::SketchObject] Sketch239
  sketch-geometry (1):
    g0: ArcOfCircle CenterX=7.67463 CenterY=41.2929 CenterZ=0 NormalX=0 NormalY=0 NormalZ=1 Radius=2 StartAngle=5.75959 EndAngle=7.67022
FEATURE [Sketcher::SketchObject] Sketch406
  sketch-geometry (1):
    g0: ArcOfCircle CenterX=0 CenterY=0 CenterZ=0 NormalX=0 NormalY=0 NormalZ=1 Radius=58.5 StartAngle=3.55692 EndAngle=3.58243
FEATURE [Sketcher::SketchObject] Sketch180
  sketch-geometry (1):
    g0: LineSegment StartX=-40.398 StartY=10 StartZ=0 EndX=-24.8188 EndY=10 EndZ=0
FEATURE [Part::Feature] Arc288
  shape: bbox 0.5858 x 1.416 x 2e-07 mm, 0 faces, 0 solids (baked)
FEATURE [Sketcher::SketchObject] Sketch385
  sketch-geometry (1):
    g0: ArcOfCircle CenterX=5.14323 CenterY=-47.2207 CenterZ=0 NormalX=0 NormalY=0 NormalZ=1 Radius=2 StartAngle=1.67929 EndAngle=2.35619
FEATURE [Sketcher::SketchObject] Sketch197
  sketch-geometry (1):
    g0: ArcOfCircle CenterX=4.67058 CenterY=56.3066 CenterZ=0 NormalX=0 NormalY=0 NormalZ=1 Radius=2 StartAngle=1.48804 EndAngle=2.35619
FEATURE [Sketcher::SketchObject] Sketch122
  sketch-geometry (1):
    g0: ArcOfCircle CenterX=16.992 CenterY=-49.9557 CenterZ=0 NormalX=0 NormalY=0 NormalZ=1 Radius=2 StartAngle=5.28644 EndAngle=5.84685
FEATURE [Sketcher::SketchObject] Sketch358
  sketch-geometry (1):
    g0: ArcOfCircle CenterX=-40.398 CenterY=7 CenterZ=0 NormalX=0 NormalY=0 NormalZ=1 Radius=3 StartAngle=1.5708 EndAngle=2.97002
FEATURE [Sketcher::SketchObject] Sketch366
  sketch-geometry (1):
    g0: ArcOfCircle CenterX=32.4892 CenterY=-42.0092 CenterZ=0 NormalX=0 NormalY=0 NormalZ=1 Radius=1 StartAngle=3.05433 EndAngle=5.20076
FEATURE [Sketcher::SketchObject] Sketch012
  sketch-geometry (1):
    g0: ArcOfCircle CenterX=-34.9745 CenterY=30.6437 CenterZ=0 NormalX=0 NormalY=0 NormalZ=1 Radius=1 StartAngle=3.05433 EndAngle=5.56369
FEATURE [Sketcher::SketchObject] Sketch140
  sketch-geometry (1):
    g0: LineSegment StartX=2.01711 StartY=-27.4937 StartZ=0 EndX=9.40668 EndY=-40.2929 EndZ=0
FEATURE [Sketcher::SketchObject] Sketch163
  sketch-geometry (1):
    g0: LineSegment StartX=-4.28185 StartY=-45.7581 StartZ=0 EndX=-14.1028 EndY=-52.6348 EndZ=0
FEATURE [Sketcher::SketchObject] Sketch079
  sketch-geometry (1):
    g0: ArcOfCircle CenterX=0 CenterY=0 CenterZ=0 NormalX=0 NormalY=0 NormalZ=1 Radius=44 StartAngle=0.339837 EndAngle=0.707361
FEATURE [Part::Feature] Arc351
  shape: bbox 1.939 x 0.6111 x 2e-07 mm, 0 faces, 0 solids (baked)
FEATURE [Sketcher::SketchObject] Sketch078
  sketch-geometry (1):
    g0: ArcOfCircle CenterX=19.3376 CenterY=17.4937 CenterZ=0 NormalX=0 NormalY=0 NormalZ=1 Radius=2 StartAngle=4.66852 EndAngle=5.75959
FEATURE [Sketcher::SketchObject] Sketch354
  sketch-geometry (1):
    g0: ArcOfCircle CenterX=-52.6116 CenterY=-23.2006 CenterZ=0 NormalX=0 NormalY=0 NormalZ=1 Radius=1 StartAngle=1.309 EndAngle=3.55692
FEATURE [Sketcher::SketchObject] Sketch108
  sketch-geometry (1):
    g0: ArcOfCircle CenterX=5.17792 CenterY=-56.2622 CenterZ=0 NormalX=0 NormalY=0 NormalZ=1 Radius=2 StartAngle=4.80416 EndAngle=5.67232
FEATURE [Sketcher::SketchObject] Sketch361
  sketch-geometry (1):
    g0: ArcOfCircle CenterX=-40.398 CenterY=-7 CenterZ=0 NormalX=0 NormalY=0 NormalZ=1 Radius=3 StartAngle=3.31316 EndAngle=4.71239
FEATURE [Part::Feature] Arc152
  shape: bbox 0.8528 x 1.721 x 2e-07 mm, 0 faces, 0 solids (baked)
FEATURE [Sketcher::SketchObject] Sketch347
  sketch-geometry (1):
    g0: ArcOfCircle CenterX=-52.1283 CenterY=-15.9789 CenterZ=0 NormalX=0 NormalY=0 NormalZ=1 Radius=2 StartAngle=3.06299 EndAngle=4.27606
FEATURE [Part::Feature] Arc248
  shape: bbox 1.21 x 0.5485 x 2e-07 mm, 0 faces, 0 solids (baked)
FEATURE [Sketcher::SketchObject] Sketch276
  sketch-geometry (1):
    g0: LineSegment StartX=37.8051 StartY=26.1327 StartZ=0 EndX=52.3528 EndY=22.2346 EndZ=0
FEATURE [Sketcher::SketchObject] Sketch043
  sketch-geometry (1):
    g0: ArcOfCircle CenterX=0 CenterY=0 CenterZ=0 NormalX=0 NormalY=0 NormalZ=1 Radius=58.5 StartAngle=1.63706 EndAngle=1.66257
FEATURE [Part::Feature] Arc171
  shape: bbox 0.4401 x 1.985 x 2e-07 mm, 0 faces, 0 solids (baked)
FEATURE [Sketcher::SketchObject] Sketch189
  sketch-geometry (1):
    g0: LineSegment StartX=25.1146 StartY=46.6002 StartZ=0 EndX=16.5748 EndY=44.312 EndZ=0
FEATURE [Sketcher::SketchObject] Sketch351
  sketch-geometry (1):
    g0: ArcOfCircle CenterX=-39.4792 CenterY=26.413 CenterZ=0 NormalX=0 NormalY=0 NormalZ=1 Radius=2 StartAngle=5.69354 EndAngle=6.37045
FEATURE [Sketcher::SketchObject] Sketch380
  sketch-geometry (1):
    g0: ArcOfCircle CenterX=51.6731 CenterY=8.39128 CenterZ=0 NormalX=0 NormalY=0 NormalZ=1 Radius=2 StartAngle=6.24194 EndAngle=7.24312
FEATURE [Sketcher::SketchObject] Sketch155
  sketch-geometry (1):
    g0: ArcOfCircle CenterX=-42.6139 CenterY=-20.9835 CenterZ=0 NormalX=0 NormalY=0 NormalZ=1 Radius=2 StartAngle=0.457557 EndAngle=1.13446
FEATURE [Sketcher::SketchObject] Sketch268
  sketch-geometry (1):
    g0: ArcOfCircle CenterX=37.4834 CenterY=39.4439 CenterZ=0 NormalX=0 NormalY=0 NormalZ=1 Radius=1 StartAngle=4.79966 EndAngle=7.39334
FEATURE [Sketcher::SketchObject] Sketch295
  sketch-geometry (1):
    g0: LineSegment StartX=46.3099 StartY=34.6077 StartZ=0 EndX=30.7308 EndY=35.9707 EndZ=0
FEATURE [Sketcher::SketchObject] Sketch077
  sketch-geometry (1):
    g0: ArcOfCircle CenterX=39.7644 CenterY=-24.1048 CenterZ=0 NormalX=0 NormalY=0 NormalZ=1 Radius=1 StartAngle=0.0872665 EndAngle=2.59663
FEATURE [Sketcher::SketchObject] Sketch106
  sketch-geometry (1):
    g0: ArcOfCircle CenterX=0 CenterY=0 CenterZ=0 NormalX=0 NormalY=0 NormalZ=1 Radius=45.5 StartAngle=3.25008 EndAngle=3.29476
FEATURE [Sketcher::SketchObject] Sketch365
  sketch-geometry (1):
    g0: ArcOfCircle CenterX=-127.5 CenterY=220.836 CenterZ=0 NormalX=0 NormalY=0 NormalZ=1 Radius=201.5 StartAngle=5.28644 EndAngle=5.29894
FEATURE [Sketcher::SketchObject] Sketch235
  sketch-geometry (1):
    g0: ArcOfCircle CenterX=19.0526 CenterY=-11 CenterZ=0 NormalX=0 NormalY=0 NormalZ=1 Radius=4.5 StartAngle=0.479729 EndAngle=4.75626
FEATURE [Sketcher::SketchObject] Sketch229
  sketch-geometry (1):
    g0: ArcOfCircle CenterX=-24.8188 CenterY=14 CenterZ=0 NormalX=0 NormalY=0 NormalZ=1 Radius=2 StartAngle=4.71239 EndAngle=5.80346
FEATURE [Sketcher::SketchObject] Sketch076
  sketch-geometry (1):
    g0: LineSegment StartX=30.1913 StartY=28.2929 StartZ=0 EndX=22.8017 EndY=15.4937 EndZ=0
FEATURE [Part::Feature] Arc277
  shape: bbox 1.773 x 0.7412 x 2e-07 mm, 0 faces, 0 solids (baked)
FEATURE [Sketcher::SketchObject] Sketch290
  sketch-geometry (1):
    g0: ArcOfCircle CenterX=11.3174 CenterY=46.1321 CenterZ=0 NormalX=0 NormalY=0 NormalZ=1 Radius=2 StartAngle=4.47181 EndAngle=5.14872
FEATURE [Sketcher::SketchObject] Sketch405
  sketch-geometry (1):
    g0: ArcOfCircle CenterX=0 CenterY=0 CenterZ=0 NormalX=0 NormalY=0 NormalZ=1 Radius=45.5 StartAngle=5.34448 EndAngle=5.38916
FEATURE [Sketcher::SketchObject] Sketch166
  sketch-geometry (1):
    g0: ArcOfCircle CenterX=0 CenterY=0 CenterZ=0 NormalX=0 NormalY=0 NormalZ=1 Radius=60 StartAngle=4.55004 EndAngle=4.87474
FEATURE [Sketcher::SketchObject] Sketch029
  sketch-geometry (1):
    g0: ArcOfCircle CenterX=255 CenterY=0 CenterZ=0 NormalX=0 NormalY=0 NormalZ=1 Radius=201.5 StartAngle=3.14092 EndAngle=3.14928
FEATURE [Sketcher::SketchObject] Sketch375
  sketch-geometry (1):
    g0: ArcOfCircle CenterX=-25.8678 CenterY=44.5324 CenterZ=0 NormalX=0 NormalY=0 NormalZ=1 Radius=2 StartAngle=2.09373 EndAngle=2.87979
FEATURE [Sketcher::SketchObject] Sketch345
  sketch-geometry (1):
    g0: LineSegment StartX=35.096 StartY=-40.7289 StartZ=0 EndX=35.9707 EndY=-30.7308 EndZ=0
FEATURE [Part::Feature] Arc181
  shape: bbox 1.898 x 0.7412 x 2e-07 mm, 0 faces, 0 solids (baked)
FEATURE [Sketcher::SketchObject] Sketch112
  sketch-geometry (1):
    g0: ArcOfCircle CenterX=0 CenterY=0 CenterZ=0 NormalX=0 NormalY=0 NormalZ=1 Radius=45.5 StartAngle=3.42462 EndAngle=3.4693
FEATURE [Sketcher::SketchObject] Sketch117
  sketch-geometry (1):
    g0: ArcOfCircle CenterX=-51.6731 CenterY=-8.39128 CenterZ=0 NormalX=0 NormalY=0 NormalZ=1 Radius=2 StartAngle=3.10035 EndAngle=4.10152
FEATURE [Part::Feature] Arc201
  shape: bbox 1.198 x 0.574 x 2e-07 mm, 0 faces, 0 solids (baked)
FEATURE [Sketcher::SketchObject] Sketch201
  sketch-geometry (1):
    g0: LineSegment StartX=17.7242 StartY=50.7585 StartZ=0 EndX=8.62831 EndY=46.517 EndZ=0
FEATURE [Sketcher::SketchObject] Sketch256
  sketch-geometry (1):
    g0: LineSegment StartX=11.0788 StartY=54.7722 StartZ=0 EndX=0.419642 EndY=47.3085 EndZ=0
FEATURE [Sketcher::SketchObject] Sketch014
  sketch-geometry (1):
    g0: LineSegment StartX=-37.4868 StartY=26.5873 StartZ=0 EndX=-38.5317 EndY=38.5308 EndZ=0
FEATURE [Sketcher::SketchObject] Sketch121
  sketch-geometry (1):
    g0: ArcOfCircle CenterX=0 CenterY=0 CenterZ=0 NormalX=0 NormalY=0 NormalZ=1 Radius=45.5 StartAngle=0.806623 EndAngle=0.851303
FEATURE [Part::Feature] Circle003
  shape: bbox 5.5 x 5.5 x 2e-07 mm, 0 faces, 0 solids (baked)
FEATURE [Sketcher::SketchObject] Sketch350
  sketch-geometry (1):
    g0: ArcOfCircle CenterX=3.1347 CenterY=47.3965 CenterZ=0 NormalX=0 NormalY=0 NormalZ=1 Radius=2 StartAngle=4.64635 EndAngle=5.32325
FEATURE [Sketcher::SketchObject] Sketch346
  sketch-geometry (1):
    g0: ArcOfCircle CenterX=0 CenterY=0 CenterZ=0 NormalX=0 NormalY=0 NormalZ=1 Radius=45.5 StartAngle=4.64635 EndAngle=4.69088
FEATURE [Part::Feature] Arc148
  shape: bbox 1.259 x 1.403 x 2e-07 mm, 0 faces, 0 solids (baked)
FEATURE [Sketcher::SketchObject] Sketch391
  sketch-geometry (1):
    g0: ArcOfCircle CenterX=-127.5 CenterY=-220.836 CenterZ=0 NormalX=0 NormalY=0 NormalZ=1 Radius=201.5 StartAngle=1.04653 EndAngle=1.05488
FEATURE [Sketcher::SketchObject] Sketch359
  sketch-geometry (1):
    g0: ArcOfCircle CenterX=0 CenterY=0 CenterZ=0 NormalX=0 NormalY=0 NormalZ=1 Radius=44 StartAngle=0.875625 EndAngle=1.21877
FEATURE [Sketcher::SketchObject] Sketch266
  sketch-geometry (1):
    g0: LineSegment StartX=-3.72902 StartY=45.8065 StartZ=0 EndX=6.92065 EndY=56.4562 EndZ=0
FEATURE [Sketcher::SketchObject] Sketch409
  sketch-geometry (1):
    g0: ArcOfCircle CenterX=44.0254 CenterY=14.967 CenterZ=0 NormalX=0 NormalY=0 NormalZ=1 Radius=1 StartAngle=0.959931 EndAngle=3.4693
FEATURE [Sketcher::SketchObject] Sketch246
  sketch-geometry (1):
    g0: LineSegment StartX=51.6159 StartY=26.0403 StartZ=0 EndX=36.5102 EndY=30.0879 EndZ=0
FEATURE [Sketcher::SketchObject] Sketch068
  sketch-geometry (1):
    g0: ArcOfCircle CenterX=-39.7644 CenterY=24.1048 CenterZ=0 NormalX=0 NormalY=0 NormalZ=1 Radius=1 StartAngle=3.22886 EndAngle=5.73823
FEATURE [Sketcher::SketchObject] Sketch419
  sketch-geometry (1):
    g0: ArcOfCircle CenterX=-29.122 CenterY=36.2514 CenterZ=0 NormalX=0 NormalY=0 NormalZ=1 Radius=1 StartAngle=2.87979 EndAngle=5.38916
FEATURE [Sketcher::SketchObject] Sketch416
  sketch-geometry (1):
    g0: ArcOfCircle CenterX=0 CenterY=0 CenterZ=0 NormalX=0 NormalY=0 NormalZ=1 Radius=58.5 StartAngle=3.73145 EndAngle=3.75696
FEATURE [Sketcher::SketchObject] Sketch308
  sketch-geometry (1):
    g0: ArcOfCircle CenterX=43.466 CenterY=-19.1562 CenterZ=0 NormalX=0 NormalY=0 NormalZ=1 Radius=2 StartAngle=2.72649 EndAngle=3.40339
FEATURE [Sketcher::SketchObject] Sketch329
  sketch-geometry (1):
    g0: Circle CenterX=19.0526 CenterY=-11 CenterZ=0 NormalX=0 NormalY=0 NormalZ=1 Radius=2.75
FEATURE [Sketcher::SketchObject] Sketch144
  sketch-geometry (1):
    g0: ArcOfCircle CenterX=0 CenterY=0 CenterZ=0 NormalX=0 NormalY=0 NormalZ=1 Radius=45.5 StartAngle=0.457557 EndAngle=0.502092
FEATURE [Sketcher::SketchObject] Sketch267
  sketch-geometry (1):
    g0: ArcOfCircle CenterX=-7.09467 CenterY=45.9556 CenterZ=0 NormalX=0 NormalY=0 NormalZ=1 Radius=1 StartAngle=2.35619 EndAngle=4.86556
FEATURE [Sketcher::SketchObject] Sketch132
  sketch-geometry (1):
    g0: ArcOfCircle CenterX=-52.506 CenterY=1.55623 CenterZ=0 NormalX=0 NormalY=0 NormalZ=1 Radius=1 StartAngle=0.785398 EndAngle=3.14928
FEATURE [Sketcher::SketchObject] Sketch186
  sketch-geometry (1):
    g0: LineSegment StartX=34.5926 StartY=41.6858 StartZ=0 EndX=24.0177 EndY=40.7606 EndZ=0
FEATURE [Sketcher::SketchObject] Sketch113
  sketch-geometry (1):
    g0: ArcOfCircle CenterX=36.2514 CenterY=29.122 CenterZ=0 NormalX=0 NormalY=0 NormalZ=1 Radius=1 StartAngle=1.309 EndAngle=3.81836
FEATURE [Sketcher::SketchObject] Sketch075
  sketch-geometry (1):
    g0: ArcOfCircle CenterX=-255 CenterY=0 CenterZ=0 NormalX=0 NormalY=0 NormalZ=1 Radius=200 StartAngle=6.17695 EndAngle=6.38942
FEATURE [Sketcher::SketchObject] Sketch412
  sketch-geometry (1):
    g0: ArcOfCircle CenterX=127.5 CenterY=-220.836 CenterZ=0 NormalX=0 NormalY=0 NormalZ=1 Radius=201.5 StartAngle=2.05315 EndAngle=2.05917
FEATURE [Sketcher::SketchObject] Sketch074
  sketch-geometry (1):
    g0: LineSegment StartX=-52.9143 StartY=-1.55021 StartZ=0 EndX=-46.6627 EndY=-7.80178 EndZ=0
FEATURE [Sketcher::SketchObject] Sketch291
  sketch-geometry (1):
    g0: ArcOfCircle CenterX=0 CenterY=0 CenterZ=0 NormalX=0 NormalY=0 NormalZ=1 Radius=45.5 StartAngle=3.59915 EndAngle=3.64368
FEATURE [Sketcher::SketchObject] Sketch206
  sketch-geometry (1):
    g0: ArcOfCircle CenterX=0 CenterY=0 CenterZ=0 NormalX=0 NormalY=0 NormalZ=1 Radius=45.5 StartAngle=5.51901 EndAngle=5.56369
FEATURE [Sketcher::SketchObject] Sketch157
  sketch-geometry (1):
    g0: ArcOfCircle CenterX=-22.3845 CenterY=40.7576 CenterZ=0 NormalX=0 NormalY=0 NormalZ=1 Radius=1 StartAngle=2.70526 EndAngle=5.21463
FEATURE [Sketcher::SketchObject] Sketch050
  sketch-geometry (1):
    g0: LineSegment StartX=24.8188 StartY=-10 StartZ=0 EndX=40.398 EndY=-10 EndZ=0
FEATURE [Sketcher::SketchObject] Sketch199
  sketch-geometry (1):
    g0: ArcOfCircle CenterX=31.9233 CenterY=27.2929 CenterZ=0 NormalX=0 NormalY=0 NormalZ=1 Radius=2 StartAngle=0.707361 EndAngle=2.61799
FEATURE [Sketcher::SketchObject] Sketch150
  sketch-geometry (1):
    g0: ArcOfCircle CenterX=0 CenterY=0 CenterZ=0 NormalX=0 NormalY=0 NormalZ=1 Radius=60 StartAngle=1.40844 EndAngle=1.73315
FEATURE [Sketcher::SketchObject] Sketch357
  sketch-geometry (1):
    g0: ArcOfCircle CenterX=-19.0526 CenterY=-11 CenterZ=0 NormalX=0 NormalY=0 NormalZ=1 Radius=4.5 StartAngle=4.66852 EndAngle=8.94505
FEATURE [Sketcher::SketchObject] Sketch183
  sketch-geometry (1):
    g0: LineSegment StartX=-39.598 StartY=-12 StartZ=0 EndX=-24.8188 EndY=-12 EndZ=0
FEATURE [Sketcher::SketchObject] Sketch131
  sketch-geometry (1):
    g0: ArcOfCircle CenterX=-39.9023 CenterY=37.155 CenterZ=0 NormalX=0 NormalY=0 NormalZ=1 Radius=2 StartAngle=2.01579 EndAngle=3.22886
FEATURE [Sketcher::SketchObject] Sketch325
  sketch-geometry (1):
    g0: LineSegment StartX=-12.1626 StartY=-44.3194 StartZ=0 EndX=-20.559 EndY=-48.2348 EndZ=0
FEATURE [Sketcher::SketchObject] Sketch130
  sketch-geometry (1):
    g0: ArcOfCircle CenterX=0.285064 CenterY=28.4937 CenterZ=0 NormalX=0 NormalY=0 NormalZ=1 Radius=2 StartAngle=4.66852 EndAngle=5.75959
FEATURE [Sketcher::SketchObject] Sketch126
  sketch-geometry (1):
    g0: ArcOfCircle CenterX=47.7836 CenterY=31.984 CenterZ=0 NormalX=0 NormalY=0 NormalZ=1 Radius=1 StartAngle=4.62512 EndAngle=6.87304
FEATURE [Sketcher::SketchObject] Sketch316
  sketch-geometry (1):
    g0: LineSegment StartX=-19.6738 StartY=-41.5341 StartZ=0 EndX=-27.8595 EndY=-43.7275 EndZ=0
FEATURE [Sketcher::SketchObject] Sketch399
  sketch-geometry (1):
    g0: ArcOfCircle CenterX=-14.967 CenterY=44.0254 CenterZ=0 NormalX=0 NormalY=0 NormalZ=1 Radius=1 StartAngle=2.53073 EndAngle=5.04009
FEATURE [Sketcher::SketchObject] Sketch344
  sketch-geometry (1):
    g0: LineSegment StartX=-52.8202 StartY=-10.0296 StartZ=0 EndX=-44.599 EndY=-15.7861 EndZ=0
FEATURE [Sketcher::SketchObject] Sketch049
  sketch-geometry (1):
    g0: ArcOfCircle CenterX=28.0645 CenterY=-38.3227 CenterZ=0 NormalX=0 NormalY=0 NormalZ=1 Radius=2 StartAngle=2.20289 EndAngle=2.87979
FEATURE [Sketcher::SketchObject] Sketch015
  sketch-geometry (1):
    g0: ArcOfCircle CenterX=-31.9233 CenterY=27.2929 CenterZ=0 NormalX=0 NormalY=0 NormalZ=1 Radius=2 StartAngle=0.523599 EndAngle=2.43423
FEATURE [Sketcher::SketchObject] Sketch407
  sketch-geometry (1):
    g0: ArcOfCircle CenterX=0 CenterY=0 CenterZ=0 NormalX=0 NormalY=0 NormalZ=1 Radius=58.5 StartAngle=3.55692 EndAngle=3.58243
FEATURE [Sketcher::SketchObject] Sketch021
  sketch-geometry (1):
    g0: ArcOfCircle CenterX=0 CenterY=0 CenterZ=0 NormalX=0 NormalY=0 NormalZ=1 Radius=45.5 StartAngle=1.33022 EndAngle=1.3749
FEATURE [Sketcher::SketchObject] Sketch364
  sketch-geometry (1):
    g0: ArcOfCircle CenterX=-18.5695 CenterY=-48.9458 CenterZ=0 NormalX=0 NormalY=0 NormalZ=1 Radius=2 StartAngle=4.14754 EndAngle=5.14872
FEATURE [Sketcher::SketchObject] Sketch367
  sketch-geometry (1):
    g0: ArcOfCircle CenterX=-4.67058 CenterY=-56.3066 CenterZ=0 NormalX=0 NormalY=0 NormalZ=1 Radius=2 StartAngle=4.62963 EndAngle=5.49779
FEATURE [Sketcher::SketchObject] Sketch378
  sketch-geometry (1):
    g0: ArcOfCircle CenterX=-51.5 CenterY=-0.135994 CenterZ=0 NormalX=0 NormalY=0 NormalZ=1 Radius=2 StartAngle=3.14092 EndAngle=3.92699
FEATURE [Sketcher::SketchObject] Sketch193
  sketch-geometry (1):
    g0: ArcOfCircle CenterX=-127.5 CenterY=-220.836 CenterZ=0 NormalX=0 NormalY=0 NormalZ=1 Radius=201.5 StartAngle=0.968596 EndAngle=0.973004
FEATURE [Sketcher::SketchObject] Sketch210
  sketch-geometry (1):
    g0: ArcOfCircle CenterX=0 CenterY=0 CenterZ=0 NormalX=0 NormalY=0 NormalZ=1 Radius=45.5 StartAngle=2.55195 EndAngle=2.59649
FEATURE [Sketcher::SketchObject] Sketch152
  sketch-geometry (1):
    g0: LineSegment StartX=3.72902 StartY=-45.8065 StartZ=0 EndX=-6.92065 EndY=-56.4562 EndZ=0
FEATURE [Sketcher::SketchObject] Sketch073
  sketch-geometry (1):
    g0: ArcOfCircle CenterX=52.6116 CenterY=23.2006 CenterZ=0 NormalX=0 NormalY=0 NormalZ=1 Radius=1 StartAngle=4.45059 EndAngle=6.69851
FEATURE [Part::Feature] Arc236
  shape: bbox 0.5774 x 1.754 x 2e-07 mm, 0 faces, 0 solids (baked)
FEATURE [Sketcher::SketchObject] Sketch293
  sketch-geometry (1):
    g0: ArcOfCircle CenterX=38.3227 CenterY=28.0645 CenterZ=0 NormalX=0 NormalY=0 NormalZ=1 Radius=2 StartAngle=3.77368 EndAngle=4.45059
FEATURE [Part::Feature] Arc162
  shape: bbox 0.949 x 0.9291 x 2e-07 mm, 0 faces, 0 solids (baked)
FEATURE [Part::Feature] Arc278
  shape: bbox 1.804 x 0.5774 x 2e-07 mm, 0 faces, 0 solids (baked)
FEATURE [Sketcher::SketchObject] Sketch040
  sketch-geometry (1):
    g0: ArcOfCircle CenterX=45.6106 CenterY=-9.05093 CenterZ=0 NormalX=0 NormalY=0 NormalZ=1 Radius=1 StartAngle=0.436332 EndAngle=2.9457
FEATURE [Sketcher::SketchObject] Sketch334
  sketch-geometry (1):
    g0: LineSegment StartX=44.4631 StartY=11.6266 StartZ=0 EndX=52.0521 EndY=6.31273 EndZ=0
FEATURE [Sketcher::SketchObject] Sketch025
  sketch-geometry (1):
    g0: ArcOfCircle CenterX=24.8188 CenterY=-8 CenterZ=0 NormalX=0 NormalY=0 NormalZ=1 Radius=2 StartAngle=3.62132 EndAngle=4.71239
FEATURE [Sketcher::SketchObject] Sketch045
  sketch-geometry (1):
    g0: ArcOfCircle CenterX=0 CenterY=0 CenterZ=0 NormalX=0 NormalY=0 NormalZ=1 Radius=60 StartAngle=0.361245 EndAngle=0.685953
FEATURE [Sketcher::SketchObject] Sketch283
  sketch-geometry (1):
    g0: ArcOfCircle CenterX=7.67463 CenterY=-41.2929 CenterZ=0 NormalX=0 NormalY=0 NormalZ=1 Radius=2 StartAngle=4.89615 EndAngle=6.80678
FEATURE [Part::Feature] Arc259
  shape: bbox 1.461 x 0.8365 x 2e-07 mm, 0 faces, 0 solids (baked)
FEATURE [Sketcher::SketchObject] Sketch200
  sketch-geometry (1):
    g0: ArcOfCircle CenterX=127.5 CenterY=220.836 CenterZ=0 NormalX=0 NormalY=0 NormalZ=1 Radius=201.5 StartAngle=4.18812 EndAngle=4.19648
FEATURE [Sketcher::SketchObject] Sketch321
  sketch-geometry (1):
    g0: LineSegment StartX=-3.25637 StartY=-57.7208 StartZ=0 EndX=7.80178 EndY=-46.6627 EndZ=0
FEATURE [Sketcher::SketchObject] Sketch232
  sketch-geometry (1):
    g0: ArcOfCircle CenterX=22.3845 CenterY=-40.7576 CenterZ=0 NormalX=0 NormalY=0 NormalZ=1 Radius=1 StartAngle=5.84685 EndAngle=8.35622
FEATURE [Part::Feature] Arc291
  shape: bbox 0.1699 x 1.324 x 2e-07 mm, 0 faces, 0 solids (baked)
FEATURE [Sketcher::SketchObject] Sketch228
  sketch-geometry (1):
    g0: ArcOfCircle CenterX=0 CenterY=0 CenterZ=0 NormalX=0 NormalY=0 NormalZ=1 Radius=44 StartAngle=1.38703 EndAngle=1.75456
FEATURE [Part::Feature] Arc207
  shape: bbox 0.3377 x 1.286 x 2e-07 mm, 0 faces, 0 solids (baked)
FEATURE [Sketcher::SketchObject] Sketch119
  sketch-geometry (1):
    g0: LineSegment StartX=24.8188 StartY=-12 StartZ=0 EndX=39.598 EndY=-12 EndZ=0
FEATURE [Sketcher::SketchObject] Sketch072
  sketch-geometry (1):
    g0: ArcOfCircle CenterX=-24.8188 CenterY=-14 CenterZ=0 NormalX=0 NormalY=0 NormalZ=1 Radius=2 StartAngle=0.479729 EndAngle=1.5708
FEATURE [Sketcher::SketchObject] Sketch048
  sketch-geometry (1):
    g0: LineSegment StartX=-41.8947 StartY=36.9807 StartZ=0 EndX=-40.7606 EndY=24.0177 EndZ=0
FEATURE [Part::Feature] Arc138
  shape: bbox 1.707 x 1.153 x 2e-07 mm, 0 faces, 0 solids (baked)
FEATURE [Sketcher::SketchObject] Sketch071
  sketch-geometry (1):
    g0: ArcOfCircle CenterX=-33.1036 CenterY=40.5546 CenterZ=0 NormalX=0 NormalY=0 NormalZ=1 Radius=2 StartAngle=2.05315 EndAngle=3.05433
FEATURE [Sketcher::SketchObject] Sketch280
  sketch-geometry (1):
    g0: ArcOfCircle CenterX=25.6322 CenterY=44.6683 CenterZ=0 NormalX=0 NormalY=0 NormalZ=1 Radius=2 StartAngle=1.04653 EndAngle=1.8326
FEATURE [Sketcher::SketchObject] Sketch026
  sketch-geometry (1):
    g0: ArcOfCircle CenterX=52.6256 CenterY=7.13188 CenterZ=0 NormalX=0 NormalY=0 NormalZ=1 Radius=1 StartAngle=4.10152 EndAngle=6.24796
FEATURE [Sketcher::SketchObject] Sketch231
  sketch-geometry (1):
    g0: ArcOfCircle CenterX=-9.05093 CenterY=-45.6106 CenterZ=0 NormalX=0 NormalY=0 NormalZ=1 Radius=1 StartAngle=5.14872 EndAngle=7.65809
FEATURE [Sketcher::SketchObject] Sketch247
  sketch-geometry (1):
    g0: LineSegment StartX=19.1709 StartY=-41.7686 StartZ=0 EndX=14.5114 EndY=-51.7609 EndZ=0
FEATURE [Sketcher::SketchObject] Sketch224
  sketch-geometry (1):
    g0: LineSegment StartX=-41.5341 StartY=19.6738 StartZ=0 EndX=-45.4322 EndY=34.2216 EndZ=0
FEATURE [Sketcher::SketchObject] Sketch269
  sketch-geometry (1):
    g0: Circle CenterX=0 CenterY=22 CenterZ=0 NormalX=0 NormalY=0 NormalZ=1 Radius=2.75
FEATURE [Sketcher::SketchObject] Sketch312
  sketch-geometry (1):
    g0: ArcOfCircle CenterX=40.398 CenterY=7 CenterZ=0 NormalX=0 NormalY=0 NormalZ=1 Radius=3 StartAngle=0.171572 EndAngle=1.5708
FEATURE [Part::Feature] Arc119
  shape: bbox 2.015 x 0.2652 x 2e-07 mm, 0 faces, 0 solids (baked)
FEATURE [Sketcher::SketchObject] Sketch372
  sketch-geometry (1):
    g0: ArcOfCircle CenterX=25.8678 CenterY=-44.5324 CenterZ=0 NormalX=0 NormalY=0 NormalZ=1 Radius=2 StartAngle=5.23532 EndAngle=6.02139
FEATURE [Sketcher::SketchObject] Sketch024
  sketch-geometry (1):
    g0: LineSegment StartX=48.3595 StartY=-31.6805 StartZ=0 EndX=44.312 EndY=-16.5748 EndZ=0
FEATURE [Part::Feature] Arc173
  shape: bbox 0.8661 x 1.215 x 2e-07 mm, 0 faces, 0 solids (baked)
FEATURE [Sketcher::SketchObject] Sketch282
  sketch-geometry (1):
    g0: ArcOfCircle CenterX=-28.0645 CenterY=38.3227 CenterZ=0 NormalX=0 NormalY=0 NormalZ=1 Radius=2 StartAngle=5.34448 EndAngle=6.02139
FEATURE [Sketcher::SketchObject] Sketch317
  sketch-geometry (1):
    g0: ArcOfCircle CenterX=-24.8188 CenterY=-8 CenterZ=0 NormalX=0 NormalY=0 NormalZ=1 Radius=2 StartAngle=4.71239 EndAngle=5.80346
FEATURE [Sketcher::SketchObject] Sketch047
  sketch-geometry (1):
    g0: ArcOfCircle CenterX=0 CenterY=0 CenterZ=0 NormalX=0 NormalY=0 NormalZ=1 Radius=60 StartAngle=5.59723 EndAngle=5.92194
FEATURE [Sketcher::SketchObject] Sketch390
  sketch-geometry (1):
    g0: ArcOfCircle CenterX=-51.5908 CenterY=25.3898 CenterZ=0 NormalX=0 NormalY=0 NormalZ=1 Radius=1 StartAngle=0.436332 EndAngle=2.68425
FEATURE [Part::Feature] Arc175
  shape: bbox 0.1428 x 2.515 x 2e-07 mm, 0 faces, 0 solids (baked)
FEATURE [Part::Feature] Arc142
  shape: bbox 1.773 x 0.7412 x 2e-07 mm, 0 faces, 0 solids (baked)
FEATURE [Part::Feature] Arc321
  shape: bbox 1.322 x 1.574 x 2e-07 mm, 0 faces, 0 solids (baked)
FEATURE [Sketcher::SketchObject] Sketch
  sketch-geometry (1):
    g0: LineSegment StartX=2.01711 StartY=27.4937 StartZ=0 EndX=9.40668 EndY=40.2929 EndZ=0
FEATURE [Part::Feature] Arc143
  shape: bbox 1.804 x 0.5774 x 2e-07 mm, 0 faces, 0 solids (baked)
FEATURE [Sketcher::SketchObject] Sketch271
  sketch-geometry (1):
    g0: LineSegment StartX=51.6159 StartY=26.0403 StartZ=0 EndX=36.5102 EndY=30.0879 EndZ=0
FEATURE [Sketcher::SketchObject] Sketch320
  sketch-geometry (1):
    g0: LineSegment StartX=18.8046 StartY=-50.801 StartZ=0 EndX=23.2909 EndY=-41.1802 EndZ=0
FEATURE [Sketcher::SketchObject] Sketch417
  sketch-geometry (1):
    g0: ArcOfCircle CenterX=-51.7589 CenterY=10.2623 CenterZ=0 NormalX=0 NormalY=0 NormalZ=1 Radius=2 StartAngle=3.19204 EndAngle=3.75246
FEATURE [Sketcher::SketchObject] Sketch310
  sketch-geometry (1):
    g0: LineSegment StartX=53.3972 StartY=-9.11519 StartZ=0 EndX=47.3085 EndY=-0.419642 EndZ=0
FEATURE [Part::Feature] Arc258
  shape: bbox 1.027 x 0.6462 x 2e-07 mm, 0 faces, 0 solids (baked)
FEATURE [Part::Feature] Arc185
  shape: bbox 1.153 x 1.707 x 2e-07 mm, 0 faces, 0 solids (baked)
FEATURE [Part::Feature] Arc325
  shape: bbox 1.507 x 1.259 x 2e-07 mm, 0 faces, 0 solids (baked)
FEATURE [Part::Feature] Arc144
  shape: bbox 1.819 x 1.063 x 2e-07 mm, 0 faces, 0 solids (baked)
FEATURE [Sketcher::SketchObject] Sketch195
  sketch-geometry (1):
    g0: LineSegment StartX=12.1626 StartY=44.3194 StartZ=0 EndX=20.559 EndY=48.2348 EndZ=0
FEATURE [Part::Feature] Arc219
  shape: bbox 1.613 x 1.237 x 2e-07 mm, 0 faces, 0 solids (baked)
FEATURE [Sketcher::SketchObject] Sketch369
  sketch-geometry (1):
    g0: ArcOfCircle CenterX=-32.4892 CenterY=42.0092 CenterZ=0 NormalX=0 NormalY=0 NormalZ=1 Radius=1 StartAngle=6.19592 EndAngle=8.34235
FEATURE [Sketcher::SketchObject] Sketch070
  sketch-geometry (1):
    g0: ArcOfCircle CenterX=-127.5 CenterY=220.836 CenterZ=0 NormalX=0 NormalY=0 NormalZ=1 Radius=201.5 StartAngle=5.15739 EndAngle=5.16179
FEATURE [Sketcher::SketchObject] Sketch020
  sketch-geometry (1):
    g0: ArcOfCircle CenterX=0 CenterY=0 CenterZ=0 NormalX=0 NormalY=0 NormalZ=1 Radius=58.5 StartAngle=4.77865 EndAngle=4.80416
FEATURE [Part::Feature] Arc298
  shape: bbox 0.6196 x 1.358 x 2e-07 mm, 0 faces, 0 solids (baked)
FEATURE [Sketcher::SketchObject] Sketch230
  sketch-geometry (1):
    g0: ArcOfCircle CenterX=34.9745 CenterY=-30.6437 CenterZ=0 NormalX=0 NormalY=0 NormalZ=1 Radius=1 StartAngle=6.19592 EndAngle=8.70529
FEATURE [Sketcher::SketchObject] Sketch265
  sketch-geometry (1):
    g0: LineSegment StartX=41.8947 StartY=-36.9807 StartZ=0 EndX=40.7606 EndY=-24.0177 EndZ=0
FEATURE [Part::Feature] Arc263
  shape: bbox 0.6196 x 1.358 x 2e-07 mm, 0 faces, 0 solids (baked)
FEATURE [Sketcher::SketchObject] Sketch307
  sketch-geometry (1):
    g0: ArcOfCircle CenterX=46.4894 CenterY=-0.993219 CenterZ=0 NormalX=0 NormalY=0 NormalZ=1 Radius=1 StartAngle=0.610865 EndAngle=3.12023
FEATURE [Sketcher::SketchObject] Sketch277
  sketch-geometry (1):
    g0: ArcOfCircle CenterX=-15.4177 CenterY=52.1835 CenterZ=0 NormalX=0 NormalY=0 NormalZ=1 Radius=1 StartAngle=5.84685 EndAngle=8.44053
FEATURE [Sketcher::SketchObject] Sketch330
  sketch-geometry (1):
    g0: LineSegment StartX=45.8065 StartY=3.72902 StartZ=0 EndX=51.7989 EndY=-2.26334 EndZ=0
FEATURE [Sketcher::SketchObject] Sketch161
  sketch-geometry (1):
    g0: LineSegment StartX=22.8017 StartY=-15.4937 StartZ=0 EndX=30.1913 EndY=-28.2929 EndZ=0
FEATURE [Sketcher::SketchObject] Sketch023
  sketch-geometry (1):
    g0: ArcOfCircle CenterX=52.506 CenterY=-1.55623 CenterZ=0 NormalX=0 NormalY=0 NormalZ=1 Radius=1 StartAngle=3.92699 EndAngle=6.29087
FEATURE [Sketcher::SketchObject] Sketch319
  sketch-geometry (1):
    g0: ArcOfCircle CenterX=-46.4277 CenterY=32.1982 CenterZ=0 NormalX=0 NormalY=0 NormalZ=1 Radius=2 StartAngle=2.53523 EndAngle=3.40339
FEATURE [Sketcher::SketchObject] Sketch010
  sketch-geometry (1):
    g0: ArcOfCircle CenterX=0 CenterY=0 CenterZ=0 NormalX=0 NormalY=0 NormalZ=1 Radius=44 StartAngle=2.97002 EndAngle=3.31316
FEATURE [Sketcher::SketchObject] Sketch002
  sketch-geometry (1):
    g0: ArcOfCircle CenterX=-45.6106 CenterY=9.05093 CenterZ=0 NormalX=0 NormalY=0 NormalZ=1 Radius=1 StartAngle=3.57792 EndAngle=6.08729
FEATURE [Sketcher::SketchObject] Sketch263
  sketch-geometry (1):
    g0: ArcOfCircle CenterX=0 CenterY=0 CenterZ=0 NormalX=0 NormalY=0 NormalZ=1 Radius=58.5 StartAngle=1.46252 EndAngle=1.48804
FEATURE [Sketcher::SketchObject] Sketch123
  sketch-geometry (1):
    g0: ArcOfCircle CenterX=0 CenterY=-22 CenterZ=0 NormalX=0 NormalY=0 NormalZ=1 Radius=4.5 StartAngle=4.66852 EndAngle=4.75626
FEATURE [Part::Feature] Arc338
  shape: bbox 1.08 x 0.7733 x 2e-07 mm, 0 faces, 0 solids (baked)
FEATURE [Sketcher::SketchObject] Sketch287
  sketch-geometry (1):
    g0: ArcOfCircle CenterX=40.398 CenterY=-7 CenterZ=0 NormalX=0 NormalY=0 NormalZ=1 Radius=3 StartAngle=4.71239 EndAngle=6.11161
FEATURE [Sketcher::SketchObject] Sketch404
  sketch-geometry (1):
    g0: ArcOfCircle CenterX=52.9011 CenterY=-12.7396 CenterZ=0 NormalX=0 NormalY=0 NormalZ=1 Radius=1 StartAngle=3.75246 EndAngle=6.34614
FEATURE [Sketcher::SketchObject] Sketch297
  sketch-geometry (1):
    g0: ArcOfCircle CenterX=-26.2612 CenterY=-31.4857 CenterZ=0 NormalX=0 NormalY=0 NormalZ=1 Radius=3 StartAngle=2.61799 EndAngle=4.01722
FEATURE [Sketcher::SketchObject] Sketch389
  sketch-geometry (1):
    g0: ArcOfCircle CenterX=42.6139 CenterY=20.9835 CenterZ=0 NormalX=0 NormalY=0 NormalZ=1 Radius=2 StartAngle=3.59915 EndAngle=4.27606
FEATURE [Part::Feature] Arc137
  shape: bbox 1.574 x 1.322 x 2e-07 mm, 0 faces, 0 solids (baked)
FEATURE [Sketcher::SketchObject] Sketch176
  sketch-geometry (1):
    g0: ArcOfCircle CenterX=-255 CenterY=0 CenterZ=0 NormalX=0 NormalY=0 NormalZ=1 Radius=201.5 StartAngle=6.20458 EndAngle=6.20899
FEATURE [Part::Feature] Arc187
  shape: bbox 0.8919 x 1.701 x 2e-07 mm, 0 faces, 0 solids (baked)
FEATURE [Part::Feature] Arc303
  shape: bbox 0.04637 x 1.212 x 2e-07 mm, 0 faces, 0 solids (baked)
FEATURE [Part::Feature] Arc213
  shape: bbox 1.073 x 0.5659 x 2e-07 mm, 0 faces, 0 solids (baked)
FEATURE [Part::Feature] Arc123
  shape: bbox 1.027 x 0.6462 x 2e-07 mm, 0 faces, 0 solids (baked)
FEATURE [Part::Feature] Arc196
  shape: bbox 1.139 x 1.98 x 2e-07 mm, 0 faces, 0 solids (baked)
FEATURE [Sketcher::SketchObject] Sketch046
  sketch-geometry (1):
    g0: ArcOfCircle CenterX=-24.5338 CenterY=14.4937 CenterZ=0 NormalX=0 NormalY=0 NormalZ=1 Radius=2 StartAngle=5.71572 EndAngle=6.80678
FEATURE [Sketcher::SketchObject] Sketch016
  sketch-geometry (1):
    g0: ArcOfCircle CenterX=40.7576 CenterY=22.3845 CenterZ=0 NormalX=0 NormalY=0 NormalZ=1 Radius=1 StartAngle=1.13446 EndAngle=3.64383
FEATURE [Part::Feature] Arc306
  shape: bbox 0.4401 x 1.985 x 2e-07 mm, 0 faces, 0 solids (baked)
FEATURE [Sketcher::SketchObject] Sketch019
  sketch-geometry (1):
    g0: ArcOfCircle CenterX=-43.346 CenterY=16.8336 CenterZ=0 NormalX=0 NormalY=0 NormalZ=1 Radius=1 StartAngle=3.40339 EndAngle=5.91276
FEATURE [Part::Feature] Arc266
  shape: bbox 0.8459 x 1.23 x 2e-07 mm, 0 faces, 0 solids (baked)
FEATURE [Sketcher::SketchObject] Sketch352
  sketch-geometry (1):
    g0: ArcOfCircle CenterX=0 CenterY=0 CenterZ=0 NormalX=0 NormalY=0 NormalZ=1 Radius=45.5 StartAngle=5.86808 EndAngle=5.91276
FEATURE [Part::Feature] Arc289
  shape: bbox 0.3592 x 1.046 x 2e-07 mm, 0 faces, 0 solids (baked)
FEATURE [Part::Feature] Arc174
  shape: bbox 0.2652 x 2.015 x 2e-07 mm, 0 faces, 0 solids (baked)
FEATURE [Sketcher::SketchObject] Sketch250
  sketch-geometry (1):
    g0: ArcOfCircle CenterX=24.1048 CenterY=39.7644 CenterZ=0 NormalX=0 NormalY=0 NormalZ=1 Radius=1 StartAngle=1.65806 EndAngle=4.16743
FEATURE [Sketcher::SketchObject] Sketch343
  sketch-geometry (1):
    g0: LineSegment StartX=44.3194 StartY=-12.1626 StartZ=0 EndX=50.6845 EndY=-25.8124 EndZ=0
FEATURE [Sketcher::SketchObject] Sketch202
  sketch-geometry (1):
    g0: ArcOfCircle CenterX=0 CenterY=0 CenterZ=0 NormalX=0 NormalY=0 NormalZ=1 Radius=44 StartAngle=5.57582 EndAngle=5.94335
FEATURE [Sketcher::SketchObject] Sketch116
  sketch-geometry (1):
    g0: ArcOfCircle CenterX=-45.9556 CenterY=-7.09467 CenterZ=0 NormalX=0 NormalY=0 NormalZ=1 Radius=1 StartAngle=3.92699 EndAngle=6.43636
FEATURE [Sketcher::SketchObject] Sketch418
  sketch-geometry (1):
    g0: ArcOfCircle CenterX=0 CenterY=0 CenterZ=0 NormalX=0 NormalY=0 NormalZ=1 Radius=45.5 StartAngle=0.108491 EndAngle=0.153172
FEATURE [Sketcher::SketchObject] Sketch411
  sketch-geometry (1):
    g0: ArcOfCircle CenterX=-255 CenterY=0 CenterZ=0 NormalX=0 NormalY=0 NormalZ=1 Radius=201.5 StartAngle=6.24194 EndAngle=6.24796
FEATURE [Sketcher::SketchObject] Sketch151
  sketch-geometry (1):
    g0: ArcOfCircle CenterX=0 CenterY=0 CenterZ=0 NormalX=0 NormalY=0 NormalZ=1 Radius=58.5 StartAngle=2.50972 EndAngle=2.53523
FEATURE [Sketcher::SketchObject] Sketch036
  sketch-geometry (1):
    g0: ArcOfCircle CenterX=-30.6437 CenterY=-34.9745 CenterZ=0 NormalX=0 NormalY=0 NormalZ=1 Radius=1 StartAngle=4.62512 EndAngle=7.13449
FEATURE [Sketcher::SketchObject] Sketch289
  sketch-geometry (1):
    g0: ArcOfCircle CenterX=0 CenterY=0 CenterZ=0 NormalX=0 NormalY=0 NormalZ=1 Radius=44 StartAngle=3.48143 EndAngle=3.84895
FEATURE [Sketcher::SketchObject] Sketch033
  sketch-geometry (1):
    g0: LineSegment StartX=-6.81622 StartY=57.4094 StartZ=0 EndX=-15.7861 EndY=44.599 EndZ=0
FEATURE [Sketcher::SketchObject] Sketch141
  sketch-geometry (1):
    g0: Circle CenterX=0 CenterY=-22 CenterZ=0 NormalX=0 NormalY=0 NormalZ=1 Radius=2.75
FEATURE [Sketcher::SketchObject] Sketch238
  sketch-geometry (1):
    g0: ArcOfCircle CenterX=30.6437 CenterY=34.9745 CenterZ=0 NormalX=0 NormalY=0 NormalZ=1 Radius=1 StartAngle=1.48353 EndAngle=3.9929
FEATURE [Sketcher::SketchObject] Sketch134
  sketch-geometry (1):
    g0: ArcOfCircle CenterX=-3.80715 CenterY=57.3738 CenterZ=0 NormalX=0 NormalY=0 NormalZ=1 Radius=1 StartAngle=5.67232 EndAngle=7.92024
FEATURE [Sketcher::SketchObject] Sketch260
  sketch-geometry (1):
    g0: ArcOfCircle CenterX=0 CenterY=0 CenterZ=0 NormalX=0 NormalY=0 NormalZ=1 Radius=44 StartAngle=6.11161 EndAngle=6.45476
FEATURE [Sketcher::SketchObject] Sketch249
  sketch-geometry (1):
    g0: ArcOfCircle CenterX=0 CenterY=0 CenterZ=0 NormalX=0 NormalY=0 NormalZ=1 Radius=44 StartAngle=1.92282 EndAngle=2.26597
FEATURE [Sketcher::SketchObject] Sketch262
  sketch-geometry (1):
    g0: ArcOfCircle CenterX=24.8188 CenterY=-14 CenterZ=0 NormalX=0 NormalY=0 NormalZ=1 Radius=2 StartAngle=1.5708 EndAngle=2.66186
FEATURE [Sketcher::SketchObject] Sketch356
  sketch-geometry (1):
    g0: ArcOfCircle CenterX=-13.5292 CenterY=-53.454 CenterZ=0 NormalX=0 NormalY=0 NormalZ=1 Radius=1 StartAngle=2.18166 EndAngle=4.1146
FEATURE [Sketcher::SketchObject] Sketch323
  sketch-geometry (1):
    g0: LineSegment StartX=52.9143 StartY=1.55021 StartZ=0 EndX=46.6627 EndY=7.80178 EndZ=0
FEATURE [Part::Feature] Arc318
  shape: bbox 1.626 x 1.259 x 2e-07 mm, 0 faces, 0 solids (baked)
FEATURE [App::DocumentObjectGroup] _  label="0"
  Group = -> [Line,Line001,Line002,Line003,Line004,Line005,Line006,Line007,Line008,Line009,Line010,Line011,Line012,Line013,Line014,Line015,Line016,Line017,Line018,Line019,Line020,Line021,Line022,Line023,Line024,Line025,Line026,Line027,Line028,Line029,Line030,Line031,Line032,Line033,Line034,Line035,Line036,Line037,Line038,Line039,Line040,Line041,Line042,Line043,Line044,Line045,Line046,Line047,Line048,Line049,+370 more]
FEATURE [Sketcher::SketchObject] Sketch013
  sketch-geometry (1):
    g0: ArcOfCircle CenterX=34.2928 CenterY=-32.8672 CenterZ=0 NormalX=0 NormalY=0 NormalZ=1 Radius=2 StartAngle=2.37742 EndAngle=3.05433
FEATURE [Sketcher::SketchObject] Sketch191
  sketch-geometry (1):
    g0: ArcOfCircle CenterX=26.2612 CenterY=31.4857 CenterZ=0 NormalX=0 NormalY=0 NormalZ=1 Radius=3 StartAngle=5.75959 EndAngle=7.15881
FEATURE [Sketcher::SketchObject] Sketch338
  sketch-geometry (1):
    g0: ArcOfCircle CenterX=19.0526 CenterY=11 CenterZ=0 NormalX=0 NormalY=0 NormalZ=1 Radius=4.5 StartAngle=0.479729 EndAngle=0.567469
FEATURE [Sketcher::SketchObject] Sketch339
  sketch-geometry (1):
    g0: ArcOfCircle CenterX=0 CenterY=0 CenterZ=0 NormalX=0 NormalY=0 NormalZ=1 Radius=58.5 StartAngle=5.82585 EndAngle=5.85136
FEATURE [Sketcher::SketchObject] Sketch383
  sketch-geometry (1):
    g0: ArcOfCircle CenterX=-46.3981 CenterY=33.9627 CenterZ=0 NormalX=0 NormalY=0 NormalZ=1 Radius=1 StartAngle=0.261799 EndAngle=2.50972
FEATURE [Sketcher::SketchObject] Sketch184
  sketch-geometry (1):
    g0: LineSegment StartX=-9.40668 StartY=40.2929 StartZ=0 EndX=-2.01711 EndY=27.4937 EndZ=0
FEATURE [Sketcher::SketchObject] Sketch125
  sketch-geometry (1):
    g0: LineSegment StartX=-44.4631 StartY=-11.6266 StartZ=0 EndX=-52.0521 EndY=-6.31273 EndZ=0
FEATURE [Sketcher::SketchObject] Sketch410
  sketch-geometry (1):
    g0: ArcOfCircle CenterX=-6.21354 CenterY=-57.1633 CenterZ=0 NormalX=0 NormalY=0 NormalZ=1 Radius=1 StartAngle=2.35619 EndAngle=4.60412
FEATURE [Sketcher::SketchObject] Sketch394
  sketch-geometry (1):
    g0: ArcOfCircle CenterX=45.9556 CenterY=7.09467 CenterZ=0 NormalX=0 NormalY=0 NormalZ=1 Radius=1 StartAngle=0.785398 EndAngle=3.29476
FEATURE [Sketcher::SketchObject] Sketch349
  sketch-geometry (1):
    g0: ArcOfCircle CenterX=46.1321 CenterY=-11.3174 CenterZ=0 NormalX=0 NormalY=0 NormalZ=1 Radius=2 StartAngle=2.90102 EndAngle=3.57792
FEATURE [Sketcher::SketchObject] Sketch175
  sketch-geometry (1):
    g0: LineSegment StartX=-30.1913 StartY=28.2929 StartZ=0 EndX=-22.8017 EndY=15.4937 EndZ=0
FEATURE [Sketcher::SketchObject] Sketch143
  sketch-geometry (1):
    g0: Circle CenterX=19.0526 CenterY=11 CenterZ=0 NormalX=0 NormalY=0 NormalZ=1 Radius=2.75
FEATURE [Sketcher::SketchObject] Sketch102
  sketch-geometry (1):
    g0: LineSegment StartX=-17.7242 StartY=-50.7585 StartZ=0 EndX=-8.62831 EndY=-46.517 EndZ=0
FEATURE [Sketcher::SketchObject] Sketch336
  sketch-geometry (1):
    g0: LineSegment StartX=52.8202 StartY=10.0296 StartZ=0 EndX=44.599 EndY=15.7861 EndZ=0
FEATURE [Sketcher::SketchObject] Sketch164
  sketch-geometry (1):
    g0: ArcOfCircle CenterX=-16.8336 CenterY=-43.346 CenterZ=0 NormalX=0 NormalY=0 NormalZ=1 Radius=1 StartAngle=4.97419 EndAngle=7.48355
FEATURE [Sketcher::SketchObject] Sketch370
  sketch-geometry (1):
    g0: ArcOfCircle CenterX=0 CenterY=0 CenterZ=0 NormalX=0 NormalY=0 NormalZ=1 Radius=45.5 StartAngle=3.77368 EndAngle=3.81836
FEATURE [Sketcher::SketchObject] Sketch209
  sketch-geometry (1):
    g0: ArcOfCircle CenterX=19.3376 CenterY=-17.4937 CenterZ=0 NormalX=0 NormalY=0 NormalZ=1 Radius=2 StartAngle=0.523599 EndAngle=1.61467
FEATURE [Sketcher::SketchObject] Sketch194
  sketch-geometry (1):
    g0: ArcOfCircle CenterX=14.1368 CenterY=38.4857 CenterZ=0 NormalX=0 NormalY=0 NormalZ=1 Radius=3 StartAngle=1.21877 EndAngle=2.61799
FEATURE [Sketcher::SketchObject] Sketch254
  sketch-geometry (1):
    g0: ArcOfCircle CenterX=46.1356 CenterY=32.6153 CenterZ=0 NormalX=0 NormalY=0 NormalZ=1 Radius=2 StartAngle=0.615372 EndAngle=1.48353
FEATURE [Sketcher::SketchObject] Sketch169
  sketch-geometry (1):
    g0: ArcOfCircle CenterX=5.48122 CenterY=-25.4937 CenterZ=0 NormalX=0 NormalY=0 NormalZ=1 Radius=2 StartAngle=2.57412 EndAngle=3.66519
FEATURE [Sketcher::SketchObject] Sketch388
  sketch-geometry (1):
    g0: ArcOfCircle CenterX=-20.1364 CenterY=-49.1411 CenterZ=0 NormalX=0 NormalY=0 NormalZ=1 Radius=1 StartAngle=2.00713 EndAngle=4.15356
